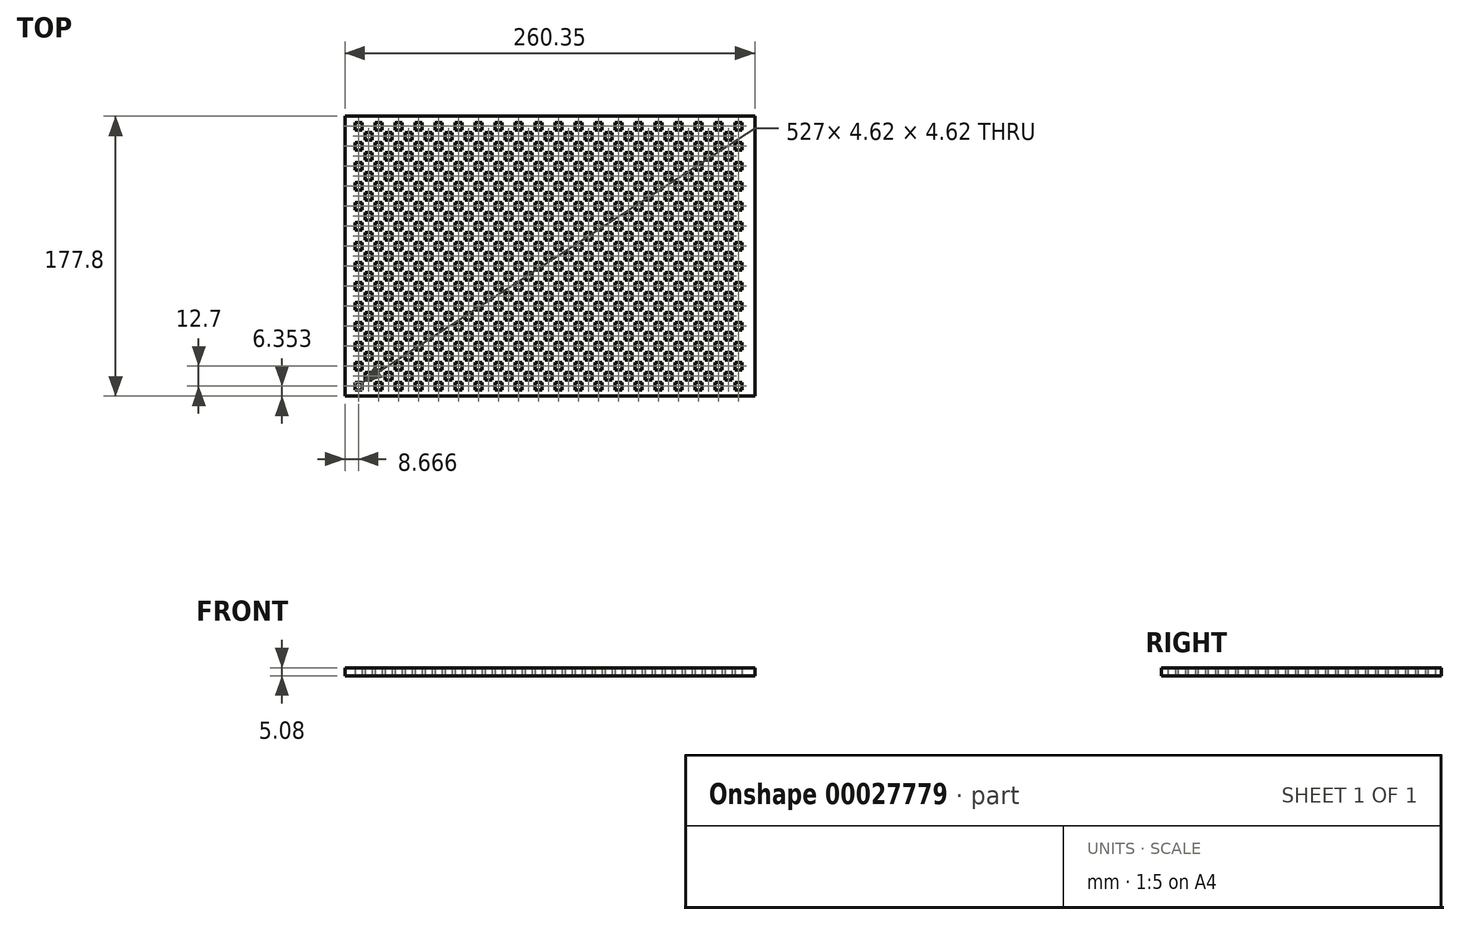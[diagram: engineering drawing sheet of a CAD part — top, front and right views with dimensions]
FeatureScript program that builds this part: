
annotation { "Feature Type Name" : "Feature", "Feature Type Description" : "" }
export const myFeature = defineFeature(function(context is Context, id is Id, definition is map)
    precondition{}
    {
        {
            var Q0;
            Q0=qCreatedBy(makeId("Top.planeOp"),FACE);
            var sketch = newSketch(context, id + "F0", { "sketchPlane" : qUnion([Q0])});
            skLineSegment(sketch, "E0.bottom", {"start": v(-130.56, -73.68) * mm, "end": v(129.8, -73.68) * mm});
            skLineSegment(sketch, "E0.top", {"start": v(-130.56, 104.12) * mm, "end": v(129.8, 104.12) * mm});
            skLineSegment(sketch, "E0.left", {"start": v(-130.56, -73.68) * mm, "end": v(-130.56, 104.12) * mm});
            skLineSegment(sketch, "E0.right", {"start": v(129.8, -73.68) * mm, "end": v(129.8, 104.12) * mm});
            skLineSegment(sketch, "E1.bottom", {"start": v(-124.2, 100.08) * mm, "end": v(-119.58, 100.08) * mm});
            skLineSegment(sketch, "E1.top", {"start": v(-124.2, 95.46) * mm, "end": v(-119.58, 95.46) * mm});
            skLineSegment(sketch, "E1.left", {"start": v(-124.2, 100.08) * mm, "end": v(-124.2, 95.46) * mm});
            skLineSegment(sketch, "E1.right", {"start": v(-119.58, 100.08) * mm, "end": v(-119.58, 95.46) * mm});
            skLineSegment(sketch, "E2.0.1.0", {"start": v(-124.2, 87.38) * mm, "end": v(-119.58, 87.38) * mm});
            skLineSegment(sketch, "E2.0.1.1", {"start": v(-119.58, 87.38) * mm, "end": v(-119.58, 82.76) * mm});
            skLineSegment(sketch, "E2.0.1.2", {"start": v(-124.2, 82.76) * mm, "end": v(-119.58, 82.76) * mm});
            skLineSegment(sketch, "E2.0.1.3", {"start": v(-124.2, 87.38) * mm, "end": v(-124.2, 82.76) * mm});
            skLineSegment(sketch, "E2.0.2.0", {"start": v(-124.2, 74.68) * mm, "end": v(-119.58, 74.68) * mm});
            skLineSegment(sketch, "E2.0.2.1", {"start": v(-119.58, 74.68) * mm, "end": v(-119.58, 70.06) * mm});
            skLineSegment(sketch, "E2.0.2.2", {"start": v(-124.2, 70.06) * mm, "end": v(-119.58, 70.06) * mm});
            skLineSegment(sketch, "E2.0.2.3", {"start": v(-124.2, 74.68) * mm, "end": v(-124.2, 70.06) * mm});
            skLineSegment(sketch, "E2.0.3.0", {"start": v(-124.2, 61.98) * mm, "end": v(-119.58, 61.98) * mm});
            skLineSegment(sketch, "E2.0.3.1", {"start": v(-119.58, 61.98) * mm, "end": v(-119.58, 57.36) * mm});
            skLineSegment(sketch, "E2.0.3.2", {"start": v(-124.2, 57.36) * mm, "end": v(-119.58, 57.36) * mm});
            skLineSegment(sketch, "E2.0.3.3", {"start": v(-124.2, 61.98) * mm, "end": v(-124.2, 57.36) * mm});
            skLineSegment(sketch, "E2.0.4.0", {"start": v(-124.2, 49.28) * mm, "end": v(-119.58, 49.28) * mm});
            skLineSegment(sketch, "E2.0.4.1", {"start": v(-119.58, 49.28) * mm, "end": v(-119.58, 44.66) * mm});
            skLineSegment(sketch, "E2.0.4.2", {"start": v(-124.2, 44.66) * mm, "end": v(-119.58, 44.66) * mm});
            skLineSegment(sketch, "E2.0.4.3", {"start": v(-124.2, 49.28) * mm, "end": v(-124.2, 44.66) * mm});
            skLineSegment(sketch, "E2.0.5.0", {"start": v(-124.2, 36.58) * mm, "end": v(-119.58, 36.58) * mm});
            skLineSegment(sketch, "E2.0.5.1", {"start": v(-119.58, 36.58) * mm, "end": v(-119.58, 31.96) * mm});
            skLineSegment(sketch, "E2.0.5.2", {"start": v(-124.2, 31.96) * mm, "end": v(-119.58, 31.96) * mm});
            skLineSegment(sketch, "E2.0.5.3", {"start": v(-124.2, 36.58) * mm, "end": v(-124.2, 31.96) * mm});
            skLineSegment(sketch, "E2.0.6.0", {"start": v(-124.2, 23.88) * mm, "end": v(-119.58, 23.88) * mm});
            skLineSegment(sketch, "E2.0.6.1", {"start": v(-119.58, 23.88) * mm, "end": v(-119.58, 19.26) * mm});
            skLineSegment(sketch, "E2.0.6.2", {"start": v(-124.2, 19.26) * mm, "end": v(-119.58, 19.26) * mm});
            skLineSegment(sketch, "E2.0.6.3", {"start": v(-124.2, 23.88) * mm, "end": v(-124.2, 19.26) * mm});
            skLineSegment(sketch, "E2.0.7.0", {"start": v(-124.2, 11.18) * mm, "end": v(-119.58, 11.18) * mm});
            skLineSegment(sketch, "E2.0.7.1", {"start": v(-119.58, 11.18) * mm, "end": v(-119.58, 6.56) * mm});
            skLineSegment(sketch, "E2.0.7.2", {"start": v(-124.2, 6.56) * mm, "end": v(-119.58, 6.56) * mm});
            skLineSegment(sketch, "E2.0.7.3", {"start": v(-124.2, 11.18) * mm, "end": v(-124.2, 6.56) * mm});
            skLineSegment(sketch, "E2.0.8.0", {"start": v(-124.2, -1.52) * mm, "end": v(-119.58, -1.52) * mm});
            skLineSegment(sketch, "E2.0.8.1", {"start": v(-119.58, -1.52) * mm, "end": v(-119.58, -6.14) * mm});
            skLineSegment(sketch, "E2.0.8.2", {"start": v(-124.2, -6.14) * mm, "end": v(-119.58, -6.14) * mm});
            skLineSegment(sketch, "E2.0.8.3", {"start": v(-124.2, -1.52) * mm, "end": v(-124.2, -6.14) * mm});
            skLineSegment(sketch, "E2.0.9.0", {"start": v(-124.2, -14.22) * mm, "end": v(-119.58, -14.22) * mm});
            skLineSegment(sketch, "E2.0.9.1", {"start": v(-119.58, -14.22) * mm, "end": v(-119.58, -18.84) * mm});
            skLineSegment(sketch, "E2.0.9.2", {"start": v(-124.2, -18.84) * mm, "end": v(-119.58, -18.84) * mm});
            skLineSegment(sketch, "E2.0.9.3", {"start": v(-124.2, -14.22) * mm, "end": v(-124.2, -18.84) * mm});
            skLineSegment(sketch, "E2.0.10.0", {"start": v(-124.2, -26.92) * mm, "end": v(-119.58, -26.92) * mm});
            skLineSegment(sketch, "E2.0.10.1", {"start": v(-119.58, -26.92) * mm, "end": v(-119.58, -31.54) * mm});
            skLineSegment(sketch, "E2.0.10.2", {"start": v(-124.2, -31.54) * mm, "end": v(-119.58, -31.54) * mm});
            skLineSegment(sketch, "E2.0.10.3", {"start": v(-124.2, -26.92) * mm, "end": v(-124.2, -31.54) * mm});
            skLineSegment(sketch, "E2.0.11.0", {"start": v(-124.2, -39.62) * mm, "end": v(-119.58, -39.62) * mm});
            skLineSegment(sketch, "E2.0.11.1", {"start": v(-119.58, -39.62) * mm, "end": v(-119.58, -44.24) * mm});
            skLineSegment(sketch, "E2.0.11.2", {"start": v(-124.2, -44.24) * mm, "end": v(-119.58, -44.24) * mm});
            skLineSegment(sketch, "E2.0.11.3", {"start": v(-124.2, -39.62) * mm, "end": v(-124.2, -44.24) * mm});
            skLineSegment(sketch, "E2.0.12.0", {"start": v(-124.2, -52.32) * mm, "end": v(-119.58, -52.32) * mm});
            skLineSegment(sketch, "E2.0.12.1", {"start": v(-119.58, -52.32) * mm, "end": v(-119.58, -56.94) * mm});
            skLineSegment(sketch, "E2.0.12.2", {"start": v(-124.2, -56.94) * mm, "end": v(-119.58, -56.94) * mm});
            skLineSegment(sketch, "E2.0.12.3", {"start": v(-124.2, -52.32) * mm, "end": v(-124.2, -56.94) * mm});
            skLineSegment(sketch, "E2.0.13.0", {"start": v(-124.2, -65.02) * mm, "end": v(-119.58, -65.02) * mm});
            skLineSegment(sketch, "E2.0.13.1", {"start": v(-119.58, -65.02) * mm, "end": v(-119.58, -69.64) * mm});
            skLineSegment(sketch, "E2.0.13.2", {"start": v(-124.2, -69.64) * mm, "end": v(-119.58, -69.64) * mm});
            skLineSegment(sketch, "E2.0.13.3", {"start": v(-124.2, -65.02) * mm, "end": v(-124.2, -69.64) * mm});
            skLineSegment(sketch, "E2.1.0.0", {"start": v(-111.5, 100.08) * mm, "end": v(-106.88, 100.08) * mm});
            skLineSegment(sketch, "E2.1.0.1", {"start": v(-106.88, 100.08) * mm, "end": v(-106.88, 95.46) * mm});
            skLineSegment(sketch, "E2.1.0.2", {"start": v(-111.5, 95.46) * mm, "end": v(-106.88, 95.46) * mm});
            skLineSegment(sketch, "E2.1.0.3", {"start": v(-111.5, 100.08) * mm, "end": v(-111.5, 95.46) * mm});
            skLineSegment(sketch, "E2.1.1.0", {"start": v(-111.5, 87.38) * mm, "end": v(-106.88, 87.38) * mm});
            skLineSegment(sketch, "E2.1.1.1", {"start": v(-106.88, 87.38) * mm, "end": v(-106.88, 82.76) * mm});
            skLineSegment(sketch, "E2.1.1.2", {"start": v(-111.5, 82.76) * mm, "end": v(-106.88, 82.76) * mm});
            skLineSegment(sketch, "E2.1.1.3", {"start": v(-111.5, 87.38) * mm, "end": v(-111.5, 82.76) * mm});
            skLineSegment(sketch, "E2.1.2.0", {"start": v(-111.5, 74.68) * mm, "end": v(-106.88, 74.68) * mm});
            skLineSegment(sketch, "E2.1.2.1", {"start": v(-106.88, 74.68) * mm, "end": v(-106.88, 70.06) * mm});
            skLineSegment(sketch, "E2.1.2.2", {"start": v(-111.5, 70.06) * mm, "end": v(-106.88, 70.06) * mm});
            skLineSegment(sketch, "E2.1.2.3", {"start": v(-111.5, 74.68) * mm, "end": v(-111.5, 70.06) * mm});
            skLineSegment(sketch, "E2.1.3.0", {"start": v(-111.5, 61.98) * mm, "end": v(-106.88, 61.98) * mm});
            skLineSegment(sketch, "E2.1.3.1", {"start": v(-106.88, 61.98) * mm, "end": v(-106.88, 57.36) * mm});
            skLineSegment(sketch, "E2.1.3.2", {"start": v(-111.5, 57.36) * mm, "end": v(-106.88, 57.36) * mm});
            skLineSegment(sketch, "E2.1.3.3", {"start": v(-111.5, 61.98) * mm, "end": v(-111.5, 57.36) * mm});
            skLineSegment(sketch, "E2.1.4.0", {"start": v(-111.5, 49.28) * mm, "end": v(-106.88, 49.28) * mm});
            skLineSegment(sketch, "E2.1.4.1", {"start": v(-106.88, 49.28) * mm, "end": v(-106.88, 44.66) * mm});
            skLineSegment(sketch, "E2.1.4.2", {"start": v(-111.5, 44.66) * mm, "end": v(-106.88, 44.66) * mm});
            skLineSegment(sketch, "E2.1.4.3", {"start": v(-111.5, 49.28) * mm, "end": v(-111.5, 44.66) * mm});
            skLineSegment(sketch, "E2.1.5.0", {"start": v(-111.5, 36.58) * mm, "end": v(-106.88, 36.58) * mm});
            skLineSegment(sketch, "E2.1.5.1", {"start": v(-106.88, 36.58) * mm, "end": v(-106.88, 31.96) * mm});
            skLineSegment(sketch, "E2.1.5.2", {"start": v(-111.5, 31.96) * mm, "end": v(-106.88, 31.96) * mm});
            skLineSegment(sketch, "E2.1.5.3", {"start": v(-111.5, 36.58) * mm, "end": v(-111.5, 31.96) * mm});
            skLineSegment(sketch, "E2.1.6.0", {"start": v(-111.5, 23.88) * mm, "end": v(-106.88, 23.88) * mm});
            skLineSegment(sketch, "E2.1.6.1", {"start": v(-106.88, 23.88) * mm, "end": v(-106.88, 19.26) * mm});
            skLineSegment(sketch, "E2.1.6.2", {"start": v(-111.5, 19.26) * mm, "end": v(-106.88, 19.26) * mm});
            skLineSegment(sketch, "E2.1.6.3", {"start": v(-111.5, 23.88) * mm, "end": v(-111.5, 19.26) * mm});
            skLineSegment(sketch, "E2.1.7.0", {"start": v(-111.5, 11.18) * mm, "end": v(-106.88, 11.18) * mm});
            skLineSegment(sketch, "E2.1.7.1", {"start": v(-106.88, 11.18) * mm, "end": v(-106.88, 6.56) * mm});
            skLineSegment(sketch, "E2.1.7.2", {"start": v(-111.5, 6.56) * mm, "end": v(-106.88, 6.56) * mm});
            skLineSegment(sketch, "E2.1.7.3", {"start": v(-111.5, 11.18) * mm, "end": v(-111.5, 6.56) * mm});
            skLineSegment(sketch, "E2.1.8.0", {"start": v(-111.5, -1.52) * mm, "end": v(-106.88, -1.52) * mm});
            skLineSegment(sketch, "E2.1.8.1", {"start": v(-106.88, -1.52) * mm, "end": v(-106.88, -6.14) * mm});
            skLineSegment(sketch, "E2.1.8.2", {"start": v(-111.5, -6.14) * mm, "end": v(-106.88, -6.14) * mm});
            skLineSegment(sketch, "E2.1.8.3", {"start": v(-111.5, -1.52) * mm, "end": v(-111.5, -6.14) * mm});
            skLineSegment(sketch, "E2.1.9.0", {"start": v(-111.5, -14.22) * mm, "end": v(-106.88, -14.22) * mm});
            skLineSegment(sketch, "E2.1.9.1", {"start": v(-106.88, -14.22) * mm, "end": v(-106.88, -18.84) * mm});
            skLineSegment(sketch, "E2.1.9.2", {"start": v(-111.5, -18.84) * mm, "end": v(-106.88, -18.84) * mm});
            skLineSegment(sketch, "E2.1.9.3", {"start": v(-111.5, -14.22) * mm, "end": v(-111.5, -18.84) * mm});
            skLineSegment(sketch, "E2.1.10.0", {"start": v(-111.5, -26.92) * mm, "end": v(-106.88, -26.92) * mm});
            skLineSegment(sketch, "E2.1.10.1", {"start": v(-106.88, -26.92) * mm, "end": v(-106.88, -31.54) * mm});
            skLineSegment(sketch, "E2.1.10.2", {"start": v(-111.5, -31.54) * mm, "end": v(-106.88, -31.54) * mm});
            skLineSegment(sketch, "E2.1.10.3", {"start": v(-111.5, -26.92) * mm, "end": v(-111.5, -31.54) * mm});
            skLineSegment(sketch, "E2.1.11.0", {"start": v(-111.5, -39.62) * mm, "end": v(-106.88, -39.62) * mm});
            skLineSegment(sketch, "E2.1.11.1", {"start": v(-106.88, -39.62) * mm, "end": v(-106.88, -44.24) * mm});
            skLineSegment(sketch, "E2.1.11.2", {"start": v(-111.5, -44.24) * mm, "end": v(-106.88, -44.24) * mm});
            skLineSegment(sketch, "E2.1.11.3", {"start": v(-111.5, -39.62) * mm, "end": v(-111.5, -44.24) * mm});
            skLineSegment(sketch, "E2.1.12.0", {"start": v(-111.5, -52.32) * mm, "end": v(-106.88, -52.32) * mm});
            skLineSegment(sketch, "E2.1.12.1", {"start": v(-106.88, -52.32) * mm, "end": v(-106.88, -56.94) * mm});
            skLineSegment(sketch, "E2.1.12.2", {"start": v(-111.5, -56.94) * mm, "end": v(-106.88, -56.94) * mm});
            skLineSegment(sketch, "E2.1.12.3", {"start": v(-111.5, -52.32) * mm, "end": v(-111.5, -56.94) * mm});
            skLineSegment(sketch, "E2.1.13.0", {"start": v(-111.5, -65.02) * mm, "end": v(-106.88, -65.02) * mm});
            skLineSegment(sketch, "E2.1.13.1", {"start": v(-106.88, -65.02) * mm, "end": v(-106.88, -69.64) * mm});
            skLineSegment(sketch, "E2.1.13.2", {"start": v(-111.5, -69.64) * mm, "end": v(-106.88, -69.64) * mm});
            skLineSegment(sketch, "E2.1.13.3", {"start": v(-111.5, -65.02) * mm, "end": v(-111.5, -69.64) * mm});
            skLineSegment(sketch, "E2.2.0.0", {"start": v(-98.8, 100.08) * mm, "end": v(-94.18, 100.08) * mm});
            skLineSegment(sketch, "E2.2.0.1", {"start": v(-94.18, 100.08) * mm, "end": v(-94.18, 95.46) * mm});
            skLineSegment(sketch, "E2.2.0.2", {"start": v(-98.8, 95.46) * mm, "end": v(-94.18, 95.46) * mm});
            skLineSegment(sketch, "E2.2.0.3", {"start": v(-98.8, 100.08) * mm, "end": v(-98.8, 95.46) * mm});
            skLineSegment(sketch, "E2.2.1.0", {"start": v(-98.8, 87.38) * mm, "end": v(-94.18, 87.38) * mm});
            skLineSegment(sketch, "E2.2.1.1", {"start": v(-94.18, 87.38) * mm, "end": v(-94.18, 82.76) * mm});
            skLineSegment(sketch, "E2.2.1.2", {"start": v(-98.8, 82.76) * mm, "end": v(-94.18, 82.76) * mm});
            skLineSegment(sketch, "E2.2.1.3", {"start": v(-98.8, 87.38) * mm, "end": v(-98.8, 82.76) * mm});
            skLineSegment(sketch, "E2.2.2.0", {"start": v(-98.8, 74.68) * mm, "end": v(-94.18, 74.68) * mm});
            skLineSegment(sketch, "E2.2.2.1", {"start": v(-94.18, 74.68) * mm, "end": v(-94.18, 70.06) * mm});
            skLineSegment(sketch, "E2.2.2.2", {"start": v(-98.8, 70.06) * mm, "end": v(-94.18, 70.06) * mm});
            skLineSegment(sketch, "E2.2.2.3", {"start": v(-98.8, 74.68) * mm, "end": v(-98.8, 70.06) * mm});
            skLineSegment(sketch, "E2.2.3.0", {"start": v(-98.8, 61.98) * mm, "end": v(-94.18, 61.98) * mm});
            skLineSegment(sketch, "E2.2.3.1", {"start": v(-94.18, 61.98) * mm, "end": v(-94.18, 57.36) * mm});
            skLineSegment(sketch, "E2.2.3.2", {"start": v(-98.8, 57.36) * mm, "end": v(-94.18, 57.36) * mm});
            skLineSegment(sketch, "E2.2.3.3", {"start": v(-98.8, 61.98) * mm, "end": v(-98.8, 57.36) * mm});
            skLineSegment(sketch, "E2.2.4.0", {"start": v(-98.8, 49.28) * mm, "end": v(-94.18, 49.28) * mm});
            skLineSegment(sketch, "E2.2.4.1", {"start": v(-94.18, 49.28) * mm, "end": v(-94.18, 44.66) * mm});
            skLineSegment(sketch, "E2.2.4.2", {"start": v(-98.8, 44.66) * mm, "end": v(-94.18, 44.66) * mm});
            skLineSegment(sketch, "E2.2.4.3", {"start": v(-98.8, 49.28) * mm, "end": v(-98.8, 44.66) * mm});
            skLineSegment(sketch, "E2.2.5.0", {"start": v(-98.8, 36.58) * mm, "end": v(-94.18, 36.58) * mm});
            skLineSegment(sketch, "E2.2.5.1", {"start": v(-94.18, 36.58) * mm, "end": v(-94.18, 31.96) * mm});
            skLineSegment(sketch, "E2.2.5.2", {"start": v(-98.8, 31.96) * mm, "end": v(-94.18, 31.96) * mm});
            skLineSegment(sketch, "E2.2.5.3", {"start": v(-98.8, 36.58) * mm, "end": v(-98.8, 31.96) * mm});
            skLineSegment(sketch, "E2.2.6.0", {"start": v(-98.8, 23.88) * mm, "end": v(-94.18, 23.88) * mm});
            skLineSegment(sketch, "E2.2.6.1", {"start": v(-94.18, 23.88) * mm, "end": v(-94.18, 19.26) * mm});
            skLineSegment(sketch, "E2.2.6.2", {"start": v(-98.8, 19.26) * mm, "end": v(-94.18, 19.26) * mm});
            skLineSegment(sketch, "E2.2.6.3", {"start": v(-98.8, 23.88) * mm, "end": v(-98.8, 19.26) * mm});
            skLineSegment(sketch, "E2.2.7.0", {"start": v(-98.8, 11.18) * mm, "end": v(-94.18, 11.18) * mm});
            skLineSegment(sketch, "E2.2.7.1", {"start": v(-94.18, 11.18) * mm, "end": v(-94.18, 6.56) * mm});
            skLineSegment(sketch, "E2.2.7.2", {"start": v(-98.8, 6.56) * mm, "end": v(-94.18, 6.56) * mm});
            skLineSegment(sketch, "E2.2.7.3", {"start": v(-98.8, 11.18) * mm, "end": v(-98.8, 6.56) * mm});
            skLineSegment(sketch, "E2.2.8.0", {"start": v(-98.8, -1.52) * mm, "end": v(-94.18, -1.52) * mm});
            skLineSegment(sketch, "E2.2.8.1", {"start": v(-94.18, -1.52) * mm, "end": v(-94.18, -6.14) * mm});
            skLineSegment(sketch, "E2.2.8.2", {"start": v(-98.8, -6.14) * mm, "end": v(-94.18, -6.14) * mm});
            skLineSegment(sketch, "E2.2.8.3", {"start": v(-98.8, -1.52) * mm, "end": v(-98.8, -6.14) * mm});
            skLineSegment(sketch, "E2.2.9.0", {"start": v(-98.8, -14.22) * mm, "end": v(-94.18, -14.22) * mm});
            skLineSegment(sketch, "E2.2.9.1", {"start": v(-94.18, -14.22) * mm, "end": v(-94.18, -18.84) * mm});
            skLineSegment(sketch, "E2.2.9.2", {"start": v(-98.8, -18.84) * mm, "end": v(-94.18, -18.84) * mm});
            skLineSegment(sketch, "E2.2.9.3", {"start": v(-98.8, -14.22) * mm, "end": v(-98.8, -18.84) * mm});
            skLineSegment(sketch, "E2.2.10.0", {"start": v(-98.8, -26.92) * mm, "end": v(-94.18, -26.92) * mm});
            skLineSegment(sketch, "E2.2.10.1", {"start": v(-94.18, -26.92) * mm, "end": v(-94.18, -31.54) * mm});
            skLineSegment(sketch, "E2.2.10.2", {"start": v(-98.8, -31.54) * mm, "end": v(-94.18, -31.54) * mm});
            skLineSegment(sketch, "E2.2.10.3", {"start": v(-98.8, -26.92) * mm, "end": v(-98.8, -31.54) * mm});
            skLineSegment(sketch, "E2.2.11.0", {"start": v(-98.8, -39.62) * mm, "end": v(-94.18, -39.62) * mm});
            skLineSegment(sketch, "E2.2.11.1", {"start": v(-94.18, -39.62) * mm, "end": v(-94.18, -44.24) * mm});
            skLineSegment(sketch, "E2.2.11.2", {"start": v(-98.8, -44.24) * mm, "end": v(-94.18, -44.24) * mm});
            skLineSegment(sketch, "E2.2.11.3", {"start": v(-98.8, -39.62) * mm, "end": v(-98.8, -44.24) * mm});
            skLineSegment(sketch, "E2.2.12.0", {"start": v(-98.8, -52.32) * mm, "end": v(-94.18, -52.32) * mm});
            skLineSegment(sketch, "E2.2.12.1", {"start": v(-94.18, -52.32) * mm, "end": v(-94.18, -56.94) * mm});
            skLineSegment(sketch, "E2.2.12.2", {"start": v(-98.8, -56.94) * mm, "end": v(-94.18, -56.94) * mm});
            skLineSegment(sketch, "E2.2.12.3", {"start": v(-98.8, -52.32) * mm, "end": v(-98.8, -56.94) * mm});
            skLineSegment(sketch, "E2.2.13.0", {"start": v(-98.8, -65.02) * mm, "end": v(-94.18, -65.02) * mm});
            skLineSegment(sketch, "E2.2.13.1", {"start": v(-94.18, -65.02) * mm, "end": v(-94.18, -69.64) * mm});
            skLineSegment(sketch, "E2.2.13.2", {"start": v(-98.8, -69.64) * mm, "end": v(-94.18, -69.64) * mm});
            skLineSegment(sketch, "E2.2.13.3", {"start": v(-98.8, -65.02) * mm, "end": v(-98.8, -69.64) * mm});
            skLineSegment(sketch, "E2.3.0.0", {"start": v(-86.1, 100.08) * mm, "end": v(-81.48, 100.08) * mm});
            skLineSegment(sketch, "E2.3.0.1", {"start": v(-81.48, 100.08) * mm, "end": v(-81.48, 95.46) * mm});
            skLineSegment(sketch, "E2.3.0.2", {"start": v(-86.1, 95.46) * mm, "end": v(-81.48, 95.46) * mm});
            skLineSegment(sketch, "E2.3.0.3", {"start": v(-86.1, 100.08) * mm, "end": v(-86.1, 95.46) * mm});
            skLineSegment(sketch, "E2.3.1.0", {"start": v(-86.1, 87.38) * mm, "end": v(-81.48, 87.38) * mm});
            skLineSegment(sketch, "E2.3.1.1", {"start": v(-81.48, 87.38) * mm, "end": v(-81.48, 82.76) * mm});
            skLineSegment(sketch, "E2.3.1.2", {"start": v(-86.1, 82.76) * mm, "end": v(-81.48, 82.76) * mm});
            skLineSegment(sketch, "E2.3.1.3", {"start": v(-86.1, 87.38) * mm, "end": v(-86.1, 82.76) * mm});
            skLineSegment(sketch, "E2.3.2.0", {"start": v(-86.1, 74.68) * mm, "end": v(-81.48, 74.68) * mm});
            skLineSegment(sketch, "E2.3.2.1", {"start": v(-81.48, 74.68) * mm, "end": v(-81.48, 70.06) * mm});
            skLineSegment(sketch, "E2.3.2.2", {"start": v(-86.1, 70.06) * mm, "end": v(-81.48, 70.06) * mm});
            skLineSegment(sketch, "E2.3.2.3", {"start": v(-86.1, 74.68) * mm, "end": v(-86.1, 70.06) * mm});
            skLineSegment(sketch, "E2.3.3.0", {"start": v(-86.1, 61.98) * mm, "end": v(-81.48, 61.98) * mm});
            skLineSegment(sketch, "E2.3.3.1", {"start": v(-81.48, 61.98) * mm, "end": v(-81.48, 57.36) * mm});
            skLineSegment(sketch, "E2.3.3.2", {"start": v(-86.1, 57.36) * mm, "end": v(-81.48, 57.36) * mm});
            skLineSegment(sketch, "E2.3.3.3", {"start": v(-86.1, 61.98) * mm, "end": v(-86.1, 57.36) * mm});
            skLineSegment(sketch, "E2.3.4.0", {"start": v(-86.1, 49.28) * mm, "end": v(-81.48, 49.28) * mm});
            skLineSegment(sketch, "E2.3.4.1", {"start": v(-81.48, 49.28) * mm, "end": v(-81.48, 44.66) * mm});
            skLineSegment(sketch, "E2.3.4.2", {"start": v(-86.1, 44.66) * mm, "end": v(-81.48, 44.66) * mm});
            skLineSegment(sketch, "E2.3.4.3", {"start": v(-86.1, 49.28) * mm, "end": v(-86.1, 44.66) * mm});
            skLineSegment(sketch, "E2.3.5.0", {"start": v(-86.1, 36.58) * mm, "end": v(-81.48, 36.58) * mm});
            skLineSegment(sketch, "E2.3.5.1", {"start": v(-81.48, 36.58) * mm, "end": v(-81.48, 31.96) * mm});
            skLineSegment(sketch, "E2.3.5.2", {"start": v(-86.1, 31.96) * mm, "end": v(-81.48, 31.96) * mm});
            skLineSegment(sketch, "E2.3.5.3", {"start": v(-86.1, 36.58) * mm, "end": v(-86.1, 31.96) * mm});
            skLineSegment(sketch, "E2.3.6.0", {"start": v(-86.1, 23.88) * mm, "end": v(-81.48, 23.88) * mm});
            skLineSegment(sketch, "E2.3.6.1", {"start": v(-81.48, 23.88) * mm, "end": v(-81.48, 19.26) * mm});
            skLineSegment(sketch, "E2.3.6.2", {"start": v(-86.1, 19.26) * mm, "end": v(-81.48, 19.26) * mm});
            skLineSegment(sketch, "E2.3.6.3", {"start": v(-86.1, 23.88) * mm, "end": v(-86.1, 19.26) * mm});
            skLineSegment(sketch, "E2.3.7.0", {"start": v(-86.1, 11.18) * mm, "end": v(-81.48, 11.18) * mm});
            skLineSegment(sketch, "E2.3.7.1", {"start": v(-81.48, 11.18) * mm, "end": v(-81.48, 6.56) * mm});
            skLineSegment(sketch, "E2.3.7.2", {"start": v(-86.1, 6.56) * mm, "end": v(-81.48, 6.56) * mm});
            skLineSegment(sketch, "E2.3.7.3", {"start": v(-86.1, 11.18) * mm, "end": v(-86.1, 6.56) * mm});
            skLineSegment(sketch, "E2.3.8.0", {"start": v(-86.1, -1.52) * mm, "end": v(-81.48, -1.52) * mm});
            skLineSegment(sketch, "E2.3.8.1", {"start": v(-81.48, -1.52) * mm, "end": v(-81.48, -6.14) * mm});
            skLineSegment(sketch, "E2.3.8.2", {"start": v(-86.1, -6.14) * mm, "end": v(-81.48, -6.14) * mm});
            skLineSegment(sketch, "E2.3.8.3", {"start": v(-86.1, -1.52) * mm, "end": v(-86.1, -6.14) * mm});
            skLineSegment(sketch, "E2.3.9.0", {"start": v(-86.1, -14.22) * mm, "end": v(-81.48, -14.22) * mm});
            skLineSegment(sketch, "E2.3.9.1", {"start": v(-81.48, -14.22) * mm, "end": v(-81.48, -18.84) * mm});
            skLineSegment(sketch, "E2.3.9.2", {"start": v(-86.1, -18.84) * mm, "end": v(-81.48, -18.84) * mm});
            skLineSegment(sketch, "E2.3.9.3", {"start": v(-86.1, -14.22) * mm, "end": v(-86.1, -18.84) * mm});
            skLineSegment(sketch, "E2.3.10.0", {"start": v(-86.1, -26.92) * mm, "end": v(-81.48, -26.92) * mm});
            skLineSegment(sketch, "E2.3.10.1", {"start": v(-81.48, -26.92) * mm, "end": v(-81.48, -31.54) * mm});
            skLineSegment(sketch, "E2.3.10.2", {"start": v(-86.1, -31.54) * mm, "end": v(-81.48, -31.54) * mm});
            skLineSegment(sketch, "E2.3.10.3", {"start": v(-86.1, -26.92) * mm, "end": v(-86.1, -31.54) * mm});
            skLineSegment(sketch, "E2.3.11.0", {"start": v(-86.1, -39.62) * mm, "end": v(-81.48, -39.62) * mm});
            skLineSegment(sketch, "E2.3.11.1", {"start": v(-81.48, -39.62) * mm, "end": v(-81.48, -44.24) * mm});
            skLineSegment(sketch, "E2.3.11.2", {"start": v(-86.1, -44.24) * mm, "end": v(-81.48, -44.24) * mm});
            skLineSegment(sketch, "E2.3.11.3", {"start": v(-86.1, -39.62) * mm, "end": v(-86.1, -44.24) * mm});
            skLineSegment(sketch, "E2.3.12.0", {"start": v(-86.1, -52.32) * mm, "end": v(-81.48, -52.32) * mm});
            skLineSegment(sketch, "E2.3.12.1", {"start": v(-81.48, -52.32) * mm, "end": v(-81.48, -56.94) * mm});
            skLineSegment(sketch, "E2.3.12.2", {"start": v(-86.1, -56.94) * mm, "end": v(-81.48, -56.94) * mm});
            skLineSegment(sketch, "E2.3.12.3", {"start": v(-86.1, -52.32) * mm, "end": v(-86.1, -56.94) * mm});
            skLineSegment(sketch, "E2.3.13.0", {"start": v(-86.1, -65.02) * mm, "end": v(-81.48, -65.02) * mm});
            skLineSegment(sketch, "E2.3.13.1", {"start": v(-81.48, -65.02) * mm, "end": v(-81.48, -69.64) * mm});
            skLineSegment(sketch, "E2.3.13.2", {"start": v(-86.1, -69.64) * mm, "end": v(-81.48, -69.64) * mm});
            skLineSegment(sketch, "E2.3.13.3", {"start": v(-86.1, -65.02) * mm, "end": v(-86.1, -69.64) * mm});
            skLineSegment(sketch, "E2.4.0.0", {"start": v(-73.4, 100.08) * mm, "end": v(-68.78, 100.08) * mm});
            skLineSegment(sketch, "E2.4.0.1", {"start": v(-68.78, 100.08) * mm, "end": v(-68.78, 95.46) * mm});
            skLineSegment(sketch, "E2.4.0.2", {"start": v(-73.4, 95.46) * mm, "end": v(-68.78, 95.46) * mm});
            skLineSegment(sketch, "E2.4.0.3", {"start": v(-73.4, 100.08) * mm, "end": v(-73.4, 95.46) * mm});
            skLineSegment(sketch, "E2.4.1.0", {"start": v(-73.4, 87.38) * mm, "end": v(-68.78, 87.38) * mm});
            skLineSegment(sketch, "E2.4.1.1", {"start": v(-68.78, 87.38) * mm, "end": v(-68.78, 82.76) * mm});
            skLineSegment(sketch, "E2.4.1.2", {"start": v(-73.4, 82.76) * mm, "end": v(-68.78, 82.76) * mm});
            skLineSegment(sketch, "E2.4.1.3", {"start": v(-73.4, 87.38) * mm, "end": v(-73.4, 82.76) * mm});
            skLineSegment(sketch, "E2.4.2.0", {"start": v(-73.4, 74.68) * mm, "end": v(-68.78, 74.68) * mm});
            skLineSegment(sketch, "E2.4.2.1", {"start": v(-68.78, 74.68) * mm, "end": v(-68.78, 70.06) * mm});
            skLineSegment(sketch, "E2.4.2.2", {"start": v(-73.4, 70.06) * mm, "end": v(-68.78, 70.06) * mm});
            skLineSegment(sketch, "E2.4.2.3", {"start": v(-73.4, 74.68) * mm, "end": v(-73.4, 70.06) * mm});
            skLineSegment(sketch, "E2.4.3.0", {"start": v(-73.4, 61.98) * mm, "end": v(-68.78, 61.98) * mm});
            skLineSegment(sketch, "E2.4.3.1", {"start": v(-68.78, 61.98) * mm, "end": v(-68.78, 57.36) * mm});
            skLineSegment(sketch, "E2.4.3.2", {"start": v(-73.4, 57.36) * mm, "end": v(-68.78, 57.36) * mm});
            skLineSegment(sketch, "E2.4.3.3", {"start": v(-73.4, 61.98) * mm, "end": v(-73.4, 57.36) * mm});
            skLineSegment(sketch, "E2.4.4.0", {"start": v(-73.4, 49.28) * mm, "end": v(-68.78, 49.28) * mm});
            skLineSegment(sketch, "E2.4.4.1", {"start": v(-68.78, 49.28) * mm, "end": v(-68.78, 44.66) * mm});
            skLineSegment(sketch, "E2.4.4.2", {"start": v(-73.4, 44.66) * mm, "end": v(-68.78, 44.66) * mm});
            skLineSegment(sketch, "E2.4.4.3", {"start": v(-73.4, 49.28) * mm, "end": v(-73.4, 44.66) * mm});
            skLineSegment(sketch, "E2.4.5.0", {"start": v(-73.4, 36.58) * mm, "end": v(-68.78, 36.58) * mm});
            skLineSegment(sketch, "E2.4.5.1", {"start": v(-68.78, 36.58) * mm, "end": v(-68.78, 31.96) * mm});
            skLineSegment(sketch, "E2.4.5.2", {"start": v(-73.4, 31.96) * mm, "end": v(-68.78, 31.96) * mm});
            skLineSegment(sketch, "E2.4.5.3", {"start": v(-73.4, 36.58) * mm, "end": v(-73.4, 31.96) * mm});
            skLineSegment(sketch, "E2.4.6.0", {"start": v(-73.4, 23.88) * mm, "end": v(-68.78, 23.88) * mm});
            skLineSegment(sketch, "E2.4.6.1", {"start": v(-68.78, 23.88) * mm, "end": v(-68.78, 19.26) * mm});
            skLineSegment(sketch, "E2.4.6.2", {"start": v(-73.4, 19.26) * mm, "end": v(-68.78, 19.26) * mm});
            skLineSegment(sketch, "E2.4.6.3", {"start": v(-73.4, 23.88) * mm, "end": v(-73.4, 19.26) * mm});
            skLineSegment(sketch, "E2.4.7.0", {"start": v(-73.4, 11.18) * mm, "end": v(-68.78, 11.18) * mm});
            skLineSegment(sketch, "E2.4.7.1", {"start": v(-68.78, 11.18) * mm, "end": v(-68.78, 6.56) * mm});
            skLineSegment(sketch, "E2.4.7.2", {"start": v(-73.4, 6.56) * mm, "end": v(-68.78, 6.56) * mm});
            skLineSegment(sketch, "E2.4.7.3", {"start": v(-73.4, 11.18) * mm, "end": v(-73.4, 6.56) * mm});
            skLineSegment(sketch, "E2.4.8.0", {"start": v(-73.4, -1.52) * mm, "end": v(-68.78, -1.52) * mm});
            skLineSegment(sketch, "E2.4.8.1", {"start": v(-68.78, -1.52) * mm, "end": v(-68.78, -6.14) * mm});
            skLineSegment(sketch, "E2.4.8.2", {"start": v(-73.4, -6.14) * mm, "end": v(-68.78, -6.14) * mm});
            skLineSegment(sketch, "E2.4.8.3", {"start": v(-73.4, -1.52) * mm, "end": v(-73.4, -6.14) * mm});
            skLineSegment(sketch, "E2.4.9.0", {"start": v(-73.4, -14.22) * mm, "end": v(-68.78, -14.22) * mm});
            skLineSegment(sketch, "E2.4.9.1", {"start": v(-68.78, -14.22) * mm, "end": v(-68.78, -18.84) * mm});
            skLineSegment(sketch, "E2.4.9.2", {"start": v(-73.4, -18.84) * mm, "end": v(-68.78, -18.84) * mm});
            skLineSegment(sketch, "E2.4.9.3", {"start": v(-73.4, -14.22) * mm, "end": v(-73.4, -18.84) * mm});
            skLineSegment(sketch, "E2.4.10.0", {"start": v(-73.4, -26.92) * mm, "end": v(-68.78, -26.92) * mm});
            skLineSegment(sketch, "E2.4.10.1", {"start": v(-68.78, -26.92) * mm, "end": v(-68.78, -31.54) * mm});
            skLineSegment(sketch, "E2.4.10.2", {"start": v(-73.4, -31.54) * mm, "end": v(-68.78, -31.54) * mm});
            skLineSegment(sketch, "E2.4.10.3", {"start": v(-73.4, -26.92) * mm, "end": v(-73.4, -31.54) * mm});
            skLineSegment(sketch, "E2.4.11.0", {"start": v(-73.4, -39.62) * mm, "end": v(-68.78, -39.62) * mm});
            skLineSegment(sketch, "E2.4.11.1", {"start": v(-68.78, -39.62) * mm, "end": v(-68.78, -44.24) * mm});
            skLineSegment(sketch, "E2.4.11.2", {"start": v(-73.4, -44.24) * mm, "end": v(-68.78, -44.24) * mm});
            skLineSegment(sketch, "E2.4.11.3", {"start": v(-73.4, -39.62) * mm, "end": v(-73.4, -44.24) * mm});
            skLineSegment(sketch, "E2.4.12.0", {"start": v(-73.4, -52.32) * mm, "end": v(-68.78, -52.32) * mm});
            skLineSegment(sketch, "E2.4.12.1", {"start": v(-68.78, -52.32) * mm, "end": v(-68.78, -56.94) * mm});
            skLineSegment(sketch, "E2.4.12.2", {"start": v(-73.4, -56.94) * mm, "end": v(-68.78, -56.94) * mm});
            skLineSegment(sketch, "E2.4.12.3", {"start": v(-73.4, -52.32) * mm, "end": v(-73.4, -56.94) * mm});
            skLineSegment(sketch, "E2.4.13.0", {"start": v(-73.4, -65.02) * mm, "end": v(-68.78, -65.02) * mm});
            skLineSegment(sketch, "E2.4.13.1", {"start": v(-68.78, -65.02) * mm, "end": v(-68.78, -69.64) * mm});
            skLineSegment(sketch, "E2.4.13.2", {"start": v(-73.4, -69.64) * mm, "end": v(-68.78, -69.64) * mm});
            skLineSegment(sketch, "E2.4.13.3", {"start": v(-73.4, -65.02) * mm, "end": v(-73.4, -69.64) * mm});
            skLineSegment(sketch, "E2.5.0.0", {"start": v(-60.7, 100.08) * mm, "end": v(-56.08, 100.08) * mm});
            skLineSegment(sketch, "E2.5.0.1", {"start": v(-56.08, 100.08) * mm, "end": v(-56.08, 95.46) * mm});
            skLineSegment(sketch, "E2.5.0.2", {"start": v(-60.7, 95.46) * mm, "end": v(-56.08, 95.46) * mm});
            skLineSegment(sketch, "E2.5.0.3", {"start": v(-60.7, 100.08) * mm, "end": v(-60.7, 95.46) * mm});
            skLineSegment(sketch, "E2.5.1.0", {"start": v(-60.7, 87.38) * mm, "end": v(-56.08, 87.38) * mm});
            skLineSegment(sketch, "E2.5.1.1", {"start": v(-56.08, 87.38) * mm, "end": v(-56.08, 82.76) * mm});
            skLineSegment(sketch, "E2.5.1.2", {"start": v(-60.7, 82.76) * mm, "end": v(-56.08, 82.76) * mm});
            skLineSegment(sketch, "E2.5.1.3", {"start": v(-60.7, 87.38) * mm, "end": v(-60.7, 82.76) * mm});
            skLineSegment(sketch, "E2.5.2.0", {"start": v(-60.7, 74.68) * mm, "end": v(-56.08, 74.68) * mm});
            skLineSegment(sketch, "E2.5.2.1", {"start": v(-56.08, 74.68) * mm, "end": v(-56.08, 70.06) * mm});
            skLineSegment(sketch, "E2.5.2.2", {"start": v(-60.7, 70.06) * mm, "end": v(-56.08, 70.06) * mm});
            skLineSegment(sketch, "E2.5.2.3", {"start": v(-60.7, 74.68) * mm, "end": v(-60.7, 70.06) * mm});
            skLineSegment(sketch, "E2.5.3.0", {"start": v(-60.7, 61.98) * mm, "end": v(-56.08, 61.98) * mm});
            skLineSegment(sketch, "E2.5.3.1", {"start": v(-56.08, 61.98) * mm, "end": v(-56.08, 57.36) * mm});
            skLineSegment(sketch, "E2.5.3.2", {"start": v(-60.7, 57.36) * mm, "end": v(-56.08, 57.36) * mm});
            skLineSegment(sketch, "E2.5.3.3", {"start": v(-60.7, 61.98) * mm, "end": v(-60.7, 57.36) * mm});
            skLineSegment(sketch, "E2.5.4.0", {"start": v(-60.7, 49.28) * mm, "end": v(-56.08, 49.28) * mm});
            skLineSegment(sketch, "E2.5.4.1", {"start": v(-56.08, 49.28) * mm, "end": v(-56.08, 44.66) * mm});
            skLineSegment(sketch, "E2.5.4.2", {"start": v(-60.7, 44.66) * mm, "end": v(-56.08, 44.66) * mm});
            skLineSegment(sketch, "E2.5.4.3", {"start": v(-60.7, 49.28) * mm, "end": v(-60.7, 44.66) * mm});
            skLineSegment(sketch, "E2.5.5.0", {"start": v(-60.7, 36.58) * mm, "end": v(-56.08, 36.58) * mm});
            skLineSegment(sketch, "E2.5.5.1", {"start": v(-56.08, 36.58) * mm, "end": v(-56.08, 31.96) * mm});
            skLineSegment(sketch, "E2.5.5.2", {"start": v(-60.7, 31.96) * mm, "end": v(-56.08, 31.96) * mm});
            skLineSegment(sketch, "E2.5.5.3", {"start": v(-60.7, 36.58) * mm, "end": v(-60.7, 31.96) * mm});
            skLineSegment(sketch, "E2.5.6.0", {"start": v(-60.7, 23.88) * mm, "end": v(-56.08, 23.88) * mm});
            skLineSegment(sketch, "E2.5.6.1", {"start": v(-56.08, 23.88) * mm, "end": v(-56.08, 19.26) * mm});
            skLineSegment(sketch, "E2.5.6.2", {"start": v(-60.7, 19.26) * mm, "end": v(-56.08, 19.26) * mm});
            skLineSegment(sketch, "E2.5.6.3", {"start": v(-60.7, 23.88) * mm, "end": v(-60.7, 19.26) * mm});
            skLineSegment(sketch, "E2.5.7.0", {"start": v(-60.7, 11.18) * mm, "end": v(-56.08, 11.18) * mm});
            skLineSegment(sketch, "E2.5.7.1", {"start": v(-56.08, 11.18) * mm, "end": v(-56.08, 6.56) * mm});
            skLineSegment(sketch, "E2.5.7.2", {"start": v(-60.7, 6.56) * mm, "end": v(-56.08, 6.56) * mm});
            skLineSegment(sketch, "E2.5.7.3", {"start": v(-60.7, 11.18) * mm, "end": v(-60.7, 6.56) * mm});
            skLineSegment(sketch, "E2.5.8.0", {"start": v(-60.7, -1.52) * mm, "end": v(-56.08, -1.52) * mm});
            skLineSegment(sketch, "E2.5.8.1", {"start": v(-56.08, -1.52) * mm, "end": v(-56.08, -6.14) * mm});
            skLineSegment(sketch, "E2.5.8.2", {"start": v(-60.7, -6.14) * mm, "end": v(-56.08, -6.14) * mm});
            skLineSegment(sketch, "E2.5.8.3", {"start": v(-60.7, -1.52) * mm, "end": v(-60.7, -6.14) * mm});
            skLineSegment(sketch, "E2.5.9.0", {"start": v(-60.7, -14.22) * mm, "end": v(-56.08, -14.22) * mm});
            skLineSegment(sketch, "E2.5.9.1", {"start": v(-56.08, -14.22) * mm, "end": v(-56.08, -18.84) * mm});
            skLineSegment(sketch, "E2.5.9.2", {"start": v(-60.7, -18.84) * mm, "end": v(-56.08, -18.84) * mm});
            skLineSegment(sketch, "E2.5.9.3", {"start": v(-60.7, -14.22) * mm, "end": v(-60.7, -18.84) * mm});
            skLineSegment(sketch, "E2.5.10.0", {"start": v(-60.7, -26.92) * mm, "end": v(-56.08, -26.92) * mm});
            skLineSegment(sketch, "E2.5.10.1", {"start": v(-56.08, -26.92) * mm, "end": v(-56.08, -31.54) * mm});
            skLineSegment(sketch, "E2.5.10.2", {"start": v(-60.7, -31.54) * mm, "end": v(-56.08, -31.54) * mm});
            skLineSegment(sketch, "E2.5.10.3", {"start": v(-60.7, -26.92) * mm, "end": v(-60.7, -31.54) * mm});
            skLineSegment(sketch, "E2.5.11.0", {"start": v(-60.7, -39.62) * mm, "end": v(-56.08, -39.62) * mm});
            skLineSegment(sketch, "E2.5.11.1", {"start": v(-56.08, -39.62) * mm, "end": v(-56.08, -44.24) * mm});
            skLineSegment(sketch, "E2.5.11.2", {"start": v(-60.7, -44.24) * mm, "end": v(-56.08, -44.24) * mm});
            skLineSegment(sketch, "E2.5.11.3", {"start": v(-60.7, -39.62) * mm, "end": v(-60.7, -44.24) * mm});
            skLineSegment(sketch, "E2.5.12.0", {"start": v(-60.7, -52.32) * mm, "end": v(-56.08, -52.32) * mm});
            skLineSegment(sketch, "E2.5.12.1", {"start": v(-56.08, -52.32) * mm, "end": v(-56.08, -56.94) * mm});
            skLineSegment(sketch, "E2.5.12.2", {"start": v(-60.7, -56.94) * mm, "end": v(-56.08, -56.94) * mm});
            skLineSegment(sketch, "E2.5.12.3", {"start": v(-60.7, -52.32) * mm, "end": v(-60.7, -56.94) * mm});
            skLineSegment(sketch, "E2.5.13.0", {"start": v(-60.7, -65.02) * mm, "end": v(-56.08, -65.02) * mm});
            skLineSegment(sketch, "E2.5.13.1", {"start": v(-56.08, -65.02) * mm, "end": v(-56.08, -69.64) * mm});
            skLineSegment(sketch, "E2.5.13.2", {"start": v(-60.7, -69.64) * mm, "end": v(-56.08, -69.64) * mm});
            skLineSegment(sketch, "E2.5.13.3", {"start": v(-60.7, -65.02) * mm, "end": v(-60.7, -69.64) * mm});
            skLineSegment(sketch, "E2.6.0.0", {"start": v(-48, 100.08) * mm, "end": v(-43.38, 100.08) * mm});
            skLineSegment(sketch, "E2.6.0.1", {"start": v(-43.38, 100.08) * mm, "end": v(-43.38, 95.46) * mm});
            skLineSegment(sketch, "E2.6.0.2", {"start": v(-48, 95.46) * mm, "end": v(-43.38, 95.46) * mm});
            skLineSegment(sketch, "E2.6.0.3", {"start": v(-48, 100.08) * mm, "end": v(-48, 95.46) * mm});
            skLineSegment(sketch, "E2.6.1.0", {"start": v(-48, 87.38) * mm, "end": v(-43.38, 87.38) * mm});
            skLineSegment(sketch, "E2.6.1.1", {"start": v(-43.38, 87.38) * mm, "end": v(-43.38, 82.76) * mm});
            skLineSegment(sketch, "E2.6.1.2", {"start": v(-48, 82.76) * mm, "end": v(-43.38, 82.76) * mm});
            skLineSegment(sketch, "E2.6.1.3", {"start": v(-48, 87.38) * mm, "end": v(-48, 82.76) * mm});
            skLineSegment(sketch, "E2.6.2.0", {"start": v(-48, 74.68) * mm, "end": v(-43.38, 74.68) * mm});
            skLineSegment(sketch, "E2.6.2.1", {"start": v(-43.38, 74.68) * mm, "end": v(-43.38, 70.06) * mm});
            skLineSegment(sketch, "E2.6.2.2", {"start": v(-48, 70.06) * mm, "end": v(-43.38, 70.06) * mm});
            skLineSegment(sketch, "E2.6.2.3", {"start": v(-48, 74.68) * mm, "end": v(-48, 70.06) * mm});
            skLineSegment(sketch, "E2.6.3.0", {"start": v(-48, 61.98) * mm, "end": v(-43.38, 61.98) * mm});
            skLineSegment(sketch, "E2.6.3.1", {"start": v(-43.38, 61.98) * mm, "end": v(-43.38, 57.36) * mm});
            skLineSegment(sketch, "E2.6.3.2", {"start": v(-48, 57.36) * mm, "end": v(-43.38, 57.36) * mm});
            skLineSegment(sketch, "E2.6.3.3", {"start": v(-48, 61.98) * mm, "end": v(-48, 57.36) * mm});
            skLineSegment(sketch, "E2.6.4.0", {"start": v(-48, 49.28) * mm, "end": v(-43.38, 49.28) * mm});
            skLineSegment(sketch, "E2.6.4.1", {"start": v(-43.38, 49.28) * mm, "end": v(-43.38, 44.66) * mm});
            skLineSegment(sketch, "E2.6.4.2", {"start": v(-48, 44.66) * mm, "end": v(-43.38, 44.66) * mm});
            skLineSegment(sketch, "E2.6.4.3", {"start": v(-48, 49.28) * mm, "end": v(-48, 44.66) * mm});
            skLineSegment(sketch, "E2.6.5.0", {"start": v(-48, 36.58) * mm, "end": v(-43.38, 36.58) * mm});
            skLineSegment(sketch, "E2.6.5.1", {"start": v(-43.38, 36.58) * mm, "end": v(-43.38, 31.96) * mm});
            skLineSegment(sketch, "E2.6.5.2", {"start": v(-48, 31.96) * mm, "end": v(-43.38, 31.96) * mm});
            skLineSegment(sketch, "E2.6.5.3", {"start": v(-48, 36.58) * mm, "end": v(-48, 31.96) * mm});
            skLineSegment(sketch, "E2.6.6.0", {"start": v(-48, 23.88) * mm, "end": v(-43.38, 23.88) * mm});
            skLineSegment(sketch, "E2.6.6.1", {"start": v(-43.38, 23.88) * mm, "end": v(-43.38, 19.26) * mm});
            skLineSegment(sketch, "E2.6.6.2", {"start": v(-48, 19.26) * mm, "end": v(-43.38, 19.26) * mm});
            skLineSegment(sketch, "E2.6.6.3", {"start": v(-48, 23.88) * mm, "end": v(-48, 19.26) * mm});
            skLineSegment(sketch, "E2.6.7.0", {"start": v(-48, 11.18) * mm, "end": v(-43.38, 11.18) * mm});
            skLineSegment(sketch, "E2.6.7.1", {"start": v(-43.38, 11.18) * mm, "end": v(-43.38, 6.56) * mm});
            skLineSegment(sketch, "E2.6.7.2", {"start": v(-48, 6.56) * mm, "end": v(-43.38, 6.56) * mm});
            skLineSegment(sketch, "E2.6.7.3", {"start": v(-48, 11.18) * mm, "end": v(-48, 6.56) * mm});
            skLineSegment(sketch, "E2.6.8.0", {"start": v(-48, -1.52) * mm, "end": v(-43.38, -1.52) * mm});
            skLineSegment(sketch, "E2.6.8.1", {"start": v(-43.38, -1.52) * mm, "end": v(-43.38, -6.14) * mm});
            skLineSegment(sketch, "E2.6.8.2", {"start": v(-48, -6.14) * mm, "end": v(-43.38, -6.14) * mm});
            skLineSegment(sketch, "E2.6.8.3", {"start": v(-48, -1.52) * mm, "end": v(-48, -6.14) * mm});
            skLineSegment(sketch, "E2.6.9.0", {"start": v(-48, -14.22) * mm, "end": v(-43.38, -14.22) * mm});
            skLineSegment(sketch, "E2.6.9.1", {"start": v(-43.38, -14.22) * mm, "end": v(-43.38, -18.84) * mm});
            skLineSegment(sketch, "E2.6.9.2", {"start": v(-48, -18.84) * mm, "end": v(-43.38, -18.84) * mm});
            skLineSegment(sketch, "E2.6.9.3", {"start": v(-48, -14.22) * mm, "end": v(-48, -18.84) * mm});
            skLineSegment(sketch, "E2.6.10.0", {"start": v(-48, -26.92) * mm, "end": v(-43.38, -26.92) * mm});
            skLineSegment(sketch, "E2.6.10.1", {"start": v(-43.38, -26.92) * mm, "end": v(-43.38, -31.54) * mm});
            skLineSegment(sketch, "E2.6.10.2", {"start": v(-48, -31.54) * mm, "end": v(-43.38, -31.54) * mm});
            skLineSegment(sketch, "E2.6.10.3", {"start": v(-48, -26.92) * mm, "end": v(-48, -31.54) * mm});
            skLineSegment(sketch, "E2.6.11.0", {"start": v(-48, -39.62) * mm, "end": v(-43.38, -39.62) * mm});
            skLineSegment(sketch, "E2.6.11.1", {"start": v(-43.38, -39.62) * mm, "end": v(-43.38, -44.24) * mm});
            skLineSegment(sketch, "E2.6.11.2", {"start": v(-48, -44.24) * mm, "end": v(-43.38, -44.24) * mm});
            skLineSegment(sketch, "E2.6.11.3", {"start": v(-48, -39.62) * mm, "end": v(-48, -44.24) * mm});
            skLineSegment(sketch, "E2.6.12.0", {"start": v(-48, -52.32) * mm, "end": v(-43.38, -52.32) * mm});
            skLineSegment(sketch, "E2.6.12.1", {"start": v(-43.38, -52.32) * mm, "end": v(-43.38, -56.94) * mm});
            skLineSegment(sketch, "E2.6.12.2", {"start": v(-48, -56.94) * mm, "end": v(-43.38, -56.94) * mm});
            skLineSegment(sketch, "E2.6.12.3", {"start": v(-48, -52.32) * mm, "end": v(-48, -56.94) * mm});
            skLineSegment(sketch, "E2.6.13.0", {"start": v(-48, -65.02) * mm, "end": v(-43.38, -65.02) * mm});
            skLineSegment(sketch, "E2.6.13.1", {"start": v(-43.38, -65.02) * mm, "end": v(-43.38, -69.64) * mm});
            skLineSegment(sketch, "E2.6.13.2", {"start": v(-48, -69.64) * mm, "end": v(-43.38, -69.64) * mm});
            skLineSegment(sketch, "E2.6.13.3", {"start": v(-48, -65.02) * mm, "end": v(-48, -69.64) * mm});
            skLineSegment(sketch, "E2.7.0.0", {"start": v(-35.3, 100.08) * mm, "end": v(-30.68, 100.08) * mm});
            skLineSegment(sketch, "E2.7.0.1", {"start": v(-30.68, 100.08) * mm, "end": v(-30.68, 95.46) * mm});
            skLineSegment(sketch, "E2.7.0.2", {"start": v(-35.3, 95.46) * mm, "end": v(-30.68, 95.46) * mm});
            skLineSegment(sketch, "E2.7.0.3", {"start": v(-35.3, 100.08) * mm, "end": v(-35.3, 95.46) * mm});
            skLineSegment(sketch, "E2.7.1.0", {"start": v(-35.3, 87.38) * mm, "end": v(-30.68, 87.38) * mm});
            skLineSegment(sketch, "E2.7.1.1", {"start": v(-30.68, 87.38) * mm, "end": v(-30.68, 82.76) * mm});
            skLineSegment(sketch, "E2.7.1.2", {"start": v(-35.3, 82.76) * mm, "end": v(-30.68, 82.76) * mm});
            skLineSegment(sketch, "E2.7.1.3", {"start": v(-35.3, 87.38) * mm, "end": v(-35.3, 82.76) * mm});
            skLineSegment(sketch, "E2.7.2.0", {"start": v(-35.3, 74.68) * mm, "end": v(-30.68, 74.68) * mm});
            skLineSegment(sketch, "E2.7.2.1", {"start": v(-30.68, 74.68) * mm, "end": v(-30.68, 70.06) * mm});
            skLineSegment(sketch, "E2.7.2.2", {"start": v(-35.3, 70.06) * mm, "end": v(-30.68, 70.06) * mm});
            skLineSegment(sketch, "E2.7.2.3", {"start": v(-35.3, 74.68) * mm, "end": v(-35.3, 70.06) * mm});
            skLineSegment(sketch, "E2.7.3.0", {"start": v(-35.3, 61.98) * mm, "end": v(-30.68, 61.98) * mm});
            skLineSegment(sketch, "E2.7.3.1", {"start": v(-30.68, 61.98) * mm, "end": v(-30.68, 57.36) * mm});
            skLineSegment(sketch, "E2.7.3.2", {"start": v(-35.3, 57.36) * mm, "end": v(-30.68, 57.36) * mm});
            skLineSegment(sketch, "E2.7.3.3", {"start": v(-35.3, 61.98) * mm, "end": v(-35.3, 57.36) * mm});
            skLineSegment(sketch, "E2.7.4.0", {"start": v(-35.3, 49.28) * mm, "end": v(-30.68, 49.28) * mm});
            skLineSegment(sketch, "E2.7.4.1", {"start": v(-30.68, 49.28) * mm, "end": v(-30.68, 44.66) * mm});
            skLineSegment(sketch, "E2.7.4.2", {"start": v(-35.3, 44.66) * mm, "end": v(-30.68, 44.66) * mm});
            skLineSegment(sketch, "E2.7.4.3", {"start": v(-35.3, 49.28) * mm, "end": v(-35.3, 44.66) * mm});
            skLineSegment(sketch, "E2.7.5.0", {"start": v(-35.3, 36.58) * mm, "end": v(-30.68, 36.58) * mm});
            skLineSegment(sketch, "E2.7.5.1", {"start": v(-30.68, 36.58) * mm, "end": v(-30.68, 31.96) * mm});
            skLineSegment(sketch, "E2.7.5.2", {"start": v(-35.3, 31.96) * mm, "end": v(-30.68, 31.96) * mm});
            skLineSegment(sketch, "E2.7.5.3", {"start": v(-35.3, 36.58) * mm, "end": v(-35.3, 31.96) * mm});
            skLineSegment(sketch, "E2.7.6.0", {"start": v(-35.3, 23.88) * mm, "end": v(-30.68, 23.88) * mm});
            skLineSegment(sketch, "E2.7.6.1", {"start": v(-30.68, 23.88) * mm, "end": v(-30.68, 19.26) * mm});
            skLineSegment(sketch, "E2.7.6.2", {"start": v(-35.3, 19.26) * mm, "end": v(-30.68, 19.26) * mm});
            skLineSegment(sketch, "E2.7.6.3", {"start": v(-35.3, 23.88) * mm, "end": v(-35.3, 19.26) * mm});
            skLineSegment(sketch, "E2.7.7.0", {"start": v(-35.3, 11.18) * mm, "end": v(-30.68, 11.18) * mm});
            skLineSegment(sketch, "E2.7.7.1", {"start": v(-30.68, 11.18) * mm, "end": v(-30.68, 6.56) * mm});
            skLineSegment(sketch, "E2.7.7.2", {"start": v(-35.3, 6.56) * mm, "end": v(-30.68, 6.56) * mm});
            skLineSegment(sketch, "E2.7.7.3", {"start": v(-35.3, 11.18) * mm, "end": v(-35.3, 6.56) * mm});
            skLineSegment(sketch, "E2.7.8.0", {"start": v(-35.3, -1.52) * mm, "end": v(-30.68, -1.52) * mm});
            skLineSegment(sketch, "E2.7.8.1", {"start": v(-30.68, -1.52) * mm, "end": v(-30.68, -6.14) * mm});
            skLineSegment(sketch, "E2.7.8.2", {"start": v(-35.3, -6.14) * mm, "end": v(-30.68, -6.14) * mm});
            skLineSegment(sketch, "E2.7.8.3", {"start": v(-35.3, -1.52) * mm, "end": v(-35.3, -6.14) * mm});
            skLineSegment(sketch, "E2.7.9.0", {"start": v(-35.3, -14.22) * mm, "end": v(-30.68, -14.22) * mm});
            skLineSegment(sketch, "E2.7.9.1", {"start": v(-30.68, -14.22) * mm, "end": v(-30.68, -18.84) * mm});
            skLineSegment(sketch, "E2.7.9.2", {"start": v(-35.3, -18.84) * mm, "end": v(-30.68, -18.84) * mm});
            skLineSegment(sketch, "E2.7.9.3", {"start": v(-35.3, -14.22) * mm, "end": v(-35.3, -18.84) * mm});
            skLineSegment(sketch, "E2.7.10.0", {"start": v(-35.3, -26.92) * mm, "end": v(-30.68, -26.92) * mm});
            skLineSegment(sketch, "E2.7.10.1", {"start": v(-30.68, -26.92) * mm, "end": v(-30.68, -31.54) * mm});
            skLineSegment(sketch, "E2.7.10.2", {"start": v(-35.3, -31.54) * mm, "end": v(-30.68, -31.54) * mm});
            skLineSegment(sketch, "E2.7.10.3", {"start": v(-35.3, -26.92) * mm, "end": v(-35.3, -31.54) * mm});
            skLineSegment(sketch, "E2.7.11.0", {"start": v(-35.3, -39.62) * mm, "end": v(-30.68, -39.62) * mm});
            skLineSegment(sketch, "E2.7.11.1", {"start": v(-30.68, -39.62) * mm, "end": v(-30.68, -44.24) * mm});
            skLineSegment(sketch, "E2.7.11.2", {"start": v(-35.3, -44.24) * mm, "end": v(-30.68, -44.24) * mm});
            skLineSegment(sketch, "E2.7.11.3", {"start": v(-35.3, -39.62) * mm, "end": v(-35.3, -44.24) * mm});
            skLineSegment(sketch, "E2.7.12.0", {"start": v(-35.3, -52.32) * mm, "end": v(-30.68, -52.32) * mm});
            skLineSegment(sketch, "E2.7.12.1", {"start": v(-30.68, -52.32) * mm, "end": v(-30.68, -56.94) * mm});
            skLineSegment(sketch, "E2.7.12.2", {"start": v(-35.3, -56.94) * mm, "end": v(-30.68, -56.94) * mm});
            skLineSegment(sketch, "E2.7.12.3", {"start": v(-35.3, -52.32) * mm, "end": v(-35.3, -56.94) * mm});
            skLineSegment(sketch, "E2.7.13.0", {"start": v(-35.3, -65.02) * mm, "end": v(-30.68, -65.02) * mm});
            skLineSegment(sketch, "E2.7.13.1", {"start": v(-30.68, -65.02) * mm, "end": v(-30.68, -69.64) * mm});
            skLineSegment(sketch, "E2.7.13.2", {"start": v(-35.3, -69.64) * mm, "end": v(-30.68, -69.64) * mm});
            skLineSegment(sketch, "E2.7.13.3", {"start": v(-35.3, -65.02) * mm, "end": v(-35.3, -69.64) * mm});
            skLineSegment(sketch, "E2.8.0.0", {"start": v(-22.6, 100.08) * mm, "end": v(-17.98, 100.08) * mm});
            skLineSegment(sketch, "E2.8.0.1", {"start": v(-17.98, 100.08) * mm, "end": v(-17.98, 95.46) * mm});
            skLineSegment(sketch, "E2.8.0.2", {"start": v(-22.6, 95.46) * mm, "end": v(-17.98, 95.46) * mm});
            skLineSegment(sketch, "E2.8.0.3", {"start": v(-22.6, 100.08) * mm, "end": v(-22.6, 95.46) * mm});
            skLineSegment(sketch, "E2.8.1.0", {"start": v(-22.6, 87.38) * mm, "end": v(-17.98, 87.38) * mm});
            skLineSegment(sketch, "E2.8.1.1", {"start": v(-17.98, 87.38) * mm, "end": v(-17.98, 82.76) * mm});
            skLineSegment(sketch, "E2.8.1.2", {"start": v(-22.6, 82.76) * mm, "end": v(-17.98, 82.76) * mm});
            skLineSegment(sketch, "E2.8.1.3", {"start": v(-22.6, 87.38) * mm, "end": v(-22.6, 82.76) * mm});
            skLineSegment(sketch, "E2.8.2.0", {"start": v(-22.6, 74.68) * mm, "end": v(-17.98, 74.68) * mm});
            skLineSegment(sketch, "E2.8.2.1", {"start": v(-17.98, 74.68) * mm, "end": v(-17.98, 70.06) * mm});
            skLineSegment(sketch, "E2.8.2.2", {"start": v(-22.6, 70.06) * mm, "end": v(-17.98, 70.06) * mm});
            skLineSegment(sketch, "E2.8.2.3", {"start": v(-22.6, 74.68) * mm, "end": v(-22.6, 70.06) * mm});
            skLineSegment(sketch, "E2.8.3.0", {"start": v(-22.6, 61.98) * mm, "end": v(-17.98, 61.98) * mm});
            skLineSegment(sketch, "E2.8.3.1", {"start": v(-17.98, 61.98) * mm, "end": v(-17.98, 57.36) * mm});
            skLineSegment(sketch, "E2.8.3.2", {"start": v(-22.6, 57.36) * mm, "end": v(-17.98, 57.36) * mm});
            skLineSegment(sketch, "E2.8.3.3", {"start": v(-22.6, 61.98) * mm, "end": v(-22.6, 57.36) * mm});
            skLineSegment(sketch, "E2.8.4.0", {"start": v(-22.6, 49.28) * mm, "end": v(-17.98, 49.28) * mm});
            skLineSegment(sketch, "E2.8.4.1", {"start": v(-17.98, 49.28) * mm, "end": v(-17.98, 44.66) * mm});
            skLineSegment(sketch, "E2.8.4.2", {"start": v(-22.6, 44.66) * mm, "end": v(-17.98, 44.66) * mm});
            skLineSegment(sketch, "E2.8.4.3", {"start": v(-22.6, 49.28) * mm, "end": v(-22.6, 44.66) * mm});
            skLineSegment(sketch, "E2.8.5.0", {"start": v(-22.6, 36.58) * mm, "end": v(-17.98, 36.58) * mm});
            skLineSegment(sketch, "E2.8.5.1", {"start": v(-17.98, 36.58) * mm, "end": v(-17.98, 31.96) * mm});
            skLineSegment(sketch, "E2.8.5.2", {"start": v(-22.6, 31.96) * mm, "end": v(-17.98, 31.96) * mm});
            skLineSegment(sketch, "E2.8.5.3", {"start": v(-22.6, 36.58) * mm, "end": v(-22.6, 31.96) * mm});
            skLineSegment(sketch, "E2.8.6.0", {"start": v(-22.6, 23.88) * mm, "end": v(-17.98, 23.88) * mm});
            skLineSegment(sketch, "E2.8.6.1", {"start": v(-17.98, 23.88) * mm, "end": v(-17.98, 19.26) * mm});
            skLineSegment(sketch, "E2.8.6.2", {"start": v(-22.6, 19.26) * mm, "end": v(-17.98, 19.26) * mm});
            skLineSegment(sketch, "E2.8.6.3", {"start": v(-22.6, 23.88) * mm, "end": v(-22.6, 19.26) * mm});
            skLineSegment(sketch, "E2.8.7.0", {"start": v(-22.6, 11.18) * mm, "end": v(-17.98, 11.18) * mm});
            skLineSegment(sketch, "E2.8.7.1", {"start": v(-17.98, 11.18) * mm, "end": v(-17.98, 6.56) * mm});
            skLineSegment(sketch, "E2.8.7.2", {"start": v(-22.6, 6.56) * mm, "end": v(-17.98, 6.56) * mm});
            skLineSegment(sketch, "E2.8.7.3", {"start": v(-22.6, 11.18) * mm, "end": v(-22.6, 6.56) * mm});
            skLineSegment(sketch, "E2.8.8.0", {"start": v(-22.6, -1.52) * mm, "end": v(-17.98, -1.52) * mm});
            skLineSegment(sketch, "E2.8.8.1", {"start": v(-17.98, -1.52) * mm, "end": v(-17.98, -6.14) * mm});
            skLineSegment(sketch, "E2.8.8.2", {"start": v(-22.6, -6.14) * mm, "end": v(-17.98, -6.14) * mm});
            skLineSegment(sketch, "E2.8.8.3", {"start": v(-22.6, -1.52) * mm, "end": v(-22.6, -6.14) * mm});
            skLineSegment(sketch, "E2.8.9.0", {"start": v(-22.6, -14.22) * mm, "end": v(-17.98, -14.22) * mm});
            skLineSegment(sketch, "E2.8.9.1", {"start": v(-17.98, -14.22) * mm, "end": v(-17.98, -18.84) * mm});
            skLineSegment(sketch, "E2.8.9.2", {"start": v(-22.6, -18.84) * mm, "end": v(-17.98, -18.84) * mm});
            skLineSegment(sketch, "E2.8.9.3", {"start": v(-22.6, -14.22) * mm, "end": v(-22.6, -18.84) * mm});
            skLineSegment(sketch, "E2.8.10.0", {"start": v(-22.6, -26.92) * mm, "end": v(-17.98, -26.92) * mm});
            skLineSegment(sketch, "E2.8.10.1", {"start": v(-17.98, -26.92) * mm, "end": v(-17.98, -31.54) * mm});
            skLineSegment(sketch, "E2.8.10.2", {"start": v(-22.6, -31.54) * mm, "end": v(-17.98, -31.54) * mm});
            skLineSegment(sketch, "E2.8.10.3", {"start": v(-22.6, -26.92) * mm, "end": v(-22.6, -31.54) * mm});
            skLineSegment(sketch, "E2.8.11.0", {"start": v(-22.6, -39.62) * mm, "end": v(-17.98, -39.62) * mm});
            skLineSegment(sketch, "E2.8.11.1", {"start": v(-17.98, -39.62) * mm, "end": v(-17.98, -44.24) * mm});
            skLineSegment(sketch, "E2.8.11.2", {"start": v(-22.6, -44.24) * mm, "end": v(-17.98, -44.24) * mm});
            skLineSegment(sketch, "E2.8.11.3", {"start": v(-22.6, -39.62) * mm, "end": v(-22.6, -44.24) * mm});
            skLineSegment(sketch, "E2.8.12.0", {"start": v(-22.6, -52.32) * mm, "end": v(-17.98, -52.32) * mm});
            skLineSegment(sketch, "E2.8.12.1", {"start": v(-17.98, -52.32) * mm, "end": v(-17.98, -56.94) * mm});
            skLineSegment(sketch, "E2.8.12.2", {"start": v(-22.6, -56.94) * mm, "end": v(-17.98, -56.94) * mm});
            skLineSegment(sketch, "E2.8.12.3", {"start": v(-22.6, -52.32) * mm, "end": v(-22.6, -56.94) * mm});
            skLineSegment(sketch, "E2.8.13.0", {"start": v(-22.6, -65.02) * mm, "end": v(-17.98, -65.02) * mm});
            skLineSegment(sketch, "E2.8.13.1", {"start": v(-17.98, -65.02) * mm, "end": v(-17.98, -69.64) * mm});
            skLineSegment(sketch, "E2.8.13.2", {"start": v(-22.6, -69.64) * mm, "end": v(-17.98, -69.64) * mm});
            skLineSegment(sketch, "E2.8.13.3", {"start": v(-22.6, -65.02) * mm, "end": v(-22.6, -69.64) * mm});
            skLineSegment(sketch, "E2.9.0.0", {"start": v(-9.9, 100.08) * mm, "end": v(-5.28, 100.08) * mm});
            skLineSegment(sketch, "E2.9.0.1", {"start": v(-5.28, 100.08) * mm, "end": v(-5.28, 95.46) * mm});
            skLineSegment(sketch, "E2.9.0.2", {"start": v(-9.9, 95.46) * mm, "end": v(-5.28, 95.46) * mm});
            skLineSegment(sketch, "E2.9.0.3", {"start": v(-9.9, 100.08) * mm, "end": v(-9.9, 95.46) * mm});
            skLineSegment(sketch, "E2.9.1.0", {"start": v(-9.9, 87.38) * mm, "end": v(-5.28, 87.38) * mm});
            skLineSegment(sketch, "E2.9.1.1", {"start": v(-5.28, 87.38) * mm, "end": v(-5.28, 82.76) * mm});
            skLineSegment(sketch, "E2.9.1.2", {"start": v(-9.9, 82.76) * mm, "end": v(-5.28, 82.76) * mm});
            skLineSegment(sketch, "E2.9.1.3", {"start": v(-9.9, 87.38) * mm, "end": v(-9.9, 82.76) * mm});
            skLineSegment(sketch, "E2.9.2.0", {"start": v(-9.9, 74.68) * mm, "end": v(-5.28, 74.68) * mm});
            skLineSegment(sketch, "E2.9.2.1", {"start": v(-5.28, 74.68) * mm, "end": v(-5.28, 70.06) * mm});
            skLineSegment(sketch, "E2.9.2.2", {"start": v(-9.9, 70.06) * mm, "end": v(-5.28, 70.06) * mm});
            skLineSegment(sketch, "E2.9.2.3", {"start": v(-9.9, 74.68) * mm, "end": v(-9.9, 70.06) * mm});
            skLineSegment(sketch, "E2.9.3.0", {"start": v(-9.9, 61.98) * mm, "end": v(-5.28, 61.98) * mm});
            skLineSegment(sketch, "E2.9.3.1", {"start": v(-5.28, 61.98) * mm, "end": v(-5.28, 57.36) * mm});
            skLineSegment(sketch, "E2.9.3.2", {"start": v(-9.9, 57.36) * mm, "end": v(-5.28, 57.36) * mm});
            skLineSegment(sketch, "E2.9.3.3", {"start": v(-9.9, 61.98) * mm, "end": v(-9.9, 57.36) * mm});
            skLineSegment(sketch, "E2.9.4.0", {"start": v(-9.9, 49.28) * mm, "end": v(-5.28, 49.28) * mm});
            skLineSegment(sketch, "E2.9.4.1", {"start": v(-5.28, 49.28) * mm, "end": v(-5.28, 44.66) * mm});
            skLineSegment(sketch, "E2.9.4.2", {"start": v(-9.9, 44.66) * mm, "end": v(-5.28, 44.66) * mm});
            skLineSegment(sketch, "E2.9.4.3", {"start": v(-9.9, 49.28) * mm, "end": v(-9.9, 44.66) * mm});
            skLineSegment(sketch, "E2.9.5.0", {"start": v(-9.9, 36.58) * mm, "end": v(-5.28, 36.58) * mm});
            skLineSegment(sketch, "E2.9.5.1", {"start": v(-5.28, 36.58) * mm, "end": v(-5.28, 31.96) * mm});
            skLineSegment(sketch, "E2.9.5.2", {"start": v(-9.9, 31.96) * mm, "end": v(-5.28, 31.96) * mm});
            skLineSegment(sketch, "E2.9.5.3", {"start": v(-9.9, 36.58) * mm, "end": v(-9.9, 31.96) * mm});
            skLineSegment(sketch, "E2.9.6.0", {"start": v(-9.9, 23.88) * mm, "end": v(-5.28, 23.88) * mm});
            skLineSegment(sketch, "E2.9.6.1", {"start": v(-5.28, 23.88) * mm, "end": v(-5.28, 19.26) * mm});
            skLineSegment(sketch, "E2.9.6.2", {"start": v(-9.9, 19.26) * mm, "end": v(-5.28, 19.26) * mm});
            skLineSegment(sketch, "E2.9.6.3", {"start": v(-9.9, 23.88) * mm, "end": v(-9.9, 19.26) * mm});
            skLineSegment(sketch, "E2.9.7.0", {"start": v(-9.9, 11.18) * mm, "end": v(-5.28, 11.18) * mm});
            skLineSegment(sketch, "E2.9.7.1", {"start": v(-5.28, 11.18) * mm, "end": v(-5.28, 6.56) * mm});
            skLineSegment(sketch, "E2.9.7.2", {"start": v(-9.9, 6.56) * mm, "end": v(-5.28, 6.56) * mm});
            skLineSegment(sketch, "E2.9.7.3", {"start": v(-9.9, 11.18) * mm, "end": v(-9.9, 6.56) * mm});
            skLineSegment(sketch, "E2.9.8.0", {"start": v(-9.9, -1.52) * mm, "end": v(-5.28, -1.52) * mm});
            skLineSegment(sketch, "E2.9.8.1", {"start": v(-5.28, -1.52) * mm, "end": v(-5.28, -6.14) * mm});
            skLineSegment(sketch, "E2.9.8.2", {"start": v(-9.9, -6.14) * mm, "end": v(-5.28, -6.14) * mm});
            skLineSegment(sketch, "E2.9.8.3", {"start": v(-9.9, -1.52) * mm, "end": v(-9.9, -6.14) * mm});
            skLineSegment(sketch, "E2.9.9.0", {"start": v(-9.9, -14.22) * mm, "end": v(-5.28, -14.22) * mm});
            skLineSegment(sketch, "E2.9.9.1", {"start": v(-5.28, -14.22) * mm, "end": v(-5.28, -18.84) * mm});
            skLineSegment(sketch, "E2.9.9.2", {"start": v(-9.9, -18.84) * mm, "end": v(-5.28, -18.84) * mm});
            skLineSegment(sketch, "E2.9.9.3", {"start": v(-9.9, -14.22) * mm, "end": v(-9.9, -18.84) * mm});
            skLineSegment(sketch, "E2.9.10.0", {"start": v(-9.9, -26.92) * mm, "end": v(-5.28, -26.92) * mm});
            skLineSegment(sketch, "E2.9.10.1", {"start": v(-5.28, -26.92) * mm, "end": v(-5.28, -31.54) * mm});
            skLineSegment(sketch, "E2.9.10.2", {"start": v(-9.9, -31.54) * mm, "end": v(-5.28, -31.54) * mm});
            skLineSegment(sketch, "E2.9.10.3", {"start": v(-9.9, -26.92) * mm, "end": v(-9.9, -31.54) * mm});
            skLineSegment(sketch, "E2.9.11.0", {"start": v(-9.9, -39.62) * mm, "end": v(-5.28, -39.62) * mm});
            skLineSegment(sketch, "E2.9.11.1", {"start": v(-5.28, -39.62) * mm, "end": v(-5.28, -44.24) * mm});
            skLineSegment(sketch, "E2.9.11.2", {"start": v(-9.9, -44.24) * mm, "end": v(-5.28, -44.24) * mm});
            skLineSegment(sketch, "E2.9.11.3", {"start": v(-9.9, -39.62) * mm, "end": v(-9.9, -44.24) * mm});
            skLineSegment(sketch, "E2.9.12.0", {"start": v(-9.9, -52.32) * mm, "end": v(-5.28, -52.32) * mm});
            skLineSegment(sketch, "E2.9.12.1", {"start": v(-5.28, -52.32) * mm, "end": v(-5.28, -56.94) * mm});
            skLineSegment(sketch, "E2.9.12.2", {"start": v(-9.9, -56.94) * mm, "end": v(-5.28, -56.94) * mm});
            skLineSegment(sketch, "E2.9.12.3", {"start": v(-9.9, -52.32) * mm, "end": v(-9.9, -56.94) * mm});
            skLineSegment(sketch, "E2.9.13.0", {"start": v(-9.9, -65.02) * mm, "end": v(-5.28, -65.02) * mm});
            skLineSegment(sketch, "E2.9.13.1", {"start": v(-5.28, -65.02) * mm, "end": v(-5.28, -69.64) * mm});
            skLineSegment(sketch, "E2.9.13.2", {"start": v(-9.9, -69.64) * mm, "end": v(-5.28, -69.64) * mm});
            skLineSegment(sketch, "E2.9.13.3", {"start": v(-9.9, -65.02) * mm, "end": v(-9.9, -69.64) * mm});
            skLineSegment(sketch, "E2.10.0.0", {"start": v(2.8, 100.08) * mm, "end": v(7.42, 100.08) * mm});
            skLineSegment(sketch, "E2.10.0.1", {"start": v(7.42, 100.08) * mm, "end": v(7.42, 95.46) * mm});
            skLineSegment(sketch, "E2.10.0.2", {"start": v(2.8, 95.46) * mm, "end": v(7.42, 95.46) * mm});
            skLineSegment(sketch, "E2.10.0.3", {"start": v(2.8, 100.08) * mm, "end": v(2.8, 95.46) * mm});
            skLineSegment(sketch, "E2.10.1.0", {"start": v(2.8, 87.38) * mm, "end": v(7.42, 87.38) * mm});
            skLineSegment(sketch, "E2.10.1.1", {"start": v(7.42, 87.38) * mm, "end": v(7.42, 82.76) * mm});
            skLineSegment(sketch, "E2.10.1.2", {"start": v(2.8, 82.76) * mm, "end": v(7.42, 82.76) * mm});
            skLineSegment(sketch, "E2.10.1.3", {"start": v(2.8, 87.38) * mm, "end": v(2.8, 82.76) * mm});
            skLineSegment(sketch, "E2.10.2.0", {"start": v(2.8, 74.68) * mm, "end": v(7.42, 74.68) * mm});
            skLineSegment(sketch, "E2.10.2.1", {"start": v(7.42, 74.68) * mm, "end": v(7.42, 70.06) * mm});
            skLineSegment(sketch, "E2.10.2.2", {"start": v(2.8, 70.06) * mm, "end": v(7.42, 70.06) * mm});
            skLineSegment(sketch, "E2.10.2.3", {"start": v(2.8, 74.68) * mm, "end": v(2.8, 70.06) * mm});
            skLineSegment(sketch, "E2.10.3.0", {"start": v(2.8, 61.98) * mm, "end": v(7.42, 61.98) * mm});
            skLineSegment(sketch, "E2.10.3.1", {"start": v(7.42, 61.98) * mm, "end": v(7.42, 57.36) * mm});
            skLineSegment(sketch, "E2.10.3.2", {"start": v(2.8, 57.36) * mm, "end": v(7.42, 57.36) * mm});
            skLineSegment(sketch, "E2.10.3.3", {"start": v(2.8, 61.98) * mm, "end": v(2.8, 57.36) * mm});
            skLineSegment(sketch, "E2.10.4.0", {"start": v(2.8, 49.28) * mm, "end": v(7.42, 49.28) * mm});
            skLineSegment(sketch, "E2.10.4.1", {"start": v(7.42, 49.28) * mm, "end": v(7.42, 44.66) * mm});
            skLineSegment(sketch, "E2.10.4.2", {"start": v(2.8, 44.66) * mm, "end": v(7.42, 44.66) * mm});
            skLineSegment(sketch, "E2.10.4.3", {"start": v(2.8, 49.28) * mm, "end": v(2.8, 44.66) * mm});
            skLineSegment(sketch, "E2.10.5.0", {"start": v(2.8, 36.58) * mm, "end": v(7.42, 36.58) * mm});
            skLineSegment(sketch, "E2.10.5.1", {"start": v(7.42, 36.58) * mm, "end": v(7.42, 31.96) * mm});
            skLineSegment(sketch, "E2.10.5.2", {"start": v(2.8, 31.96) * mm, "end": v(7.42, 31.96) * mm});
            skLineSegment(sketch, "E2.10.5.3", {"start": v(2.8, 36.58) * mm, "end": v(2.8, 31.96) * mm});
            skLineSegment(sketch, "E2.10.6.0", {"start": v(2.8, 23.88) * mm, "end": v(7.42, 23.88) * mm});
            skLineSegment(sketch, "E2.10.6.1", {"start": v(7.42, 23.88) * mm, "end": v(7.42, 19.26) * mm});
            skLineSegment(sketch, "E2.10.6.2", {"start": v(2.8, 19.26) * mm, "end": v(7.42, 19.26) * mm});
            skLineSegment(sketch, "E2.10.6.3", {"start": v(2.8, 23.88) * mm, "end": v(2.8, 19.26) * mm});
            skLineSegment(sketch, "E2.10.7.0", {"start": v(2.8, 11.18) * mm, "end": v(7.42, 11.18) * mm});
            skLineSegment(sketch, "E2.10.7.1", {"start": v(7.42, 11.18) * mm, "end": v(7.42, 6.56) * mm});
            skLineSegment(sketch, "E2.10.7.2", {"start": v(2.8, 6.56) * mm, "end": v(7.42, 6.56) * mm});
            skLineSegment(sketch, "E2.10.7.3", {"start": v(2.8, 11.18) * mm, "end": v(2.8, 6.56) * mm});
            skLineSegment(sketch, "E2.10.8.0", {"start": v(2.8, -1.52) * mm, "end": v(7.42, -1.52) * mm});
            skLineSegment(sketch, "E2.10.8.1", {"start": v(7.42, -1.52) * mm, "end": v(7.42, -6.14) * mm});
            skLineSegment(sketch, "E2.10.8.2", {"start": v(2.8, -6.14) * mm, "end": v(7.42, -6.14) * mm});
            skLineSegment(sketch, "E2.10.8.3", {"start": v(2.8, -1.52) * mm, "end": v(2.8, -6.14) * mm});
            skLineSegment(sketch, "E2.10.9.0", {"start": v(2.8, -14.22) * mm, "end": v(7.42, -14.22) * mm});
            skLineSegment(sketch, "E2.10.9.1", {"start": v(7.42, -14.22) * mm, "end": v(7.42, -18.84) * mm});
            skLineSegment(sketch, "E2.10.9.2", {"start": v(2.8, -18.84) * mm, "end": v(7.42, -18.84) * mm});
            skLineSegment(sketch, "E2.10.9.3", {"start": v(2.8, -14.22) * mm, "end": v(2.8, -18.84) * mm});
            skLineSegment(sketch, "E2.10.10.0", {"start": v(2.8, -26.92) * mm, "end": v(7.42, -26.92) * mm});
            skLineSegment(sketch, "E2.10.10.1", {"start": v(7.42, -26.92) * mm, "end": v(7.42, -31.54) * mm});
            skLineSegment(sketch, "E2.10.10.2", {"start": v(2.8, -31.54) * mm, "end": v(7.42, -31.54) * mm});
            skLineSegment(sketch, "E2.10.10.3", {"start": v(2.8, -26.92) * mm, "end": v(2.8, -31.54) * mm});
            skLineSegment(sketch, "E2.10.11.0", {"start": v(2.8, -39.62) * mm, "end": v(7.42, -39.62) * mm});
            skLineSegment(sketch, "E2.10.11.1", {"start": v(7.42, -39.62) * mm, "end": v(7.42, -44.24) * mm});
            skLineSegment(sketch, "E2.10.11.2", {"start": v(2.8, -44.24) * mm, "end": v(7.42, -44.24) * mm});
            skLineSegment(sketch, "E2.10.11.3", {"start": v(2.8, -39.62) * mm, "end": v(2.8, -44.24) * mm});
            skLineSegment(sketch, "E2.10.12.0", {"start": v(2.8, -52.32) * mm, "end": v(7.42, -52.32) * mm});
            skLineSegment(sketch, "E2.10.12.1", {"start": v(7.42, -52.32) * mm, "end": v(7.42, -56.94) * mm});
            skLineSegment(sketch, "E2.10.12.2", {"start": v(2.8, -56.94) * mm, "end": v(7.42, -56.94) * mm});
            skLineSegment(sketch, "E2.10.12.3", {"start": v(2.8, -52.32) * mm, "end": v(2.8, -56.94) * mm});
            skLineSegment(sketch, "E2.10.13.0", {"start": v(2.8, -65.02) * mm, "end": v(7.42, -65.02) * mm});
            skLineSegment(sketch, "E2.10.13.1", {"start": v(7.42, -65.02) * mm, "end": v(7.42, -69.64) * mm});
            skLineSegment(sketch, "E2.10.13.2", {"start": v(2.8, -69.64) * mm, "end": v(7.42, -69.64) * mm});
            skLineSegment(sketch, "E2.10.13.3", {"start": v(2.8, -65.02) * mm, "end": v(2.8, -69.64) * mm});
            skLineSegment(sketch, "E2.11.0.0", {"start": v(15.5, 100.08) * mm, "end": v(20.12, 100.08) * mm});
            skLineSegment(sketch, "E2.11.0.1", {"start": v(20.12, 100.08) * mm, "end": v(20.12, 95.46) * mm});
            skLineSegment(sketch, "E2.11.0.2", {"start": v(15.5, 95.46) * mm, "end": v(20.12, 95.46) * mm});
            skLineSegment(sketch, "E2.11.0.3", {"start": v(15.5, 100.08) * mm, "end": v(15.5, 95.46) * mm});
            skLineSegment(sketch, "E2.11.1.0", {"start": v(15.5, 87.38) * mm, "end": v(20.12, 87.38) * mm});
            skLineSegment(sketch, "E2.11.1.1", {"start": v(20.12, 87.38) * mm, "end": v(20.12, 82.76) * mm});
            skLineSegment(sketch, "E2.11.1.2", {"start": v(15.5, 82.76) * mm, "end": v(20.12, 82.76) * mm});
            skLineSegment(sketch, "E2.11.1.3", {"start": v(15.5, 87.38) * mm, "end": v(15.5, 82.76) * mm});
            skLineSegment(sketch, "E2.11.2.0", {"start": v(15.5, 74.68) * mm, "end": v(20.12, 74.68) * mm});
            skLineSegment(sketch, "E2.11.2.1", {"start": v(20.12, 74.68) * mm, "end": v(20.12, 70.06) * mm});
            skLineSegment(sketch, "E2.11.2.2", {"start": v(15.5, 70.06) * mm, "end": v(20.12, 70.06) * mm});
            skLineSegment(sketch, "E2.11.2.3", {"start": v(15.5, 74.68) * mm, "end": v(15.5, 70.06) * mm});
            skLineSegment(sketch, "E2.11.3.0", {"start": v(15.5, 61.98) * mm, "end": v(20.12, 61.98) * mm});
            skLineSegment(sketch, "E2.11.3.1", {"start": v(20.12, 61.98) * mm, "end": v(20.12, 57.36) * mm});
            skLineSegment(sketch, "E2.11.3.2", {"start": v(15.5, 57.36) * mm, "end": v(20.12, 57.36) * mm});
            skLineSegment(sketch, "E2.11.3.3", {"start": v(15.5, 61.98) * mm, "end": v(15.5, 57.36) * mm});
            skLineSegment(sketch, "E2.11.4.0", {"start": v(15.5, 49.28) * mm, "end": v(20.12, 49.28) * mm});
            skLineSegment(sketch, "E2.11.4.1", {"start": v(20.12, 49.28) * mm, "end": v(20.12, 44.66) * mm});
            skLineSegment(sketch, "E2.11.4.2", {"start": v(15.5, 44.66) * mm, "end": v(20.12, 44.66) * mm});
            skLineSegment(sketch, "E2.11.4.3", {"start": v(15.5, 49.28) * mm, "end": v(15.5, 44.66) * mm});
            skLineSegment(sketch, "E2.11.5.0", {"start": v(15.5, 36.58) * mm, "end": v(20.12, 36.58) * mm});
            skLineSegment(sketch, "E2.11.5.1", {"start": v(20.12, 36.58) * mm, "end": v(20.12, 31.96) * mm});
            skLineSegment(sketch, "E2.11.5.2", {"start": v(15.5, 31.96) * mm, "end": v(20.12, 31.96) * mm});
            skLineSegment(sketch, "E2.11.5.3", {"start": v(15.5, 36.58) * mm, "end": v(15.5, 31.96) * mm});
            skLineSegment(sketch, "E2.11.6.0", {"start": v(15.5, 23.88) * mm, "end": v(20.12, 23.88) * mm});
            skLineSegment(sketch, "E2.11.6.1", {"start": v(20.12, 23.88) * mm, "end": v(20.12, 19.26) * mm});
            skLineSegment(sketch, "E2.11.6.2", {"start": v(15.5, 19.26) * mm, "end": v(20.12, 19.26) * mm});
            skLineSegment(sketch, "E2.11.6.3", {"start": v(15.5, 23.88) * mm, "end": v(15.5, 19.26) * mm});
            skLineSegment(sketch, "E2.11.7.0", {"start": v(15.5, 11.18) * mm, "end": v(20.12, 11.18) * mm});
            skLineSegment(sketch, "E2.11.7.1", {"start": v(20.12, 11.18) * mm, "end": v(20.12, 6.56) * mm});
            skLineSegment(sketch, "E2.11.7.2", {"start": v(15.5, 6.56) * mm, "end": v(20.12, 6.56) * mm});
            skLineSegment(sketch, "E2.11.7.3", {"start": v(15.5, 11.18) * mm, "end": v(15.5, 6.56) * mm});
            skLineSegment(sketch, "E2.11.8.0", {"start": v(15.5, -1.52) * mm, "end": v(20.12, -1.52) * mm});
            skLineSegment(sketch, "E2.11.8.1", {"start": v(20.12, -1.52) * mm, "end": v(20.12, -6.14) * mm});
            skLineSegment(sketch, "E2.11.8.2", {"start": v(15.5, -6.14) * mm, "end": v(20.12, -6.14) * mm});
            skLineSegment(sketch, "E2.11.8.3", {"start": v(15.5, -1.52) * mm, "end": v(15.5, -6.14) * mm});
            skLineSegment(sketch, "E2.11.9.0", {"start": v(15.5, -14.22) * mm, "end": v(20.12, -14.22) * mm});
            skLineSegment(sketch, "E2.11.9.1", {"start": v(20.12, -14.22) * mm, "end": v(20.12, -18.84) * mm});
            skLineSegment(sketch, "E2.11.9.2", {"start": v(15.5, -18.84) * mm, "end": v(20.12, -18.84) * mm});
            skLineSegment(sketch, "E2.11.9.3", {"start": v(15.5, -14.22) * mm, "end": v(15.5, -18.84) * mm});
            skLineSegment(sketch, "E2.11.10.0", {"start": v(15.5, -26.92) * mm, "end": v(20.12, -26.92) * mm});
            skLineSegment(sketch, "E2.11.10.1", {"start": v(20.12, -26.92) * mm, "end": v(20.12, -31.54) * mm});
            skLineSegment(sketch, "E2.11.10.2", {"start": v(15.5, -31.54) * mm, "end": v(20.12, -31.54) * mm});
            skLineSegment(sketch, "E2.11.10.3", {"start": v(15.5, -26.92) * mm, "end": v(15.5, -31.54) * mm});
            skLineSegment(sketch, "E2.11.11.0", {"start": v(15.5, -39.62) * mm, "end": v(20.12, -39.62) * mm});
            skLineSegment(sketch, "E2.11.11.1", {"start": v(20.12, -39.62) * mm, "end": v(20.12, -44.24) * mm});
            skLineSegment(sketch, "E2.11.11.2", {"start": v(15.5, -44.24) * mm, "end": v(20.12, -44.24) * mm});
            skLineSegment(sketch, "E2.11.11.3", {"start": v(15.5, -39.62) * mm, "end": v(15.5, -44.24) * mm});
            skLineSegment(sketch, "E2.11.12.0", {"start": v(15.5, -52.32) * mm, "end": v(20.12, -52.32) * mm});
            skLineSegment(sketch, "E2.11.12.1", {"start": v(20.12, -52.32) * mm, "end": v(20.12, -56.94) * mm});
            skLineSegment(sketch, "E2.11.12.2", {"start": v(15.5, -56.94) * mm, "end": v(20.12, -56.94) * mm});
            skLineSegment(sketch, "E2.11.12.3", {"start": v(15.5, -52.32) * mm, "end": v(15.5, -56.94) * mm});
            skLineSegment(sketch, "E2.11.13.0", {"start": v(15.5, -65.02) * mm, "end": v(20.12, -65.02) * mm});
            skLineSegment(sketch, "E2.11.13.1", {"start": v(20.12, -65.02) * mm, "end": v(20.12, -69.64) * mm});
            skLineSegment(sketch, "E2.11.13.2", {"start": v(15.5, -69.64) * mm, "end": v(20.12, -69.64) * mm});
            skLineSegment(sketch, "E2.11.13.3", {"start": v(15.5, -65.02) * mm, "end": v(15.5, -69.64) * mm});
            skLineSegment(sketch, "E2.12.0.0", {"start": v(28.2, 100.08) * mm, "end": v(32.82, 100.08) * mm});
            skLineSegment(sketch, "E2.12.0.1", {"start": v(32.82, 100.08) * mm, "end": v(32.82, 95.46) * mm});
            skLineSegment(sketch, "E2.12.0.2", {"start": v(28.2, 95.46) * mm, "end": v(32.82, 95.46) * mm});
            skLineSegment(sketch, "E2.12.0.3", {"start": v(28.2, 100.08) * mm, "end": v(28.2, 95.46) * mm});
            skLineSegment(sketch, "E2.12.1.0", {"start": v(28.2, 87.38) * mm, "end": v(32.82, 87.38) * mm});
            skLineSegment(sketch, "E2.12.1.1", {"start": v(32.82, 87.38) * mm, "end": v(32.82, 82.76) * mm});
            skLineSegment(sketch, "E2.12.1.2", {"start": v(28.2, 82.76) * mm, "end": v(32.82, 82.76) * mm});
            skLineSegment(sketch, "E2.12.1.3", {"start": v(28.2, 87.38) * mm, "end": v(28.2, 82.76) * mm});
            skLineSegment(sketch, "E2.12.2.0", {"start": v(28.2, 74.68) * mm, "end": v(32.82, 74.68) * mm});
            skLineSegment(sketch, "E2.12.2.1", {"start": v(32.82, 74.68) * mm, "end": v(32.82, 70.06) * mm});
            skLineSegment(sketch, "E2.12.2.2", {"start": v(28.2, 70.06) * mm, "end": v(32.82, 70.06) * mm});
            skLineSegment(sketch, "E2.12.2.3", {"start": v(28.2, 74.68) * mm, "end": v(28.2, 70.06) * mm});
            skLineSegment(sketch, "E2.12.3.0", {"start": v(28.2, 61.98) * mm, "end": v(32.82, 61.98) * mm});
            skLineSegment(sketch, "E2.12.3.1", {"start": v(32.82, 61.98) * mm, "end": v(32.82, 57.36) * mm});
            skLineSegment(sketch, "E2.12.3.2", {"start": v(28.2, 57.36) * mm, "end": v(32.82, 57.36) * mm});
            skLineSegment(sketch, "E2.12.3.3", {"start": v(28.2, 61.98) * mm, "end": v(28.2, 57.36) * mm});
            skLineSegment(sketch, "E2.12.4.0", {"start": v(28.2, 49.28) * mm, "end": v(32.82, 49.28) * mm});
            skLineSegment(sketch, "E2.12.4.1", {"start": v(32.82, 49.28) * mm, "end": v(32.82, 44.66) * mm});
            skLineSegment(sketch, "E2.12.4.2", {"start": v(28.2, 44.66) * mm, "end": v(32.82, 44.66) * mm});
            skLineSegment(sketch, "E2.12.4.3", {"start": v(28.2, 49.28) * mm, "end": v(28.2, 44.66) * mm});
            skLineSegment(sketch, "E2.12.5.0", {"start": v(28.2, 36.58) * mm, "end": v(32.82, 36.58) * mm});
            skLineSegment(sketch, "E2.12.5.1", {"start": v(32.82, 36.58) * mm, "end": v(32.82, 31.96) * mm});
            skLineSegment(sketch, "E2.12.5.2", {"start": v(28.2, 31.96) * mm, "end": v(32.82, 31.96) * mm});
            skLineSegment(sketch, "E2.12.5.3", {"start": v(28.2, 36.58) * mm, "end": v(28.2, 31.96) * mm});
            skLineSegment(sketch, "E2.12.6.0", {"start": v(28.2, 23.88) * mm, "end": v(32.82, 23.88) * mm});
            skLineSegment(sketch, "E2.12.6.1", {"start": v(32.82, 23.88) * mm, "end": v(32.82, 19.26) * mm});
            skLineSegment(sketch, "E2.12.6.2", {"start": v(28.2, 19.26) * mm, "end": v(32.82, 19.26) * mm});
            skLineSegment(sketch, "E2.12.6.3", {"start": v(28.2, 23.88) * mm, "end": v(28.2, 19.26) * mm});
            skLineSegment(sketch, "E2.12.7.0", {"start": v(28.2, 11.18) * mm, "end": v(32.82, 11.18) * mm});
            skLineSegment(sketch, "E2.12.7.1", {"start": v(32.82, 11.18) * mm, "end": v(32.82, 6.56) * mm});
            skLineSegment(sketch, "E2.12.7.2", {"start": v(28.2, 6.56) * mm, "end": v(32.82, 6.56) * mm});
            skLineSegment(sketch, "E2.12.7.3", {"start": v(28.2, 11.18) * mm, "end": v(28.2, 6.56) * mm});
            skLineSegment(sketch, "E2.12.8.0", {"start": v(28.2, -1.52) * mm, "end": v(32.82, -1.52) * mm});
            skLineSegment(sketch, "E2.12.8.1", {"start": v(32.82, -1.52) * mm, "end": v(32.82, -6.14) * mm});
            skLineSegment(sketch, "E2.12.8.2", {"start": v(28.2, -6.14) * mm, "end": v(32.82, -6.14) * mm});
            skLineSegment(sketch, "E2.12.8.3", {"start": v(28.2, -1.52) * mm, "end": v(28.2, -6.14) * mm});
            skLineSegment(sketch, "E2.12.9.0", {"start": v(28.2, -14.22) * mm, "end": v(32.82, -14.22) * mm});
            skLineSegment(sketch, "E2.12.9.1", {"start": v(32.82, -14.22) * mm, "end": v(32.82, -18.84) * mm});
            skLineSegment(sketch, "E2.12.9.2", {"start": v(28.2, -18.84) * mm, "end": v(32.82, -18.84) * mm});
            skLineSegment(sketch, "E2.12.9.3", {"start": v(28.2, -14.22) * mm, "end": v(28.2, -18.84) * mm});
            skLineSegment(sketch, "E2.12.10.0", {"start": v(28.2, -26.92) * mm, "end": v(32.82, -26.92) * mm});
            skLineSegment(sketch, "E2.12.10.1", {"start": v(32.82, -26.92) * mm, "end": v(32.82, -31.54) * mm});
            skLineSegment(sketch, "E2.12.10.2", {"start": v(28.2, -31.54) * mm, "end": v(32.82, -31.54) * mm});
            skLineSegment(sketch, "E2.12.10.3", {"start": v(28.2, -26.92) * mm, "end": v(28.2, -31.54) * mm});
            skLineSegment(sketch, "E2.12.11.0", {"start": v(28.2, -39.62) * mm, "end": v(32.82, -39.62) * mm});
            skLineSegment(sketch, "E2.12.11.1", {"start": v(32.82, -39.62) * mm, "end": v(32.82, -44.24) * mm});
            skLineSegment(sketch, "E2.12.11.2", {"start": v(28.2, -44.24) * mm, "end": v(32.82, -44.24) * mm});
            skLineSegment(sketch, "E2.12.11.3", {"start": v(28.2, -39.62) * mm, "end": v(28.2, -44.24) * mm});
            skLineSegment(sketch, "E2.12.12.0", {"start": v(28.2, -52.32) * mm, "end": v(32.82, -52.32) * mm});
            skLineSegment(sketch, "E2.12.12.1", {"start": v(32.82, -52.32) * mm, "end": v(32.82, -56.94) * mm});
            skLineSegment(sketch, "E2.12.12.2", {"start": v(28.2, -56.94) * mm, "end": v(32.82, -56.94) * mm});
            skLineSegment(sketch, "E2.12.12.3", {"start": v(28.2, -52.32) * mm, "end": v(28.2, -56.94) * mm});
            skLineSegment(sketch, "E2.12.13.0", {"start": v(28.2, -65.02) * mm, "end": v(32.82, -65.02) * mm});
            skLineSegment(sketch, "E2.12.13.1", {"start": v(32.82, -65.02) * mm, "end": v(32.82, -69.64) * mm});
            skLineSegment(sketch, "E2.12.13.2", {"start": v(28.2, -69.64) * mm, "end": v(32.82, -69.64) * mm});
            skLineSegment(sketch, "E2.12.13.3", {"start": v(28.2, -65.02) * mm, "end": v(28.2, -69.64) * mm});
            skLineSegment(sketch, "E2.13.0.0", {"start": v(40.9, 100.08) * mm, "end": v(45.52, 100.08) * mm});
            skLineSegment(sketch, "E2.13.0.1", {"start": v(45.52, 100.08) * mm, "end": v(45.52, 95.46) * mm});
            skLineSegment(sketch, "E2.13.0.2", {"start": v(40.9, 95.46) * mm, "end": v(45.52, 95.46) * mm});
            skLineSegment(sketch, "E2.13.0.3", {"start": v(40.9, 100.08) * mm, "end": v(40.9, 95.46) * mm});
            skLineSegment(sketch, "E2.13.1.0", {"start": v(40.9, 87.38) * mm, "end": v(45.52, 87.38) * mm});
            skLineSegment(sketch, "E2.13.1.1", {"start": v(45.52, 87.38) * mm, "end": v(45.52, 82.76) * mm});
            skLineSegment(sketch, "E2.13.1.2", {"start": v(40.9, 82.76) * mm, "end": v(45.52, 82.76) * mm});
            skLineSegment(sketch, "E2.13.1.3", {"start": v(40.9, 87.38) * mm, "end": v(40.9, 82.76) * mm});
            skLineSegment(sketch, "E2.13.2.0", {"start": v(40.9, 74.68) * mm, "end": v(45.52, 74.68) * mm});
            skLineSegment(sketch, "E2.13.2.1", {"start": v(45.52, 74.68) * mm, "end": v(45.52, 70.06) * mm});
            skLineSegment(sketch, "E2.13.2.2", {"start": v(40.9, 70.06) * mm, "end": v(45.52, 70.06) * mm});
            skLineSegment(sketch, "E2.13.2.3", {"start": v(40.9, 74.68) * mm, "end": v(40.9, 70.06) * mm});
            skLineSegment(sketch, "E2.13.3.0", {"start": v(40.9, 61.98) * mm, "end": v(45.52, 61.98) * mm});
            skLineSegment(sketch, "E2.13.3.1", {"start": v(45.52, 61.98) * mm, "end": v(45.52, 57.36) * mm});
            skLineSegment(sketch, "E2.13.3.2", {"start": v(40.9, 57.36) * mm, "end": v(45.52, 57.36) * mm});
            skLineSegment(sketch, "E2.13.3.3", {"start": v(40.9, 61.98) * mm, "end": v(40.9, 57.36) * mm});
            skLineSegment(sketch, "E2.13.4.0", {"start": v(40.9, 49.28) * mm, "end": v(45.52, 49.28) * mm});
            skLineSegment(sketch, "E2.13.4.1", {"start": v(45.52, 49.28) * mm, "end": v(45.52, 44.66) * mm});
            skLineSegment(sketch, "E2.13.4.2", {"start": v(40.9, 44.66) * mm, "end": v(45.52, 44.66) * mm});
            skLineSegment(sketch, "E2.13.4.3", {"start": v(40.9, 49.28) * mm, "end": v(40.9, 44.66) * mm});
            skLineSegment(sketch, "E2.13.5.0", {"start": v(40.9, 36.58) * mm, "end": v(45.52, 36.58) * mm});
            skLineSegment(sketch, "E2.13.5.1", {"start": v(45.52, 36.58) * mm, "end": v(45.52, 31.96) * mm});
            skLineSegment(sketch, "E2.13.5.2", {"start": v(40.9, 31.96) * mm, "end": v(45.52, 31.96) * mm});
            skLineSegment(sketch, "E2.13.5.3", {"start": v(40.9, 36.58) * mm, "end": v(40.9, 31.96) * mm});
            skLineSegment(sketch, "E2.13.6.0", {"start": v(40.9, 23.88) * mm, "end": v(45.52, 23.88) * mm});
            skLineSegment(sketch, "E2.13.6.1", {"start": v(45.52, 23.88) * mm, "end": v(45.52, 19.26) * mm});
            skLineSegment(sketch, "E2.13.6.2", {"start": v(40.9, 19.26) * mm, "end": v(45.52, 19.26) * mm});
            skLineSegment(sketch, "E2.13.6.3", {"start": v(40.9, 23.88) * mm, "end": v(40.9, 19.26) * mm});
            skLineSegment(sketch, "E2.13.7.0", {"start": v(40.9, 11.18) * mm, "end": v(45.52, 11.18) * mm});
            skLineSegment(sketch, "E2.13.7.1", {"start": v(45.52, 11.18) * mm, "end": v(45.52, 6.56) * mm});
            skLineSegment(sketch, "E2.13.7.2", {"start": v(40.9, 6.56) * mm, "end": v(45.52, 6.56) * mm});
            skLineSegment(sketch, "E2.13.7.3", {"start": v(40.9, 11.18) * mm, "end": v(40.9, 6.56) * mm});
            skLineSegment(sketch, "E2.13.8.0", {"start": v(40.9, -1.52) * mm, "end": v(45.52, -1.52) * mm});
            skLineSegment(sketch, "E2.13.8.1", {"start": v(45.52, -1.52) * mm, "end": v(45.52, -6.14) * mm});
            skLineSegment(sketch, "E2.13.8.2", {"start": v(40.9, -6.14) * mm, "end": v(45.52, -6.14) * mm});
            skLineSegment(sketch, "E2.13.8.3", {"start": v(40.9, -1.52) * mm, "end": v(40.9, -6.14) * mm});
            skLineSegment(sketch, "E2.13.9.0", {"start": v(40.9, -14.22) * mm, "end": v(45.52, -14.22) * mm});
            skLineSegment(sketch, "E2.13.9.1", {"start": v(45.52, -14.22) * mm, "end": v(45.52, -18.84) * mm});
            skLineSegment(sketch, "E2.13.9.2", {"start": v(40.9, -18.84) * mm, "end": v(45.52, -18.84) * mm});
            skLineSegment(sketch, "E2.13.9.3", {"start": v(40.9, -14.22) * mm, "end": v(40.9, -18.84) * mm});
            skLineSegment(sketch, "E2.13.10.0", {"start": v(40.9, -26.92) * mm, "end": v(45.52, -26.92) * mm});
            skLineSegment(sketch, "E2.13.10.1", {"start": v(45.52, -26.92) * mm, "end": v(45.52, -31.54) * mm});
            skLineSegment(sketch, "E2.13.10.2", {"start": v(40.9, -31.54) * mm, "end": v(45.52, -31.54) * mm});
            skLineSegment(sketch, "E2.13.10.3", {"start": v(40.9, -26.92) * mm, "end": v(40.9, -31.54) * mm});
            skLineSegment(sketch, "E2.13.11.0", {"start": v(40.9, -39.62) * mm, "end": v(45.52, -39.62) * mm});
            skLineSegment(sketch, "E2.13.11.1", {"start": v(45.52, -39.62) * mm, "end": v(45.52, -44.24) * mm});
            skLineSegment(sketch, "E2.13.11.2", {"start": v(40.9, -44.24) * mm, "end": v(45.52, -44.24) * mm});
            skLineSegment(sketch, "E2.13.11.3", {"start": v(40.9, -39.62) * mm, "end": v(40.9, -44.24) * mm});
            skLineSegment(sketch, "E2.13.12.0", {"start": v(40.9, -52.32) * mm, "end": v(45.52, -52.32) * mm});
            skLineSegment(sketch, "E2.13.12.1", {"start": v(45.52, -52.32) * mm, "end": v(45.52, -56.94) * mm});
            skLineSegment(sketch, "E2.13.12.2", {"start": v(40.9, -56.94) * mm, "end": v(45.52, -56.94) * mm});
            skLineSegment(sketch, "E2.13.12.3", {"start": v(40.9, -52.32) * mm, "end": v(40.9, -56.94) * mm});
            skLineSegment(sketch, "E2.13.13.0", {"start": v(40.9, -65.02) * mm, "end": v(45.52, -65.02) * mm});
            skLineSegment(sketch, "E2.13.13.1", {"start": v(45.52, -65.02) * mm, "end": v(45.52, -69.64) * mm});
            skLineSegment(sketch, "E2.13.13.2", {"start": v(40.9, -69.64) * mm, "end": v(45.52, -69.64) * mm});
            skLineSegment(sketch, "E2.13.13.3", {"start": v(40.9, -65.02) * mm, "end": v(40.9, -69.64) * mm});
            skLineSegment(sketch, "E2.14.0.0", {"start": v(53.6, 100.08) * mm, "end": v(58.22, 100.08) * mm});
            skLineSegment(sketch, "E2.14.0.1", {"start": v(58.22, 100.08) * mm, "end": v(58.22, 95.46) * mm});
            skLineSegment(sketch, "E2.14.0.2", {"start": v(53.6, 95.46) * mm, "end": v(58.22, 95.46) * mm});
            skLineSegment(sketch, "E2.14.0.3", {"start": v(53.6, 100.08) * mm, "end": v(53.6, 95.46) * mm});
            skLineSegment(sketch, "E2.14.1.0", {"start": v(53.6, 87.38) * mm, "end": v(58.22, 87.38) * mm});
            skLineSegment(sketch, "E2.14.1.1", {"start": v(58.22, 87.38) * mm, "end": v(58.22, 82.76) * mm});
            skLineSegment(sketch, "E2.14.1.2", {"start": v(53.6, 82.76) * mm, "end": v(58.22, 82.76) * mm});
            skLineSegment(sketch, "E2.14.1.3", {"start": v(53.6, 87.38) * mm, "end": v(53.6, 82.76) * mm});
            skLineSegment(sketch, "E2.14.2.0", {"start": v(53.6, 74.68) * mm, "end": v(58.22, 74.68) * mm});
            skLineSegment(sketch, "E2.14.2.1", {"start": v(58.22, 74.68) * mm, "end": v(58.22, 70.06) * mm});
            skLineSegment(sketch, "E2.14.2.2", {"start": v(53.6, 70.06) * mm, "end": v(58.22, 70.06) * mm});
            skLineSegment(sketch, "E2.14.2.3", {"start": v(53.6, 74.68) * mm, "end": v(53.6, 70.06) * mm});
            skLineSegment(sketch, "E2.14.3.0", {"start": v(53.6, 61.98) * mm, "end": v(58.22, 61.98) * mm});
            skLineSegment(sketch, "E2.14.3.1", {"start": v(58.22, 61.98) * mm, "end": v(58.22, 57.36) * mm});
            skLineSegment(sketch, "E2.14.3.2", {"start": v(53.6, 57.36) * mm, "end": v(58.22, 57.36) * mm});
            skLineSegment(sketch, "E2.14.3.3", {"start": v(53.6, 61.98) * mm, "end": v(53.6, 57.36) * mm});
            skLineSegment(sketch, "E2.14.4.0", {"start": v(53.6, 49.28) * mm, "end": v(58.22, 49.28) * mm});
            skLineSegment(sketch, "E2.14.4.1", {"start": v(58.22, 49.28) * mm, "end": v(58.22, 44.66) * mm});
            skLineSegment(sketch, "E2.14.4.2", {"start": v(53.6, 44.66) * mm, "end": v(58.22, 44.66) * mm});
            skLineSegment(sketch, "E2.14.4.3", {"start": v(53.6, 49.28) * mm, "end": v(53.6, 44.66) * mm});
            skLineSegment(sketch, "E2.14.5.0", {"start": v(53.6, 36.58) * mm, "end": v(58.22, 36.58) * mm});
            skLineSegment(sketch, "E2.14.5.1", {"start": v(58.22, 36.58) * mm, "end": v(58.22, 31.96) * mm});
            skLineSegment(sketch, "E2.14.5.2", {"start": v(53.6, 31.96) * mm, "end": v(58.22, 31.96) * mm});
            skLineSegment(sketch, "E2.14.5.3", {"start": v(53.6, 36.58) * mm, "end": v(53.6, 31.96) * mm});
            skLineSegment(sketch, "E2.14.6.0", {"start": v(53.6, 23.88) * mm, "end": v(58.22, 23.88) * mm});
            skLineSegment(sketch, "E2.14.6.1", {"start": v(58.22, 23.88) * mm, "end": v(58.22, 19.26) * mm});
            skLineSegment(sketch, "E2.14.6.2", {"start": v(53.6, 19.26) * mm, "end": v(58.22, 19.26) * mm});
            skLineSegment(sketch, "E2.14.6.3", {"start": v(53.6, 23.88) * mm, "end": v(53.6, 19.26) * mm});
            skLineSegment(sketch, "E2.14.7.0", {"start": v(53.6, 11.18) * mm, "end": v(58.22, 11.18) * mm});
            skLineSegment(sketch, "E2.14.7.1", {"start": v(58.22, 11.18) * mm, "end": v(58.22, 6.56) * mm});
            skLineSegment(sketch, "E2.14.7.2", {"start": v(53.6, 6.56) * mm, "end": v(58.22, 6.56) * mm});
            skLineSegment(sketch, "E2.14.7.3", {"start": v(53.6, 11.18) * mm, "end": v(53.6, 6.56) * mm});
            skLineSegment(sketch, "E2.14.8.0", {"start": v(53.6, -1.52) * mm, "end": v(58.22, -1.52) * mm});
            skLineSegment(sketch, "E2.14.8.1", {"start": v(58.22, -1.52) * mm, "end": v(58.22, -6.14) * mm});
            skLineSegment(sketch, "E2.14.8.2", {"start": v(53.6, -6.14) * mm, "end": v(58.22, -6.14) * mm});
            skLineSegment(sketch, "E2.14.8.3", {"start": v(53.6, -1.52) * mm, "end": v(53.6, -6.14) * mm});
            skLineSegment(sketch, "E2.14.9.0", {"start": v(53.6, -14.22) * mm, "end": v(58.22, -14.22) * mm});
            skLineSegment(sketch, "E2.14.9.1", {"start": v(58.22, -14.22) * mm, "end": v(58.22, -18.84) * mm});
            skLineSegment(sketch, "E2.14.9.2", {"start": v(53.6, -18.84) * mm, "end": v(58.22, -18.84) * mm});
            skLineSegment(sketch, "E2.14.9.3", {"start": v(53.6, -14.22) * mm, "end": v(53.6, -18.84) * mm});
            skLineSegment(sketch, "E2.14.10.0", {"start": v(53.6, -26.92) * mm, "end": v(58.22, -26.92) * mm});
            skLineSegment(sketch, "E2.14.10.1", {"start": v(58.22, -26.92) * mm, "end": v(58.22, -31.54) * mm});
            skLineSegment(sketch, "E2.14.10.2", {"start": v(53.6, -31.54) * mm, "end": v(58.22, -31.54) * mm});
            skLineSegment(sketch, "E2.14.10.3", {"start": v(53.6, -26.92) * mm, "end": v(53.6, -31.54) * mm});
            skLineSegment(sketch, "E2.14.11.0", {"start": v(53.6, -39.62) * mm, "end": v(58.22, -39.62) * mm});
            skLineSegment(sketch, "E2.14.11.1", {"start": v(58.22, -39.62) * mm, "end": v(58.22, -44.24) * mm});
            skLineSegment(sketch, "E2.14.11.2", {"start": v(53.6, -44.24) * mm, "end": v(58.22, -44.24) * mm});
            skLineSegment(sketch, "E2.14.11.3", {"start": v(53.6, -39.62) * mm, "end": v(53.6, -44.24) * mm});
            skLineSegment(sketch, "E2.14.12.0", {"start": v(53.6, -52.32) * mm, "end": v(58.22, -52.32) * mm});
            skLineSegment(sketch, "E2.14.12.1", {"start": v(58.22, -52.32) * mm, "end": v(58.22, -56.94) * mm});
            skLineSegment(sketch, "E2.14.12.2", {"start": v(53.6, -56.94) * mm, "end": v(58.22, -56.94) * mm});
            skLineSegment(sketch, "E2.14.12.3", {"start": v(53.6, -52.32) * mm, "end": v(53.6, -56.94) * mm});
            skLineSegment(sketch, "E2.14.13.0", {"start": v(53.6, -65.02) * mm, "end": v(58.22, -65.02) * mm});
            skLineSegment(sketch, "E2.14.13.1", {"start": v(58.22, -65.02) * mm, "end": v(58.22, -69.64) * mm});
            skLineSegment(sketch, "E2.14.13.2", {"start": v(53.6, -69.64) * mm, "end": v(58.22, -69.64) * mm});
            skLineSegment(sketch, "E2.14.13.3", {"start": v(53.6, -65.02) * mm, "end": v(53.6, -69.64) * mm});
            skLineSegment(sketch, "E2.15.0.0", {"start": v(66.3, 100.08) * mm, "end": v(70.92, 100.08) * mm});
            skLineSegment(sketch, "E2.15.0.1", {"start": v(70.92, 100.08) * mm, "end": v(70.92, 95.46) * mm});
            skLineSegment(sketch, "E2.15.0.2", {"start": v(66.3, 95.46) * mm, "end": v(70.92, 95.46) * mm});
            skLineSegment(sketch, "E2.15.0.3", {"start": v(66.3, 100.08) * mm, "end": v(66.3, 95.46) * mm});
            skLineSegment(sketch, "E2.15.1.0", {"start": v(66.3, 87.38) * mm, "end": v(70.92, 87.38) * mm});
            skLineSegment(sketch, "E2.15.1.1", {"start": v(70.92, 87.38) * mm, "end": v(70.92, 82.76) * mm});
            skLineSegment(sketch, "E2.15.1.2", {"start": v(66.3, 82.76) * mm, "end": v(70.92, 82.76) * mm});
            skLineSegment(sketch, "E2.15.1.3", {"start": v(66.3, 87.38) * mm, "end": v(66.3, 82.76) * mm});
            skLineSegment(sketch, "E2.15.2.0", {"start": v(66.3, 74.68) * mm, "end": v(70.92, 74.68) * mm});
            skLineSegment(sketch, "E2.15.2.1", {"start": v(70.92, 74.68) * mm, "end": v(70.92, 70.06) * mm});
            skLineSegment(sketch, "E2.15.2.2", {"start": v(66.3, 70.06) * mm, "end": v(70.92, 70.06) * mm});
            skLineSegment(sketch, "E2.15.2.3", {"start": v(66.3, 74.68) * mm, "end": v(66.3, 70.06) * mm});
            skLineSegment(sketch, "E2.15.3.0", {"start": v(66.3, 61.98) * mm, "end": v(70.92, 61.98) * mm});
            skLineSegment(sketch, "E2.15.3.1", {"start": v(70.92, 61.98) * mm, "end": v(70.92, 57.36) * mm});
            skLineSegment(sketch, "E2.15.3.2", {"start": v(66.3, 57.36) * mm, "end": v(70.92, 57.36) * mm});
            skLineSegment(sketch, "E2.15.3.3", {"start": v(66.3, 61.98) * mm, "end": v(66.3, 57.36) * mm});
            skLineSegment(sketch, "E2.15.4.0", {"start": v(66.3, 49.28) * mm, "end": v(70.92, 49.28) * mm});
            skLineSegment(sketch, "E2.15.4.1", {"start": v(70.92, 49.28) * mm, "end": v(70.92, 44.66) * mm});
            skLineSegment(sketch, "E2.15.4.2", {"start": v(66.3, 44.66) * mm, "end": v(70.92, 44.66) * mm});
            skLineSegment(sketch, "E2.15.4.3", {"start": v(66.3, 49.28) * mm, "end": v(66.3, 44.66) * mm});
            skLineSegment(sketch, "E2.15.5.0", {"start": v(66.3, 36.58) * mm, "end": v(70.92, 36.58) * mm});
            skLineSegment(sketch, "E2.15.5.1", {"start": v(70.92, 36.58) * mm, "end": v(70.92, 31.96) * mm});
            skLineSegment(sketch, "E2.15.5.2", {"start": v(66.3, 31.96) * mm, "end": v(70.92, 31.96) * mm});
            skLineSegment(sketch, "E2.15.5.3", {"start": v(66.3, 36.58) * mm, "end": v(66.3, 31.96) * mm});
            skLineSegment(sketch, "E2.15.6.0", {"start": v(66.3, 23.88) * mm, "end": v(70.92, 23.88) * mm});
            skLineSegment(sketch, "E2.15.6.1", {"start": v(70.92, 23.88) * mm, "end": v(70.92, 19.26) * mm});
            skLineSegment(sketch, "E2.15.6.2", {"start": v(66.3, 19.26) * mm, "end": v(70.92, 19.26) * mm});
            skLineSegment(sketch, "E2.15.6.3", {"start": v(66.3, 23.88) * mm, "end": v(66.3, 19.26) * mm});
            skLineSegment(sketch, "E2.15.7.0", {"start": v(66.3, 11.18) * mm, "end": v(70.92, 11.18) * mm});
            skLineSegment(sketch, "E2.15.7.1", {"start": v(70.92, 11.18) * mm, "end": v(70.92, 6.56) * mm});
            skLineSegment(sketch, "E2.15.7.2", {"start": v(66.3, 6.56) * mm, "end": v(70.92, 6.56) * mm});
            skLineSegment(sketch, "E2.15.7.3", {"start": v(66.3, 11.18) * mm, "end": v(66.3, 6.56) * mm});
            skLineSegment(sketch, "E2.15.8.0", {"start": v(66.3, -1.52) * mm, "end": v(70.92, -1.52) * mm});
            skLineSegment(sketch, "E2.15.8.1", {"start": v(70.92, -1.52) * mm, "end": v(70.92, -6.14) * mm});
            skLineSegment(sketch, "E2.15.8.2", {"start": v(66.3, -6.14) * mm, "end": v(70.92, -6.14) * mm});
            skLineSegment(sketch, "E2.15.8.3", {"start": v(66.3, -1.52) * mm, "end": v(66.3, -6.14) * mm});
            skLineSegment(sketch, "E2.15.9.0", {"start": v(66.3, -14.22) * mm, "end": v(70.92, -14.22) * mm});
            skLineSegment(sketch, "E2.15.9.1", {"start": v(70.92, -14.22) * mm, "end": v(70.92, -18.84) * mm});
            skLineSegment(sketch, "E2.15.9.2", {"start": v(66.3, -18.84) * mm, "end": v(70.92, -18.84) * mm});
            skLineSegment(sketch, "E2.15.9.3", {"start": v(66.3, -14.22) * mm, "end": v(66.3, -18.84) * mm});
            skLineSegment(sketch, "E2.15.10.0", {"start": v(66.3, -26.92) * mm, "end": v(70.92, -26.92) * mm});
            skLineSegment(sketch, "E2.15.10.1", {"start": v(70.92, -26.92) * mm, "end": v(70.92, -31.54) * mm});
            skLineSegment(sketch, "E2.15.10.2", {"start": v(66.3, -31.54) * mm, "end": v(70.92, -31.54) * mm});
            skLineSegment(sketch, "E2.15.10.3", {"start": v(66.3, -26.92) * mm, "end": v(66.3, -31.54) * mm});
            skLineSegment(sketch, "E2.15.11.0", {"start": v(66.3, -39.62) * mm, "end": v(70.92, -39.62) * mm});
            skLineSegment(sketch, "E2.15.11.1", {"start": v(70.92, -39.62) * mm, "end": v(70.92, -44.24) * mm});
            skLineSegment(sketch, "E2.15.11.2", {"start": v(66.3, -44.24) * mm, "end": v(70.92, -44.24) * mm});
            skLineSegment(sketch, "E2.15.11.3", {"start": v(66.3, -39.62) * mm, "end": v(66.3, -44.24) * mm});
            skLineSegment(sketch, "E2.15.12.0", {"start": v(66.3, -52.32) * mm, "end": v(70.92, -52.32) * mm});
            skLineSegment(sketch, "E2.15.12.1", {"start": v(70.92, -52.32) * mm, "end": v(70.92, -56.94) * mm});
            skLineSegment(sketch, "E2.15.12.2", {"start": v(66.3, -56.94) * mm, "end": v(70.92, -56.94) * mm});
            skLineSegment(sketch, "E2.15.12.3", {"start": v(66.3, -52.32) * mm, "end": v(66.3, -56.94) * mm});
            skLineSegment(sketch, "E2.15.13.0", {"start": v(66.3, -65.02) * mm, "end": v(70.92, -65.02) * mm});
            skLineSegment(sketch, "E2.15.13.1", {"start": v(70.92, -65.02) * mm, "end": v(70.92, -69.64) * mm});
            skLineSegment(sketch, "E2.15.13.2", {"start": v(66.3, -69.64) * mm, "end": v(70.92, -69.64) * mm});
            skLineSegment(sketch, "E2.15.13.3", {"start": v(66.3, -65.02) * mm, "end": v(66.3, -69.64) * mm});
            skLineSegment(sketch, "E2.16.0.0", {"start": v(79, 100.08) * mm, "end": v(83.62, 100.08) * mm});
            skLineSegment(sketch, "E2.16.0.1", {"start": v(83.62, 100.08) * mm, "end": v(83.62, 95.46) * mm});
            skLineSegment(sketch, "E2.16.0.2", {"start": v(79, 95.46) * mm, "end": v(83.62, 95.46) * mm});
            skLineSegment(sketch, "E2.16.0.3", {"start": v(79, 100.08) * mm, "end": v(79, 95.46) * mm});
            skLineSegment(sketch, "E2.16.1.0", {"start": v(79, 87.38) * mm, "end": v(83.62, 87.38) * mm});
            skLineSegment(sketch, "E2.16.1.1", {"start": v(83.62, 87.38) * mm, "end": v(83.62, 82.76) * mm});
            skLineSegment(sketch, "E2.16.1.2", {"start": v(79, 82.76) * mm, "end": v(83.62, 82.76) * mm});
            skLineSegment(sketch, "E2.16.1.3", {"start": v(79, 87.38) * mm, "end": v(79, 82.76) * mm});
            skLineSegment(sketch, "E2.16.2.0", {"start": v(79, 74.68) * mm, "end": v(83.62, 74.68) * mm});
            skLineSegment(sketch, "E2.16.2.1", {"start": v(83.62, 74.68) * mm, "end": v(83.62, 70.06) * mm});
            skLineSegment(sketch, "E2.16.2.2", {"start": v(79, 70.06) * mm, "end": v(83.62, 70.06) * mm});
            skLineSegment(sketch, "E2.16.2.3", {"start": v(79, 74.68) * mm, "end": v(79, 70.06) * mm});
            skLineSegment(sketch, "E2.16.3.0", {"start": v(79, 61.98) * mm, "end": v(83.62, 61.98) * mm});
            skLineSegment(sketch, "E2.16.3.1", {"start": v(83.62, 61.98) * mm, "end": v(83.62, 57.36) * mm});
            skLineSegment(sketch, "E2.16.3.2", {"start": v(79, 57.36) * mm, "end": v(83.62, 57.36) * mm});
            skLineSegment(sketch, "E2.16.3.3", {"start": v(79, 61.98) * mm, "end": v(79, 57.36) * mm});
            skLineSegment(sketch, "E2.16.4.0", {"start": v(79, 49.28) * mm, "end": v(83.62, 49.28) * mm});
            skLineSegment(sketch, "E2.16.4.1", {"start": v(83.62, 49.28) * mm, "end": v(83.62, 44.66) * mm});
            skLineSegment(sketch, "E2.16.4.2", {"start": v(79, 44.66) * mm, "end": v(83.62, 44.66) * mm});
            skLineSegment(sketch, "E2.16.4.3", {"start": v(79, 49.28) * mm, "end": v(79, 44.66) * mm});
            skLineSegment(sketch, "E2.16.5.0", {"start": v(79, 36.58) * mm, "end": v(83.62, 36.58) * mm});
            skLineSegment(sketch, "E2.16.5.1", {"start": v(83.62, 36.58) * mm, "end": v(83.62, 31.96) * mm});
            skLineSegment(sketch, "E2.16.5.2", {"start": v(79, 31.96) * mm, "end": v(83.62, 31.96) * mm});
            skLineSegment(sketch, "E2.16.5.3", {"start": v(79, 36.58) * mm, "end": v(79, 31.96) * mm});
            skLineSegment(sketch, "E2.16.6.0", {"start": v(79, 23.88) * mm, "end": v(83.62, 23.88) * mm});
            skLineSegment(sketch, "E2.16.6.1", {"start": v(83.62, 23.88) * mm, "end": v(83.62, 19.26) * mm});
            skLineSegment(sketch, "E2.16.6.2", {"start": v(79, 19.26) * mm, "end": v(83.62, 19.26) * mm});
            skLineSegment(sketch, "E2.16.6.3", {"start": v(79, 23.88) * mm, "end": v(79, 19.26) * mm});
            skLineSegment(sketch, "E2.16.7.0", {"start": v(79, 11.18) * mm, "end": v(83.62, 11.18) * mm});
            skLineSegment(sketch, "E2.16.7.1", {"start": v(83.62, 11.18) * mm, "end": v(83.62, 6.56) * mm});
            skLineSegment(sketch, "E2.16.7.2", {"start": v(79, 6.56) * mm, "end": v(83.62, 6.56) * mm});
            skLineSegment(sketch, "E2.16.7.3", {"start": v(79, 11.18) * mm, "end": v(79, 6.56) * mm});
            skLineSegment(sketch, "E2.16.8.0", {"start": v(79, -1.52) * mm, "end": v(83.62, -1.52) * mm});
            skLineSegment(sketch, "E2.16.8.1", {"start": v(83.62, -1.52) * mm, "end": v(83.62, -6.14) * mm});
            skLineSegment(sketch, "E2.16.8.2", {"start": v(79, -6.14) * mm, "end": v(83.62, -6.14) * mm});
            skLineSegment(sketch, "E2.16.8.3", {"start": v(79, -1.52) * mm, "end": v(79, -6.14) * mm});
            skLineSegment(sketch, "E2.16.9.0", {"start": v(79, -14.22) * mm, "end": v(83.62, -14.22) * mm});
            skLineSegment(sketch, "E2.16.9.1", {"start": v(83.62, -14.22) * mm, "end": v(83.62, -18.84) * mm});
            skLineSegment(sketch, "E2.16.9.2", {"start": v(79, -18.84) * mm, "end": v(83.62, -18.84) * mm});
            skLineSegment(sketch, "E2.16.9.3", {"start": v(79, -14.22) * mm, "end": v(79, -18.84) * mm});
            skLineSegment(sketch, "E2.16.10.0", {"start": v(79, -26.92) * mm, "end": v(83.62, -26.92) * mm});
            skLineSegment(sketch, "E2.16.10.1", {"start": v(83.62, -26.92) * mm, "end": v(83.62, -31.54) * mm});
            skLineSegment(sketch, "E2.16.10.2", {"start": v(79, -31.54) * mm, "end": v(83.62, -31.54) * mm});
            skLineSegment(sketch, "E2.16.10.3", {"start": v(79, -26.92) * mm, "end": v(79, -31.54) * mm});
            skLineSegment(sketch, "E2.16.11.0", {"start": v(79, -39.62) * mm, "end": v(83.62, -39.62) * mm});
            skLineSegment(sketch, "E2.16.11.1", {"start": v(83.62, -39.62) * mm, "end": v(83.62, -44.24) * mm});
            skLineSegment(sketch, "E2.16.11.2", {"start": v(79, -44.24) * mm, "end": v(83.62, -44.24) * mm});
            skLineSegment(sketch, "E2.16.11.3", {"start": v(79, -39.62) * mm, "end": v(79, -44.24) * mm});
            skLineSegment(sketch, "E2.16.12.0", {"start": v(79, -52.32) * mm, "end": v(83.62, -52.32) * mm});
            skLineSegment(sketch, "E2.16.12.1", {"start": v(83.62, -52.32) * mm, "end": v(83.62, -56.94) * mm});
            skLineSegment(sketch, "E2.16.12.2", {"start": v(79, -56.94) * mm, "end": v(83.62, -56.94) * mm});
            skLineSegment(sketch, "E2.16.12.3", {"start": v(79, -52.32) * mm, "end": v(79, -56.94) * mm});
            skLineSegment(sketch, "E2.16.13.0", {"start": v(79, -65.02) * mm, "end": v(83.62, -65.02) * mm});
            skLineSegment(sketch, "E2.16.13.1", {"start": v(83.62, -65.02) * mm, "end": v(83.62, -69.64) * mm});
            skLineSegment(sketch, "E2.16.13.2", {"start": v(79, -69.64) * mm, "end": v(83.62, -69.64) * mm});
            skLineSegment(sketch, "E2.16.13.3", {"start": v(79, -65.02) * mm, "end": v(79, -69.64) * mm});
            skLineSegment(sketch, "E2.17.0.0", {"start": v(91.7, 100.08) * mm, "end": v(96.32, 100.08) * mm});
            skLineSegment(sketch, "E2.17.0.1", {"start": v(96.32, 100.08) * mm, "end": v(96.32, 95.46) * mm});
            skLineSegment(sketch, "E2.17.0.2", {"start": v(91.7, 95.46) * mm, "end": v(96.32, 95.46) * mm});
            skLineSegment(sketch, "E2.17.0.3", {"start": v(91.7, 100.08) * mm, "end": v(91.7, 95.46) * mm});
            skLineSegment(sketch, "E2.17.1.0", {"start": v(91.7, 87.38) * mm, "end": v(96.32, 87.38) * mm});
            skLineSegment(sketch, "E2.17.1.1", {"start": v(96.32, 87.38) * mm, "end": v(96.32, 82.76) * mm});
            skLineSegment(sketch, "E2.17.1.2", {"start": v(91.7, 82.76) * mm, "end": v(96.32, 82.76) * mm});
            skLineSegment(sketch, "E2.17.1.3", {"start": v(91.7, 87.38) * mm, "end": v(91.7, 82.76) * mm});
            skLineSegment(sketch, "E2.17.2.0", {"start": v(91.7, 74.68) * mm, "end": v(96.32, 74.68) * mm});
            skLineSegment(sketch, "E2.17.2.1", {"start": v(96.32, 74.68) * mm, "end": v(96.32, 70.06) * mm});
            skLineSegment(sketch, "E2.17.2.2", {"start": v(91.7, 70.06) * mm, "end": v(96.32, 70.06) * mm});
            skLineSegment(sketch, "E2.17.2.3", {"start": v(91.7, 74.68) * mm, "end": v(91.7, 70.06) * mm});
            skLineSegment(sketch, "E2.17.3.0", {"start": v(91.7, 61.98) * mm, "end": v(96.32, 61.98) * mm});
            skLineSegment(sketch, "E2.17.3.1", {"start": v(96.32, 61.98) * mm, "end": v(96.32, 57.36) * mm});
            skLineSegment(sketch, "E2.17.3.2", {"start": v(91.7, 57.36) * mm, "end": v(96.32, 57.36) * mm});
            skLineSegment(sketch, "E2.17.3.3", {"start": v(91.7, 61.98) * mm, "end": v(91.7, 57.36) * mm});
            skLineSegment(sketch, "E2.17.4.0", {"start": v(91.7, 49.28) * mm, "end": v(96.32, 49.28) * mm});
            skLineSegment(sketch, "E2.17.4.1", {"start": v(96.32, 49.28) * mm, "end": v(96.32, 44.66) * mm});
            skLineSegment(sketch, "E2.17.4.2", {"start": v(91.7, 44.66) * mm, "end": v(96.32, 44.66) * mm});
            skLineSegment(sketch, "E2.17.4.3", {"start": v(91.7, 49.28) * mm, "end": v(91.7, 44.66) * mm});
            skLineSegment(sketch, "E2.17.5.0", {"start": v(91.7, 36.58) * mm, "end": v(96.32, 36.58) * mm});
            skLineSegment(sketch, "E2.17.5.1", {"start": v(96.32, 36.58) * mm, "end": v(96.32, 31.96) * mm});
            skLineSegment(sketch, "E2.17.5.2", {"start": v(91.7, 31.96) * mm, "end": v(96.32, 31.96) * mm});
            skLineSegment(sketch, "E2.17.5.3", {"start": v(91.7, 36.58) * mm, "end": v(91.7, 31.96) * mm});
            skLineSegment(sketch, "E2.17.6.0", {"start": v(91.7, 23.88) * mm, "end": v(96.32, 23.88) * mm});
            skLineSegment(sketch, "E2.17.6.1", {"start": v(96.32, 23.88) * mm, "end": v(96.32, 19.26) * mm});
            skLineSegment(sketch, "E2.17.6.2", {"start": v(91.7, 19.26) * mm, "end": v(96.32, 19.26) * mm});
            skLineSegment(sketch, "E2.17.6.3", {"start": v(91.7, 23.88) * mm, "end": v(91.7, 19.26) * mm});
            skLineSegment(sketch, "E2.17.7.0", {"start": v(91.7, 11.18) * mm, "end": v(96.32, 11.18) * mm});
            skLineSegment(sketch, "E2.17.7.1", {"start": v(96.32, 11.18) * mm, "end": v(96.32, 6.56) * mm});
            skLineSegment(sketch, "E2.17.7.2", {"start": v(91.7, 6.56) * mm, "end": v(96.32, 6.56) * mm});
            skLineSegment(sketch, "E2.17.7.3", {"start": v(91.7, 11.18) * mm, "end": v(91.7, 6.56) * mm});
            skLineSegment(sketch, "E2.17.8.0", {"start": v(91.7, -1.52) * mm, "end": v(96.32, -1.52) * mm});
            skLineSegment(sketch, "E2.17.8.1", {"start": v(96.32, -1.52) * mm, "end": v(96.32, -6.14) * mm});
            skLineSegment(sketch, "E2.17.8.2", {"start": v(91.7, -6.14) * mm, "end": v(96.32, -6.14) * mm});
            skLineSegment(sketch, "E2.17.8.3", {"start": v(91.7, -1.52) * mm, "end": v(91.7, -6.14) * mm});
            skLineSegment(sketch, "E2.17.9.0", {"start": v(91.7, -14.22) * mm, "end": v(96.32, -14.22) * mm});
            skLineSegment(sketch, "E2.17.9.1", {"start": v(96.32, -14.22) * mm, "end": v(96.32, -18.84) * mm});
            skLineSegment(sketch, "E2.17.9.2", {"start": v(91.7, -18.84) * mm, "end": v(96.32, -18.84) * mm});
            skLineSegment(sketch, "E2.17.9.3", {"start": v(91.7, -14.22) * mm, "end": v(91.7, -18.84) * mm});
            skLineSegment(sketch, "E2.17.10.0", {"start": v(91.7, -26.92) * mm, "end": v(96.32, -26.92) * mm});
            skLineSegment(sketch, "E2.17.10.1", {"start": v(96.32, -26.92) * mm, "end": v(96.32, -31.54) * mm});
            skLineSegment(sketch, "E2.17.10.2", {"start": v(91.7, -31.54) * mm, "end": v(96.32, -31.54) * mm});
            skLineSegment(sketch, "E2.17.10.3", {"start": v(91.7, -26.92) * mm, "end": v(91.7, -31.54) * mm});
            skLineSegment(sketch, "E2.17.11.0", {"start": v(91.7, -39.62) * mm, "end": v(96.32, -39.62) * mm});
            skLineSegment(sketch, "E2.17.11.1", {"start": v(96.32, -39.62) * mm, "end": v(96.32, -44.24) * mm});
            skLineSegment(sketch, "E2.17.11.2", {"start": v(91.7, -44.24) * mm, "end": v(96.32, -44.24) * mm});
            skLineSegment(sketch, "E2.17.11.3", {"start": v(91.7, -39.62) * mm, "end": v(91.7, -44.24) * mm});
            skLineSegment(sketch, "E2.17.12.0", {"start": v(91.7, -52.32) * mm, "end": v(96.32, -52.32) * mm});
            skLineSegment(sketch, "E2.17.12.1", {"start": v(96.32, -52.32) * mm, "end": v(96.32, -56.94) * mm});
            skLineSegment(sketch, "E2.17.12.2", {"start": v(91.7, -56.94) * mm, "end": v(96.32, -56.94) * mm});
            skLineSegment(sketch, "E2.17.12.3", {"start": v(91.7, -52.32) * mm, "end": v(91.7, -56.94) * mm});
            skLineSegment(sketch, "E2.17.13.0", {"start": v(91.7, -65.02) * mm, "end": v(96.32, -65.02) * mm});
            skLineSegment(sketch, "E2.17.13.1", {"start": v(96.32, -65.02) * mm, "end": v(96.32, -69.64) * mm});
            skLineSegment(sketch, "E2.17.13.2", {"start": v(91.7, -69.64) * mm, "end": v(96.32, -69.64) * mm});
            skLineSegment(sketch, "E2.17.13.3", {"start": v(91.7, -65.02) * mm, "end": v(91.7, -69.64) * mm});
            skLineSegment(sketch, "E2.18.0.0", {"start": v(104.4, 100.08) * mm, "end": v(109.02, 100.08) * mm});
            skLineSegment(sketch, "E2.18.0.1", {"start": v(109.02, 100.08) * mm, "end": v(109.02, 95.46) * mm});
            skLineSegment(sketch, "E2.18.0.2", {"start": v(104.4, 95.46) * mm, "end": v(109.02, 95.46) * mm});
            skLineSegment(sketch, "E2.18.0.3", {"start": v(104.4, 100.08) * mm, "end": v(104.4, 95.46) * mm});
            skLineSegment(sketch, "E2.18.1.0", {"start": v(104.4, 87.38) * mm, "end": v(109.02, 87.38) * mm});
            skLineSegment(sketch, "E2.18.1.1", {"start": v(109.02, 87.38) * mm, "end": v(109.02, 82.76) * mm});
            skLineSegment(sketch, "E2.18.1.2", {"start": v(104.4, 82.76) * mm, "end": v(109.02, 82.76) * mm});
            skLineSegment(sketch, "E2.18.1.3", {"start": v(104.4, 87.38) * mm, "end": v(104.4, 82.76) * mm});
            skLineSegment(sketch, "E2.18.2.0", {"start": v(104.4, 74.68) * mm, "end": v(109.02, 74.68) * mm});
            skLineSegment(sketch, "E2.18.2.1", {"start": v(109.02, 74.68) * mm, "end": v(109.02, 70.06) * mm});
            skLineSegment(sketch, "E2.18.2.2", {"start": v(104.4, 70.06) * mm, "end": v(109.02, 70.06) * mm});
            skLineSegment(sketch, "E2.18.2.3", {"start": v(104.4, 74.68) * mm, "end": v(104.4, 70.06) * mm});
            skLineSegment(sketch, "E2.18.3.0", {"start": v(104.4, 61.98) * mm, "end": v(109.02, 61.98) * mm});
            skLineSegment(sketch, "E2.18.3.1", {"start": v(109.02, 61.98) * mm, "end": v(109.02, 57.36) * mm});
            skLineSegment(sketch, "E2.18.3.2", {"start": v(104.4, 57.36) * mm, "end": v(109.02, 57.36) * mm});
            skLineSegment(sketch, "E2.18.3.3", {"start": v(104.4, 61.98) * mm, "end": v(104.4, 57.36) * mm});
            skLineSegment(sketch, "E2.18.4.0", {"start": v(104.4, 49.28) * mm, "end": v(109.02, 49.28) * mm});
            skLineSegment(sketch, "E2.18.4.1", {"start": v(109.02, 49.28) * mm, "end": v(109.02, 44.66) * mm});
            skLineSegment(sketch, "E2.18.4.2", {"start": v(104.4, 44.66) * mm, "end": v(109.02, 44.66) * mm});
            skLineSegment(sketch, "E2.18.4.3", {"start": v(104.4, 49.28) * mm, "end": v(104.4, 44.66) * mm});
            skLineSegment(sketch, "E2.18.5.0", {"start": v(104.4, 36.58) * mm, "end": v(109.02, 36.58) * mm});
            skLineSegment(sketch, "E2.18.5.1", {"start": v(109.02, 36.58) * mm, "end": v(109.02, 31.96) * mm});
            skLineSegment(sketch, "E2.18.5.2", {"start": v(104.4, 31.96) * mm, "end": v(109.02, 31.96) * mm});
            skLineSegment(sketch, "E2.18.5.3", {"start": v(104.4, 36.58) * mm, "end": v(104.4, 31.96) * mm});
            skLineSegment(sketch, "E2.18.6.0", {"start": v(104.4, 23.88) * mm, "end": v(109.02, 23.88) * mm});
            skLineSegment(sketch, "E2.18.6.1", {"start": v(109.02, 23.88) * mm, "end": v(109.02, 19.26) * mm});
            skLineSegment(sketch, "E2.18.6.2", {"start": v(104.4, 19.26) * mm, "end": v(109.02, 19.26) * mm});
            skLineSegment(sketch, "E2.18.6.3", {"start": v(104.4, 23.88) * mm, "end": v(104.4, 19.26) * mm});
            skLineSegment(sketch, "E2.18.7.0", {"start": v(104.4, 11.18) * mm, "end": v(109.02, 11.18) * mm});
            skLineSegment(sketch, "E2.18.7.1", {"start": v(109.02, 11.18) * mm, "end": v(109.02, 6.56) * mm});
            skLineSegment(sketch, "E2.18.7.2", {"start": v(104.4, 6.56) * mm, "end": v(109.02, 6.56) * mm});
            skLineSegment(sketch, "E2.18.7.3", {"start": v(104.4, 11.18) * mm, "end": v(104.4, 6.56) * mm});
            skLineSegment(sketch, "E2.18.8.0", {"start": v(104.4, -1.52) * mm, "end": v(109.02, -1.52) * mm});
            skLineSegment(sketch, "E2.18.8.1", {"start": v(109.02, -1.52) * mm, "end": v(109.02, -6.14) * mm});
            skLineSegment(sketch, "E2.18.8.2", {"start": v(104.4, -6.14) * mm, "end": v(109.02, -6.14) * mm});
            skLineSegment(sketch, "E2.18.8.3", {"start": v(104.4, -1.52) * mm, "end": v(104.4, -6.14) * mm});
            skLineSegment(sketch, "E2.18.9.0", {"start": v(104.4, -14.22) * mm, "end": v(109.02, -14.22) * mm});
            skLineSegment(sketch, "E2.18.9.1", {"start": v(109.02, -14.22) * mm, "end": v(109.02, -18.84) * mm});
            skLineSegment(sketch, "E2.18.9.2", {"start": v(104.4, -18.84) * mm, "end": v(109.02, -18.84) * mm});
            skLineSegment(sketch, "E2.18.9.3", {"start": v(104.4, -14.22) * mm, "end": v(104.4, -18.84) * mm});
            skLineSegment(sketch, "E2.18.10.0", {"start": v(104.4, -26.92) * mm, "end": v(109.02, -26.92) * mm});
            skLineSegment(sketch, "E2.18.10.1", {"start": v(109.02, -26.92) * mm, "end": v(109.02, -31.54) * mm});
            skLineSegment(sketch, "E2.18.10.2", {"start": v(104.4, -31.54) * mm, "end": v(109.02, -31.54) * mm});
            skLineSegment(sketch, "E2.18.10.3", {"start": v(104.4, -26.92) * mm, "end": v(104.4, -31.54) * mm});
            skLineSegment(sketch, "E2.18.11.0", {"start": v(104.4, -39.62) * mm, "end": v(109.02, -39.62) * mm});
            skLineSegment(sketch, "E2.18.11.1", {"start": v(109.02, -39.62) * mm, "end": v(109.02, -44.24) * mm});
            skLineSegment(sketch, "E2.18.11.2", {"start": v(104.4, -44.24) * mm, "end": v(109.02, -44.24) * mm});
            skLineSegment(sketch, "E2.18.11.3", {"start": v(104.4, -39.62) * mm, "end": v(104.4, -44.24) * mm});
            skLineSegment(sketch, "E2.18.12.0", {"start": v(104.4, -52.32) * mm, "end": v(109.02, -52.32) * mm});
            skLineSegment(sketch, "E2.18.12.1", {"start": v(109.02, -52.32) * mm, "end": v(109.02, -56.94) * mm});
            skLineSegment(sketch, "E2.18.12.2", {"start": v(104.4, -56.94) * mm, "end": v(109.02, -56.94) * mm});
            skLineSegment(sketch, "E2.18.12.3", {"start": v(104.4, -52.32) * mm, "end": v(104.4, -56.94) * mm});
            skLineSegment(sketch, "E2.18.13.0", {"start": v(104.4, -65.02) * mm, "end": v(109.02, -65.02) * mm});
            skLineSegment(sketch, "E2.18.13.1", {"start": v(109.02, -65.02) * mm, "end": v(109.02, -69.64) * mm});
            skLineSegment(sketch, "E2.18.13.2", {"start": v(104.4, -69.64) * mm, "end": v(109.02, -69.64) * mm});
            skLineSegment(sketch, "E2.18.13.3", {"start": v(104.4, -65.02) * mm, "end": v(104.4, -69.64) * mm});
            skLineSegment(sketch, "E2.19.0.0", {"start": v(117.1, 100.08) * mm, "end": v(121.72, 100.08) * mm});
            skLineSegment(sketch, "E2.19.0.1", {"start": v(121.72, 100.08) * mm, "end": v(121.72, 95.46) * mm});
            skLineSegment(sketch, "E2.19.0.2", {"start": v(117.1, 95.46) * mm, "end": v(121.72, 95.46) * mm});
            skLineSegment(sketch, "E2.19.0.3", {"start": v(117.1, 100.08) * mm, "end": v(117.1, 95.46) * mm});
            skLineSegment(sketch, "E2.19.1.0", {"start": v(117.1, 87.38) * mm, "end": v(121.72, 87.38) * mm});
            skLineSegment(sketch, "E2.19.1.1", {"start": v(121.72, 87.38) * mm, "end": v(121.72, 82.76) * mm});
            skLineSegment(sketch, "E2.19.1.2", {"start": v(117.1, 82.76) * mm, "end": v(121.72, 82.76) * mm});
            skLineSegment(sketch, "E2.19.1.3", {"start": v(117.1, 87.38) * mm, "end": v(117.1, 82.76) * mm});
            skLineSegment(sketch, "E2.19.2.0", {"start": v(117.1, 74.68) * mm, "end": v(121.72, 74.68) * mm});
            skLineSegment(sketch, "E2.19.2.1", {"start": v(121.72, 74.68) * mm, "end": v(121.72, 70.06) * mm});
            skLineSegment(sketch, "E2.19.2.2", {"start": v(117.1, 70.06) * mm, "end": v(121.72, 70.06) * mm});
            skLineSegment(sketch, "E2.19.2.3", {"start": v(117.1, 74.68) * mm, "end": v(117.1, 70.06) * mm});
            skLineSegment(sketch, "E2.19.3.0", {"start": v(117.1, 61.98) * mm, "end": v(121.72, 61.98) * mm});
            skLineSegment(sketch, "E2.19.3.1", {"start": v(121.72, 61.98) * mm, "end": v(121.72, 57.36) * mm});
            skLineSegment(sketch, "E2.19.3.2", {"start": v(117.1, 57.36) * mm, "end": v(121.72, 57.36) * mm});
            skLineSegment(sketch, "E2.19.3.3", {"start": v(117.1, 61.98) * mm, "end": v(117.1, 57.36) * mm});
            skLineSegment(sketch, "E2.19.4.0", {"start": v(117.1, 49.28) * mm, "end": v(121.72, 49.28) * mm});
            skLineSegment(sketch, "E2.19.4.1", {"start": v(121.72, 49.28) * mm, "end": v(121.72, 44.66) * mm});
            skLineSegment(sketch, "E2.19.4.2", {"start": v(117.1, 44.66) * mm, "end": v(121.72, 44.66) * mm});
            skLineSegment(sketch, "E2.19.4.3", {"start": v(117.1, 49.28) * mm, "end": v(117.1, 44.66) * mm});
            skLineSegment(sketch, "E2.19.5.0", {"start": v(117.1, 36.58) * mm, "end": v(121.72, 36.58) * mm});
            skLineSegment(sketch, "E2.19.5.1", {"start": v(121.72, 36.58) * mm, "end": v(121.72, 31.96) * mm});
            skLineSegment(sketch, "E2.19.5.2", {"start": v(117.1, 31.96) * mm, "end": v(121.72, 31.96) * mm});
            skLineSegment(sketch, "E2.19.5.3", {"start": v(117.1, 36.58) * mm, "end": v(117.1, 31.96) * mm});
            skLineSegment(sketch, "E2.19.6.0", {"start": v(117.1, 23.88) * mm, "end": v(121.72, 23.88) * mm});
            skLineSegment(sketch, "E2.19.6.1", {"start": v(121.72, 23.88) * mm, "end": v(121.72, 19.26) * mm});
            skLineSegment(sketch, "E2.19.6.2", {"start": v(117.1, 19.26) * mm, "end": v(121.72, 19.26) * mm});
            skLineSegment(sketch, "E2.19.6.3", {"start": v(117.1, 23.88) * mm, "end": v(117.1, 19.26) * mm});
            skLineSegment(sketch, "E2.19.7.0", {"start": v(117.1, 11.18) * mm, "end": v(121.72, 11.18) * mm});
            skLineSegment(sketch, "E2.19.7.1", {"start": v(121.72, 11.18) * mm, "end": v(121.72, 6.56) * mm});
            skLineSegment(sketch, "E2.19.7.2", {"start": v(117.1, 6.56) * mm, "end": v(121.72, 6.56) * mm});
            skLineSegment(sketch, "E2.19.7.3", {"start": v(117.1, 11.18) * mm, "end": v(117.1, 6.56) * mm});
            skLineSegment(sketch, "E2.19.8.0", {"start": v(117.1, -1.52) * mm, "end": v(121.72, -1.52) * mm});
            skLineSegment(sketch, "E2.19.8.1", {"start": v(121.72, -1.52) * mm, "end": v(121.72, -6.14) * mm});
            skLineSegment(sketch, "E2.19.8.2", {"start": v(117.1, -6.14) * mm, "end": v(121.72, -6.14) * mm});
            skLineSegment(sketch, "E2.19.8.3", {"start": v(117.1, -1.52) * mm, "end": v(117.1, -6.14) * mm});
            skLineSegment(sketch, "E2.19.9.0", {"start": v(117.1, -14.22) * mm, "end": v(121.72, -14.22) * mm});
            skLineSegment(sketch, "E2.19.9.1", {"start": v(121.72, -14.22) * mm, "end": v(121.72, -18.84) * mm});
            skLineSegment(sketch, "E2.19.9.2", {"start": v(117.1, -18.84) * mm, "end": v(121.72, -18.84) * mm});
            skLineSegment(sketch, "E2.19.9.3", {"start": v(117.1, -14.22) * mm, "end": v(117.1, -18.84) * mm});
            skLineSegment(sketch, "E2.19.10.0", {"start": v(117.1, -26.92) * mm, "end": v(121.72, -26.92) * mm});
            skLineSegment(sketch, "E2.19.10.1", {"start": v(121.72, -26.92) * mm, "end": v(121.72, -31.54) * mm});
            skLineSegment(sketch, "E2.19.10.2", {"start": v(117.1, -31.54) * mm, "end": v(121.72, -31.54) * mm});
            skLineSegment(sketch, "E2.19.10.3", {"start": v(117.1, -26.92) * mm, "end": v(117.1, -31.54) * mm});
            skLineSegment(sketch, "E2.19.11.0", {"start": v(117.1, -39.62) * mm, "end": v(121.72, -39.62) * mm});
            skLineSegment(sketch, "E2.19.11.1", {"start": v(121.72, -39.62) * mm, "end": v(121.72, -44.24) * mm});
            skLineSegment(sketch, "E2.19.11.2", {"start": v(117.1, -44.24) * mm, "end": v(121.72, -44.24) * mm});
            skLineSegment(sketch, "E2.19.11.3", {"start": v(117.1, -39.62) * mm, "end": v(117.1, -44.24) * mm});
            skLineSegment(sketch, "E2.19.12.0", {"start": v(117.1, -52.32) * mm, "end": v(121.72, -52.32) * mm});
            skLineSegment(sketch, "E2.19.12.1", {"start": v(121.72, -52.32) * mm, "end": v(121.72, -56.94) * mm});
            skLineSegment(sketch, "E2.19.12.2", {"start": v(117.1, -56.94) * mm, "end": v(121.72, -56.94) * mm});
            skLineSegment(sketch, "E2.19.12.3", {"start": v(117.1, -52.32) * mm, "end": v(117.1, -56.94) * mm});
            skLineSegment(sketch, "E2.19.13.0", {"start": v(117.1, -65.02) * mm, "end": v(121.72, -65.02) * mm});
            skLineSegment(sketch, "E2.19.13.1", {"start": v(121.72, -65.02) * mm, "end": v(121.72, -69.64) * mm});
            skLineSegment(sketch, "E2.19.13.2", {"start": v(117.1, -69.64) * mm, "end": v(121.72, -69.64) * mm});
            skLineSegment(sketch, "E2.19.13.3", {"start": v(117.1, -65.02) * mm, "end": v(117.1, -69.64) * mm});
            skLineSegment(sketch, "E2.direction1", {"start": v(-124.2, 100.08) * mm, "end": v(-111.5, 100.08) * mm, "construction": true});
            skLineSegment(sketch, "E2.direction2", {"start": v(-124.2, 100.08) * mm, "end": v(-124.2, 87.38) * mm, "construction": true});
            skLineSegment(sketch, "E3.bottom", {"start": v(-124.2, 100.08) * mm, "end": v(-106.88, 100.08) * mm, "construction": true});
            skLineSegment(sketch, "E3.top", {"start": v(-124.2, 82.76) * mm, "end": v(-106.88, 82.76) * mm});
            skLineSegment(sketch, "E3.left", {"start": v(-124.2, 100.08) * mm, "end": v(-124.2, 82.76) * mm, "construction": true});
            skLineSegment(sketch, "E3.right", {"start": v(-106.88, 100.08) * mm, "end": v(-106.88, 82.76) * mm, "construction": true});
            skLineSegment(sketch, "E4", {"start": v(-106.88, 91.42) * mm, "end": v(-124.2, 91.42) * mm, "construction": true});
            skLineSegment(sketch, "E5.rect.bottom", {"start": v(-113.23, 89.11) * mm, "end": v(-117.86, 89.11) * mm});
            skLineSegment(sketch, "E5.rect.top", {"start": v(-113.23, 93.73) * mm, "end": v(-117.86, 93.73) * mm});
            skLineSegment(sketch, "E5.rect.left", {"start": v(-113.23, 89.11) * mm, "end": v(-113.23, 93.73) * mm});
            skLineSegment(sketch, "E5.rect.right", {"start": v(-117.86, 89.11) * mm, "end": v(-117.86, 93.73) * mm});
            skPoint(sketch, "E5.rect.middle", {"position": v(-115.54, 91.42) * mm});
            skLineSegment(sketch, "E6.0.1.0", {"start": v(-113.23, 81.03) * mm, "end": v(-117.86, 81.03) * mm});
            skLineSegment(sketch, "E6.0.1.1", {"start": v(-113.23, 76.41) * mm, "end": v(-113.23, 81.03) * mm});
            skLineSegment(sketch, "E6.0.1.2", {"start": v(-113.23, 76.41) * mm, "end": v(-117.86, 76.41) * mm});
            skLineSegment(sketch, "E6.0.1.3", {"start": v(-117.86, 76.41) * mm, "end": v(-117.86, 81.03) * mm});
            skLineSegment(sketch, "E6.0.2.0", {"start": v(-113.23, 68.33) * mm, "end": v(-117.86, 68.33) * mm});
            skLineSegment(sketch, "E6.0.2.1", {"start": v(-113.23, 63.71) * mm, "end": v(-113.23, 68.33) * mm});
            skLineSegment(sketch, "E6.0.2.2", {"start": v(-113.23, 63.71) * mm, "end": v(-117.86, 63.71) * mm});
            skLineSegment(sketch, "E6.0.2.3", {"start": v(-117.86, 63.71) * mm, "end": v(-117.86, 68.33) * mm});
            skLineSegment(sketch, "E6.0.3.0", {"start": v(-113.23, 55.63) * mm, "end": v(-117.86, 55.63) * mm});
            skLineSegment(sketch, "E6.0.3.1", {"start": v(-113.23, 51.01) * mm, "end": v(-113.23, 55.63) * mm});
            skLineSegment(sketch, "E6.0.3.2", {"start": v(-113.23, 51.01) * mm, "end": v(-117.86, 51.01) * mm});
            skLineSegment(sketch, "E6.0.3.3", {"start": v(-117.86, 51.01) * mm, "end": v(-117.86, 55.63) * mm});
            skLineSegment(sketch, "E6.0.4.0", {"start": v(-113.23, 42.93) * mm, "end": v(-117.86, 42.93) * mm});
            skLineSegment(sketch, "E6.0.4.1", {"start": v(-113.23, 38.31) * mm, "end": v(-113.23, 42.93) * mm});
            skLineSegment(sketch, "E6.0.4.2", {"start": v(-113.23, 38.31) * mm, "end": v(-117.86, 38.31) * mm});
            skLineSegment(sketch, "E6.0.4.3", {"start": v(-117.86, 38.31) * mm, "end": v(-117.86, 42.93) * mm});
            skLineSegment(sketch, "E6.0.5.0", {"start": v(-113.23, 30.23) * mm, "end": v(-117.86, 30.23) * mm});
            skLineSegment(sketch, "E6.0.5.1", {"start": v(-113.23, 25.61) * mm, "end": v(-113.23, 30.23) * mm});
            skLineSegment(sketch, "E6.0.5.2", {"start": v(-113.23, 25.61) * mm, "end": v(-117.86, 25.61) * mm});
            skLineSegment(sketch, "E6.0.5.3", {"start": v(-117.86, 25.61) * mm, "end": v(-117.86, 30.23) * mm});
            skLineSegment(sketch, "E6.0.6.0", {"start": v(-113.23, 17.53) * mm, "end": v(-117.86, 17.53) * mm});
            skLineSegment(sketch, "E6.0.6.1", {"start": v(-113.23, 12.91) * mm, "end": v(-113.23, 17.53) * mm});
            skLineSegment(sketch, "E6.0.6.2", {"start": v(-113.23, 12.91) * mm, "end": v(-117.86, 12.91) * mm});
            skLineSegment(sketch, "E6.0.6.3", {"start": v(-117.86, 12.91) * mm, "end": v(-117.86, 17.53) * mm});
            skLineSegment(sketch, "E6.0.7.0", {"start": v(-113.23, 4.83) * mm, "end": v(-117.86, 4.83) * mm});
            skLineSegment(sketch, "E6.0.7.1", {"start": v(-113.23, 0.21) * mm, "end": v(-113.23, 4.83) * mm});
            skLineSegment(sketch, "E6.0.7.2", {"start": v(-113.23, 0.21) * mm, "end": v(-117.86, 0.21) * mm});
            skLineSegment(sketch, "E6.0.7.3", {"start": v(-117.86, 0.21) * mm, "end": v(-117.86, 4.83) * mm});
            skLineSegment(sketch, "E6.0.8.0", {"start": v(-113.23, -7.87) * mm, "end": v(-117.86, -7.87) * mm});
            skLineSegment(sketch, "E6.0.8.1", {"start": v(-113.23, -12.49) * mm, "end": v(-113.23, -7.87) * mm});
            skLineSegment(sketch, "E6.0.8.2", {"start": v(-113.23, -12.49) * mm, "end": v(-117.86, -12.49) * mm});
            skLineSegment(sketch, "E6.0.8.3", {"start": v(-117.86, -12.49) * mm, "end": v(-117.86, -7.87) * mm});
            skLineSegment(sketch, "E6.0.9.0", {"start": v(-113.23, -20.57) * mm, "end": v(-117.86, -20.57) * mm});
            skLineSegment(sketch, "E6.0.9.1", {"start": v(-113.23, -25.19) * mm, "end": v(-113.23, -20.57) * mm});
            skLineSegment(sketch, "E6.0.9.2", {"start": v(-113.23, -25.19) * mm, "end": v(-117.86, -25.19) * mm});
            skLineSegment(sketch, "E6.0.9.3", {"start": v(-117.86, -25.19) * mm, "end": v(-117.86, -20.57) * mm});
            skLineSegment(sketch, "E6.0.10.0", {"start": v(-113.23, -33.27) * mm, "end": v(-117.86, -33.27) * mm});
            skLineSegment(sketch, "E6.0.10.1", {"start": v(-113.23, -37.89) * mm, "end": v(-113.23, -33.27) * mm});
            skLineSegment(sketch, "E6.0.10.2", {"start": v(-113.23, -37.89) * mm, "end": v(-117.86, -37.89) * mm});
            skLineSegment(sketch, "E6.0.10.3", {"start": v(-117.86, -37.89) * mm, "end": v(-117.86, -33.27) * mm});
            skLineSegment(sketch, "E6.0.11.0", {"start": v(-113.23, -45.97) * mm, "end": v(-117.86, -45.97) * mm});
            skLineSegment(sketch, "E6.0.11.1", {"start": v(-113.23, -50.59) * mm, "end": v(-113.23, -45.97) * mm});
            skLineSegment(sketch, "E6.0.11.2", {"start": v(-113.23, -50.59) * mm, "end": v(-117.86, -50.59) * mm});
            skLineSegment(sketch, "E6.0.11.3", {"start": v(-117.86, -50.59) * mm, "end": v(-117.86, -45.97) * mm});
            skLineSegment(sketch, "E6.0.12.0", {"start": v(-113.23, -58.67) * mm, "end": v(-117.86, -58.67) * mm});
            skLineSegment(sketch, "E6.0.12.1", {"start": v(-113.23, -63.29) * mm, "end": v(-113.23, -58.67) * mm});
            skLineSegment(sketch, "E6.0.12.2", {"start": v(-113.23, -63.29) * mm, "end": v(-117.86, -63.29) * mm});
            skLineSegment(sketch, "E6.0.12.3", {"start": v(-117.86, -63.29) * mm, "end": v(-117.86, -58.67) * mm});
            skLineSegment(sketch, "E6.1.0.0", {"start": v(-100.53, 93.73) * mm, "end": v(-105.16, 93.73) * mm});
            skLineSegment(sketch, "E6.1.0.1", {"start": v(-100.53, 89.11) * mm, "end": v(-100.53, 93.73) * mm});
            skLineSegment(sketch, "E6.1.0.2", {"start": v(-100.53, 89.11) * mm, "end": v(-105.16, 89.11) * mm});
            skLineSegment(sketch, "E6.1.0.3", {"start": v(-105.16, 89.11) * mm, "end": v(-105.16, 93.73) * mm});
            skLineSegment(sketch, "E6.1.1.0", {"start": v(-100.53, 81.03) * mm, "end": v(-105.16, 81.03) * mm});
            skLineSegment(sketch, "E6.1.1.1", {"start": v(-100.53, 76.41) * mm, "end": v(-100.53, 81.03) * mm});
            skLineSegment(sketch, "E6.1.1.2", {"start": v(-100.53, 76.41) * mm, "end": v(-105.16, 76.41) * mm});
            skLineSegment(sketch, "E6.1.1.3", {"start": v(-105.16, 76.41) * mm, "end": v(-105.16, 81.03) * mm});
            skLineSegment(sketch, "E6.1.2.0", {"start": v(-100.53, 68.33) * mm, "end": v(-105.16, 68.33) * mm});
            skLineSegment(sketch, "E6.1.2.1", {"start": v(-100.53, 63.71) * mm, "end": v(-100.53, 68.33) * mm});
            skLineSegment(sketch, "E6.1.2.2", {"start": v(-100.53, 63.71) * mm, "end": v(-105.16, 63.71) * mm});
            skLineSegment(sketch, "E6.1.2.3", {"start": v(-105.16, 63.71) * mm, "end": v(-105.16, 68.33) * mm});
            skLineSegment(sketch, "E6.1.3.0", {"start": v(-100.53, 55.63) * mm, "end": v(-105.16, 55.63) * mm});
            skLineSegment(sketch, "E6.1.3.1", {"start": v(-100.53, 51.01) * mm, "end": v(-100.53, 55.63) * mm});
            skLineSegment(sketch, "E6.1.3.2", {"start": v(-100.53, 51.01) * mm, "end": v(-105.16, 51.01) * mm});
            skLineSegment(sketch, "E6.1.3.3", {"start": v(-105.16, 51.01) * mm, "end": v(-105.16, 55.63) * mm});
            skLineSegment(sketch, "E6.1.4.0", {"start": v(-100.53, 42.93) * mm, "end": v(-105.16, 42.93) * mm});
            skLineSegment(sketch, "E6.1.4.1", {"start": v(-100.53, 38.31) * mm, "end": v(-100.53, 42.93) * mm});
            skLineSegment(sketch, "E6.1.4.2", {"start": v(-100.53, 38.31) * mm, "end": v(-105.16, 38.31) * mm});
            skLineSegment(sketch, "E6.1.4.3", {"start": v(-105.16, 38.31) * mm, "end": v(-105.16, 42.93) * mm});
            skLineSegment(sketch, "E6.1.5.0", {"start": v(-100.53, 30.23) * mm, "end": v(-105.16, 30.23) * mm});
            skLineSegment(sketch, "E6.1.5.1", {"start": v(-100.53, 25.61) * mm, "end": v(-100.53, 30.23) * mm});
            skLineSegment(sketch, "E6.1.5.2", {"start": v(-100.53, 25.61) * mm, "end": v(-105.16, 25.61) * mm});
            skLineSegment(sketch, "E6.1.5.3", {"start": v(-105.16, 25.61) * mm, "end": v(-105.16, 30.23) * mm});
            skLineSegment(sketch, "E6.1.6.0", {"start": v(-100.53, 17.53) * mm, "end": v(-105.16, 17.53) * mm});
            skLineSegment(sketch, "E6.1.6.1", {"start": v(-100.53, 12.91) * mm, "end": v(-100.53, 17.53) * mm});
            skLineSegment(sketch, "E6.1.6.2", {"start": v(-100.53, 12.91) * mm, "end": v(-105.16, 12.91) * mm});
            skLineSegment(sketch, "E6.1.6.3", {"start": v(-105.16, 12.91) * mm, "end": v(-105.16, 17.53) * mm});
            skLineSegment(sketch, "E6.1.7.0", {"start": v(-100.53, 4.83) * mm, "end": v(-105.16, 4.83) * mm});
            skLineSegment(sketch, "E6.1.7.1", {"start": v(-100.53, 0.21) * mm, "end": v(-100.53, 4.83) * mm});
            skLineSegment(sketch, "E6.1.7.2", {"start": v(-100.53, 0.21) * mm, "end": v(-105.16, 0.21) * mm});
            skLineSegment(sketch, "E6.1.7.3", {"start": v(-105.16, 0.21) * mm, "end": v(-105.16, 4.83) * mm});
            skLineSegment(sketch, "E6.1.8.0", {"start": v(-100.53, -7.87) * mm, "end": v(-105.16, -7.87) * mm});
            skLineSegment(sketch, "E6.1.8.1", {"start": v(-100.53, -12.49) * mm, "end": v(-100.53, -7.87) * mm});
            skLineSegment(sketch, "E6.1.8.2", {"start": v(-100.53, -12.49) * mm, "end": v(-105.16, -12.49) * mm});
            skLineSegment(sketch, "E6.1.8.3", {"start": v(-105.16, -12.49) * mm, "end": v(-105.16, -7.87) * mm});
            skLineSegment(sketch, "E6.1.9.0", {"start": v(-100.53, -20.57) * mm, "end": v(-105.16, -20.57) * mm});
            skLineSegment(sketch, "E6.1.9.1", {"start": v(-100.53, -25.19) * mm, "end": v(-100.53, -20.57) * mm});
            skLineSegment(sketch, "E6.1.9.2", {"start": v(-100.53, -25.19) * mm, "end": v(-105.16, -25.19) * mm});
            skLineSegment(sketch, "E6.1.9.3", {"start": v(-105.16, -25.19) * mm, "end": v(-105.16, -20.57) * mm});
            skLineSegment(sketch, "E6.1.10.0", {"start": v(-100.53, -33.27) * mm, "end": v(-105.16, -33.27) * mm});
            skLineSegment(sketch, "E6.1.10.1", {"start": v(-100.53, -37.89) * mm, "end": v(-100.53, -33.27) * mm});
            skLineSegment(sketch, "E6.1.10.2", {"start": v(-100.53, -37.89) * mm, "end": v(-105.16, -37.89) * mm});
            skLineSegment(sketch, "E6.1.10.3", {"start": v(-105.16, -37.89) * mm, "end": v(-105.16, -33.27) * mm});
            skLineSegment(sketch, "E6.1.11.0", {"start": v(-100.53, -45.97) * mm, "end": v(-105.16, -45.97) * mm});
            skLineSegment(sketch, "E6.1.11.1", {"start": v(-100.53, -50.59) * mm, "end": v(-100.53, -45.97) * mm});
            skLineSegment(sketch, "E6.1.11.2", {"start": v(-100.53, -50.59) * mm, "end": v(-105.16, -50.59) * mm});
            skLineSegment(sketch, "E6.1.11.3", {"start": v(-105.16, -50.59) * mm, "end": v(-105.16, -45.97) * mm});
            skLineSegment(sketch, "E6.1.12.0", {"start": v(-100.53, -58.67) * mm, "end": v(-105.16, -58.67) * mm});
            skLineSegment(sketch, "E6.1.12.1", {"start": v(-100.53, -63.29) * mm, "end": v(-100.53, -58.67) * mm});
            skLineSegment(sketch, "E6.1.12.2", {"start": v(-100.53, -63.29) * mm, "end": v(-105.16, -63.29) * mm});
            skLineSegment(sketch, "E6.1.12.3", {"start": v(-105.16, -63.29) * mm, "end": v(-105.16, -58.67) * mm});
            skLineSegment(sketch, "E6.2.0.0", {"start": v(-87.83, 93.73) * mm, "end": v(-92.46, 93.73) * mm});
            skLineSegment(sketch, "E6.2.0.1", {"start": v(-87.83, 89.11) * mm, "end": v(-87.83, 93.73) * mm});
            skLineSegment(sketch, "E6.2.0.2", {"start": v(-87.83, 89.11) * mm, "end": v(-92.46, 89.11) * mm});
            skLineSegment(sketch, "E6.2.0.3", {"start": v(-92.46, 89.11) * mm, "end": v(-92.46, 93.73) * mm});
            skLineSegment(sketch, "E6.2.1.0", {"start": v(-87.83, 81.03) * mm, "end": v(-92.46, 81.03) * mm});
            skLineSegment(sketch, "E6.2.1.1", {"start": v(-87.83, 76.41) * mm, "end": v(-87.83, 81.03) * mm});
            skLineSegment(sketch, "E6.2.1.2", {"start": v(-87.83, 76.41) * mm, "end": v(-92.46, 76.41) * mm});
            skLineSegment(sketch, "E6.2.1.3", {"start": v(-92.46, 76.41) * mm, "end": v(-92.46, 81.03) * mm});
            skLineSegment(sketch, "E6.2.2.0", {"start": v(-87.83, 68.33) * mm, "end": v(-92.46, 68.33) * mm});
            skLineSegment(sketch, "E6.2.2.1", {"start": v(-87.83, 63.71) * mm, "end": v(-87.83, 68.33) * mm});
            skLineSegment(sketch, "E6.2.2.2", {"start": v(-87.83, 63.71) * mm, "end": v(-92.46, 63.71) * mm});
            skLineSegment(sketch, "E6.2.2.3", {"start": v(-92.46, 63.71) * mm, "end": v(-92.46, 68.33) * mm});
            skLineSegment(sketch, "E6.2.3.0", {"start": v(-87.83, 55.63) * mm, "end": v(-92.46, 55.63) * mm});
            skLineSegment(sketch, "E6.2.3.1", {"start": v(-87.83, 51.01) * mm, "end": v(-87.83, 55.63) * mm});
            skLineSegment(sketch, "E6.2.3.2", {"start": v(-87.83, 51.01) * mm, "end": v(-92.46, 51.01) * mm});
            skLineSegment(sketch, "E6.2.3.3", {"start": v(-92.46, 51.01) * mm, "end": v(-92.46, 55.63) * mm});
            skLineSegment(sketch, "E6.2.4.0", {"start": v(-87.83, 42.93) * mm, "end": v(-92.46, 42.93) * mm});
            skLineSegment(sketch, "E6.2.4.1", {"start": v(-87.83, 38.31) * mm, "end": v(-87.83, 42.93) * mm});
            skLineSegment(sketch, "E6.2.4.2", {"start": v(-87.83, 38.31) * mm, "end": v(-92.46, 38.31) * mm});
            skLineSegment(sketch, "E6.2.4.3", {"start": v(-92.46, 38.31) * mm, "end": v(-92.46, 42.93) * mm});
            skLineSegment(sketch, "E6.2.5.0", {"start": v(-87.83, 30.23) * mm, "end": v(-92.46, 30.23) * mm});
            skLineSegment(sketch, "E6.2.5.1", {"start": v(-87.83, 25.61) * mm, "end": v(-87.83, 30.23) * mm});
            skLineSegment(sketch, "E6.2.5.2", {"start": v(-87.83, 25.61) * mm, "end": v(-92.46, 25.61) * mm});
            skLineSegment(sketch, "E6.2.5.3", {"start": v(-92.46, 25.61) * mm, "end": v(-92.46, 30.23) * mm});
            skLineSegment(sketch, "E6.2.6.0", {"start": v(-87.83, 17.53) * mm, "end": v(-92.46, 17.53) * mm});
            skLineSegment(sketch, "E6.2.6.1", {"start": v(-87.83, 12.91) * mm, "end": v(-87.83, 17.53) * mm});
            skLineSegment(sketch, "E6.2.6.2", {"start": v(-87.83, 12.91) * mm, "end": v(-92.46, 12.91) * mm});
            skLineSegment(sketch, "E6.2.6.3", {"start": v(-92.46, 12.91) * mm, "end": v(-92.46, 17.53) * mm});
            skLineSegment(sketch, "E6.2.7.0", {"start": v(-87.83, 4.83) * mm, "end": v(-92.46, 4.83) * mm});
            skLineSegment(sketch, "E6.2.7.1", {"start": v(-87.83, 0.21) * mm, "end": v(-87.83, 4.83) * mm});
            skLineSegment(sketch, "E6.2.7.2", {"start": v(-87.83, 0.21) * mm, "end": v(-92.46, 0.21) * mm});
            skLineSegment(sketch, "E6.2.7.3", {"start": v(-92.46, 0.21) * mm, "end": v(-92.46, 4.83) * mm});
            skLineSegment(sketch, "E6.2.8.0", {"start": v(-87.83, -7.87) * mm, "end": v(-92.46, -7.87) * mm});
            skLineSegment(sketch, "E6.2.8.1", {"start": v(-87.83, -12.49) * mm, "end": v(-87.83, -7.87) * mm});
            skLineSegment(sketch, "E6.2.8.2", {"start": v(-87.83, -12.49) * mm, "end": v(-92.46, -12.49) * mm});
            skLineSegment(sketch, "E6.2.8.3", {"start": v(-92.46, -12.49) * mm, "end": v(-92.46, -7.87) * mm});
            skLineSegment(sketch, "E6.2.9.0", {"start": v(-87.83, -20.57) * mm, "end": v(-92.46, -20.57) * mm});
            skLineSegment(sketch, "E6.2.9.1", {"start": v(-87.83, -25.19) * mm, "end": v(-87.83, -20.57) * mm});
            skLineSegment(sketch, "E6.2.9.2", {"start": v(-87.83, -25.19) * mm, "end": v(-92.46, -25.19) * mm});
            skLineSegment(sketch, "E6.2.9.3", {"start": v(-92.46, -25.19) * mm, "end": v(-92.46, -20.57) * mm});
            skLineSegment(sketch, "E6.2.10.0", {"start": v(-87.83, -33.27) * mm, "end": v(-92.46, -33.27) * mm});
            skLineSegment(sketch, "E6.2.10.1", {"start": v(-87.83, -37.89) * mm, "end": v(-87.83, -33.27) * mm});
            skLineSegment(sketch, "E6.2.10.2", {"start": v(-87.83, -37.89) * mm, "end": v(-92.46, -37.89) * mm});
            skLineSegment(sketch, "E6.2.10.3", {"start": v(-92.46, -37.89) * mm, "end": v(-92.46, -33.27) * mm});
            skLineSegment(sketch, "E6.2.11.0", {"start": v(-87.83, -45.97) * mm, "end": v(-92.46, -45.97) * mm});
            skLineSegment(sketch, "E6.2.11.1", {"start": v(-87.83, -50.59) * mm, "end": v(-87.83, -45.97) * mm});
            skLineSegment(sketch, "E6.2.11.2", {"start": v(-87.83, -50.59) * mm, "end": v(-92.46, -50.59) * mm});
            skLineSegment(sketch, "E6.2.11.3", {"start": v(-92.46, -50.59) * mm, "end": v(-92.46, -45.97) * mm});
            skLineSegment(sketch, "E6.2.12.0", {"start": v(-87.83, -58.67) * mm, "end": v(-92.46, -58.67) * mm});
            skLineSegment(sketch, "E6.2.12.1", {"start": v(-87.83, -63.29) * mm, "end": v(-87.83, -58.67) * mm});
            skLineSegment(sketch, "E6.2.12.2", {"start": v(-87.83, -63.29) * mm, "end": v(-92.46, -63.29) * mm});
            skLineSegment(sketch, "E6.2.12.3", {"start": v(-92.46, -63.29) * mm, "end": v(-92.46, -58.67) * mm});
            skLineSegment(sketch, "E6.3.0.0", {"start": v(-75.13, 93.73) * mm, "end": v(-79.76, 93.73) * mm});
            skLineSegment(sketch, "E6.3.0.1", {"start": v(-75.13, 89.11) * mm, "end": v(-75.13, 93.73) * mm});
            skLineSegment(sketch, "E6.3.0.2", {"start": v(-75.13, 89.11) * mm, "end": v(-79.76, 89.11) * mm});
            skLineSegment(sketch, "E6.3.0.3", {"start": v(-79.76, 89.11) * mm, "end": v(-79.76, 93.73) * mm});
            skLineSegment(sketch, "E6.3.1.0", {"start": v(-75.13, 81.03) * mm, "end": v(-79.76, 81.03) * mm});
            skLineSegment(sketch, "E6.3.1.1", {"start": v(-75.13, 76.41) * mm, "end": v(-75.13, 81.03) * mm});
            skLineSegment(sketch, "E6.3.1.2", {"start": v(-75.13, 76.41) * mm, "end": v(-79.76, 76.41) * mm});
            skLineSegment(sketch, "E6.3.1.3", {"start": v(-79.76, 76.41) * mm, "end": v(-79.76, 81.03) * mm});
            skLineSegment(sketch, "E6.3.2.0", {"start": v(-75.13, 68.33) * mm, "end": v(-79.76, 68.33) * mm});
            skLineSegment(sketch, "E6.3.2.1", {"start": v(-75.13, 63.71) * mm, "end": v(-75.13, 68.33) * mm});
            skLineSegment(sketch, "E6.3.2.2", {"start": v(-75.13, 63.71) * mm, "end": v(-79.76, 63.71) * mm});
            skLineSegment(sketch, "E6.3.2.3", {"start": v(-79.76, 63.71) * mm, "end": v(-79.76, 68.33) * mm});
            skLineSegment(sketch, "E6.3.3.0", {"start": v(-75.13, 55.63) * mm, "end": v(-79.76, 55.63) * mm});
            skLineSegment(sketch, "E6.3.3.1", {"start": v(-75.13, 51.01) * mm, "end": v(-75.13, 55.63) * mm});
            skLineSegment(sketch, "E6.3.3.2", {"start": v(-75.13, 51.01) * mm, "end": v(-79.76, 51.01) * mm});
            skLineSegment(sketch, "E6.3.3.3", {"start": v(-79.76, 51.01) * mm, "end": v(-79.76, 55.63) * mm});
            skLineSegment(sketch, "E6.3.4.0", {"start": v(-75.13, 42.93) * mm, "end": v(-79.76, 42.93) * mm});
            skLineSegment(sketch, "E6.3.4.1", {"start": v(-75.13, 38.31) * mm, "end": v(-75.13, 42.93) * mm});
            skLineSegment(sketch, "E6.3.4.2", {"start": v(-75.13, 38.31) * mm, "end": v(-79.76, 38.31) * mm});
            skLineSegment(sketch, "E6.3.4.3", {"start": v(-79.76, 38.31) * mm, "end": v(-79.76, 42.93) * mm});
            skLineSegment(sketch, "E6.3.5.0", {"start": v(-75.13, 30.23) * mm, "end": v(-79.76, 30.23) * mm});
            skLineSegment(sketch, "E6.3.5.1", {"start": v(-75.13, 25.61) * mm, "end": v(-75.13, 30.23) * mm});
            skLineSegment(sketch, "E6.3.5.2", {"start": v(-75.13, 25.61) * mm, "end": v(-79.76, 25.61) * mm});
            skLineSegment(sketch, "E6.3.5.3", {"start": v(-79.76, 25.61) * mm, "end": v(-79.76, 30.23) * mm});
            skLineSegment(sketch, "E6.3.6.0", {"start": v(-75.13, 17.53) * mm, "end": v(-79.76, 17.53) * mm});
            skLineSegment(sketch, "E6.3.6.1", {"start": v(-75.13, 12.91) * mm, "end": v(-75.13, 17.53) * mm});
            skLineSegment(sketch, "E6.3.6.2", {"start": v(-75.13, 12.91) * mm, "end": v(-79.76, 12.91) * mm});
            skLineSegment(sketch, "E6.3.6.3", {"start": v(-79.76, 12.91) * mm, "end": v(-79.76, 17.53) * mm});
            skLineSegment(sketch, "E6.3.7.0", {"start": v(-75.13, 4.83) * mm, "end": v(-79.76, 4.83) * mm});
            skLineSegment(sketch, "E6.3.7.1", {"start": v(-75.13, 0.21) * mm, "end": v(-75.13, 4.83) * mm});
            skLineSegment(sketch, "E6.3.7.2", {"start": v(-75.13, 0.21) * mm, "end": v(-79.76, 0.21) * mm});
            skLineSegment(sketch, "E6.3.7.3", {"start": v(-79.76, 0.21) * mm, "end": v(-79.76, 4.83) * mm});
            skLineSegment(sketch, "E6.3.8.0", {"start": v(-75.13, -7.87) * mm, "end": v(-79.76, -7.87) * mm});
            skLineSegment(sketch, "E6.3.8.1", {"start": v(-75.13, -12.49) * mm, "end": v(-75.13, -7.87) * mm});
            skLineSegment(sketch, "E6.3.8.2", {"start": v(-75.13, -12.49) * mm, "end": v(-79.76, -12.49) * mm});
            skLineSegment(sketch, "E6.3.8.3", {"start": v(-79.76, -12.49) * mm, "end": v(-79.76, -7.87) * mm});
            skLineSegment(sketch, "E6.3.9.0", {"start": v(-75.13, -20.57) * mm, "end": v(-79.76, -20.57) * mm});
            skLineSegment(sketch, "E6.3.9.1", {"start": v(-75.13, -25.19) * mm, "end": v(-75.13, -20.57) * mm});
            skLineSegment(sketch, "E6.3.9.2", {"start": v(-75.13, -25.19) * mm, "end": v(-79.76, -25.19) * mm});
            skLineSegment(sketch, "E6.3.9.3", {"start": v(-79.76, -25.19) * mm, "end": v(-79.76, -20.57) * mm});
            skLineSegment(sketch, "E6.3.10.0", {"start": v(-75.13, -33.27) * mm, "end": v(-79.76, -33.27) * mm});
            skLineSegment(sketch, "E6.3.10.1", {"start": v(-75.13, -37.89) * mm, "end": v(-75.13, -33.27) * mm});
            skLineSegment(sketch, "E6.3.10.2", {"start": v(-75.13, -37.89) * mm, "end": v(-79.76, -37.89) * mm});
            skLineSegment(sketch, "E6.3.10.3", {"start": v(-79.76, -37.89) * mm, "end": v(-79.76, -33.27) * mm});
            skLineSegment(sketch, "E6.3.11.0", {"start": v(-75.13, -45.97) * mm, "end": v(-79.76, -45.97) * mm});
            skLineSegment(sketch, "E6.3.11.1", {"start": v(-75.13, -50.59) * mm, "end": v(-75.13, -45.97) * mm});
            skLineSegment(sketch, "E6.3.11.2", {"start": v(-75.13, -50.59) * mm, "end": v(-79.76, -50.59) * mm});
            skLineSegment(sketch, "E6.3.11.3", {"start": v(-79.76, -50.59) * mm, "end": v(-79.76, -45.97) * mm});
            skLineSegment(sketch, "E6.3.12.0", {"start": v(-75.13, -58.67) * mm, "end": v(-79.76, -58.67) * mm});
            skLineSegment(sketch, "E6.3.12.1", {"start": v(-75.13, -63.29) * mm, "end": v(-75.13, -58.67) * mm});
            skLineSegment(sketch, "E6.3.12.2", {"start": v(-75.13, -63.29) * mm, "end": v(-79.76, -63.29) * mm});
            skLineSegment(sketch, "E6.3.12.3", {"start": v(-79.76, -63.29) * mm, "end": v(-79.76, -58.67) * mm});
            skLineSegment(sketch, "E6.4.0.0", {"start": v(-62.43, 93.73) * mm, "end": v(-67.06, 93.73) * mm});
            skLineSegment(sketch, "E6.4.0.1", {"start": v(-62.43, 89.11) * mm, "end": v(-62.43, 93.73) * mm});
            skLineSegment(sketch, "E6.4.0.2", {"start": v(-62.43, 89.11) * mm, "end": v(-67.06, 89.11) * mm});
            skLineSegment(sketch, "E6.4.0.3", {"start": v(-67.06, 89.11) * mm, "end": v(-67.06, 93.73) * mm});
            skLineSegment(sketch, "E6.4.1.0", {"start": v(-62.43, 81.03) * mm, "end": v(-67.06, 81.03) * mm});
            skLineSegment(sketch, "E6.4.1.1", {"start": v(-62.43, 76.41) * mm, "end": v(-62.43, 81.03) * mm});
            skLineSegment(sketch, "E6.4.1.2", {"start": v(-62.43, 76.41) * mm, "end": v(-67.06, 76.41) * mm});
            skLineSegment(sketch, "E6.4.1.3", {"start": v(-67.06, 76.41) * mm, "end": v(-67.06, 81.03) * mm});
            skLineSegment(sketch, "E6.4.2.0", {"start": v(-62.43, 68.33) * mm, "end": v(-67.06, 68.33) * mm});
            skLineSegment(sketch, "E6.4.2.1", {"start": v(-62.43, 63.71) * mm, "end": v(-62.43, 68.33) * mm});
            skLineSegment(sketch, "E6.4.2.2", {"start": v(-62.43, 63.71) * mm, "end": v(-67.06, 63.71) * mm});
            skLineSegment(sketch, "E6.4.2.3", {"start": v(-67.06, 63.71) * mm, "end": v(-67.06, 68.33) * mm});
            skLineSegment(sketch, "E6.4.3.0", {"start": v(-62.43, 55.63) * mm, "end": v(-67.06, 55.63) * mm});
            skLineSegment(sketch, "E6.4.3.1", {"start": v(-62.43, 51.01) * mm, "end": v(-62.43, 55.63) * mm});
            skLineSegment(sketch, "E6.4.3.2", {"start": v(-62.43, 51.01) * mm, "end": v(-67.06, 51.01) * mm});
            skLineSegment(sketch, "E6.4.3.3", {"start": v(-67.06, 51.01) * mm, "end": v(-67.06, 55.63) * mm});
            skLineSegment(sketch, "E6.4.4.0", {"start": v(-62.43, 42.93) * mm, "end": v(-67.06, 42.93) * mm});
            skLineSegment(sketch, "E6.4.4.1", {"start": v(-62.43, 38.31) * mm, "end": v(-62.43, 42.93) * mm});
            skLineSegment(sketch, "E6.4.4.2", {"start": v(-62.43, 38.31) * mm, "end": v(-67.06, 38.31) * mm});
            skLineSegment(sketch, "E6.4.4.3", {"start": v(-67.06, 38.31) * mm, "end": v(-67.06, 42.93) * mm});
            skLineSegment(sketch, "E6.4.5.0", {"start": v(-62.43, 30.23) * mm, "end": v(-67.06, 30.23) * mm});
            skLineSegment(sketch, "E6.4.5.1", {"start": v(-62.43, 25.61) * mm, "end": v(-62.43, 30.23) * mm});
            skLineSegment(sketch, "E6.4.5.2", {"start": v(-62.43, 25.61) * mm, "end": v(-67.06, 25.61) * mm});
            skLineSegment(sketch, "E6.4.5.3", {"start": v(-67.06, 25.61) * mm, "end": v(-67.06, 30.23) * mm});
            skLineSegment(sketch, "E6.4.6.0", {"start": v(-62.43, 17.53) * mm, "end": v(-67.06, 17.53) * mm});
            skLineSegment(sketch, "E6.4.6.1", {"start": v(-62.43, 12.91) * mm, "end": v(-62.43, 17.53) * mm});
            skLineSegment(sketch, "E6.4.6.2", {"start": v(-62.43, 12.91) * mm, "end": v(-67.06, 12.91) * mm});
            skLineSegment(sketch, "E6.4.6.3", {"start": v(-67.06, 12.91) * mm, "end": v(-67.06, 17.53) * mm});
            skLineSegment(sketch, "E6.4.7.0", {"start": v(-62.43, 4.83) * mm, "end": v(-67.06, 4.83) * mm});
            skLineSegment(sketch, "E6.4.7.1", {"start": v(-62.43, 0.21) * mm, "end": v(-62.43, 4.83) * mm});
            skLineSegment(sketch, "E6.4.7.2", {"start": v(-62.43, 0.21) * mm, "end": v(-67.06, 0.21) * mm});
            skLineSegment(sketch, "E6.4.7.3", {"start": v(-67.06, 0.21) * mm, "end": v(-67.06, 4.83) * mm});
            skLineSegment(sketch, "E6.4.8.0", {"start": v(-62.43, -7.87) * mm, "end": v(-67.06, -7.87) * mm});
            skLineSegment(sketch, "E6.4.8.1", {"start": v(-62.43, -12.49) * mm, "end": v(-62.43, -7.87) * mm});
            skLineSegment(sketch, "E6.4.8.2", {"start": v(-62.43, -12.49) * mm, "end": v(-67.06, -12.49) * mm});
            skLineSegment(sketch, "E6.4.8.3", {"start": v(-67.06, -12.49) * mm, "end": v(-67.06, -7.87) * mm});
            skLineSegment(sketch, "E6.4.9.0", {"start": v(-62.43, -20.57) * mm, "end": v(-67.06, -20.57) * mm});
            skLineSegment(sketch, "E6.4.9.1", {"start": v(-62.43, -25.19) * mm, "end": v(-62.43, -20.57) * mm});
            skLineSegment(sketch, "E6.4.9.2", {"start": v(-62.43, -25.19) * mm, "end": v(-67.06, -25.19) * mm});
            skLineSegment(sketch, "E6.4.9.3", {"start": v(-67.06, -25.19) * mm, "end": v(-67.06, -20.57) * mm});
            skLineSegment(sketch, "E6.4.10.0", {"start": v(-62.43, -33.27) * mm, "end": v(-67.06, -33.27) * mm});
            skLineSegment(sketch, "E6.4.10.1", {"start": v(-62.43, -37.89) * mm, "end": v(-62.43, -33.27) * mm});
            skLineSegment(sketch, "E6.4.10.2", {"start": v(-62.43, -37.89) * mm, "end": v(-67.06, -37.89) * mm});
            skLineSegment(sketch, "E6.4.10.3", {"start": v(-67.06, -37.89) * mm, "end": v(-67.06, -33.27) * mm});
            skLineSegment(sketch, "E6.4.11.0", {"start": v(-62.43, -45.97) * mm, "end": v(-67.06, -45.97) * mm});
            skLineSegment(sketch, "E6.4.11.1", {"start": v(-62.43, -50.59) * mm, "end": v(-62.43, -45.97) * mm});
            skLineSegment(sketch, "E6.4.11.2", {"start": v(-62.43, -50.59) * mm, "end": v(-67.06, -50.59) * mm});
            skLineSegment(sketch, "E6.4.11.3", {"start": v(-67.06, -50.59) * mm, "end": v(-67.06, -45.97) * mm});
            skLineSegment(sketch, "E6.4.12.0", {"start": v(-62.43, -58.67) * mm, "end": v(-67.06, -58.67) * mm});
            skLineSegment(sketch, "E6.4.12.1", {"start": v(-62.43, -63.29) * mm, "end": v(-62.43, -58.67) * mm});
            skLineSegment(sketch, "E6.4.12.2", {"start": v(-62.43, -63.29) * mm, "end": v(-67.06, -63.29) * mm});
            skLineSegment(sketch, "E6.4.12.3", {"start": v(-67.06, -63.29) * mm, "end": v(-67.06, -58.67) * mm});
            skLineSegment(sketch, "E6.5.0.0", {"start": v(-49.73, 93.73) * mm, "end": v(-54.36, 93.73) * mm});
            skLineSegment(sketch, "E6.5.0.1", {"start": v(-49.73, 89.11) * mm, "end": v(-49.73, 93.73) * mm});
            skLineSegment(sketch, "E6.5.0.2", {"start": v(-49.73, 89.11) * mm, "end": v(-54.36, 89.11) * mm});
            skLineSegment(sketch, "E6.5.0.3", {"start": v(-54.36, 89.11) * mm, "end": v(-54.36, 93.73) * mm});
            skLineSegment(sketch, "E6.5.1.0", {"start": v(-49.73, 81.03) * mm, "end": v(-54.36, 81.03) * mm});
            skLineSegment(sketch, "E6.5.1.1", {"start": v(-49.73, 76.41) * mm, "end": v(-49.73, 81.03) * mm});
            skLineSegment(sketch, "E6.5.1.2", {"start": v(-49.73, 76.41) * mm, "end": v(-54.36, 76.41) * mm});
            skLineSegment(sketch, "E6.5.1.3", {"start": v(-54.36, 76.41) * mm, "end": v(-54.36, 81.03) * mm});
            skLineSegment(sketch, "E6.5.2.0", {"start": v(-49.73, 68.33) * mm, "end": v(-54.36, 68.33) * mm});
            skLineSegment(sketch, "E6.5.2.1", {"start": v(-49.73, 63.71) * mm, "end": v(-49.73, 68.33) * mm});
            skLineSegment(sketch, "E6.5.2.2", {"start": v(-49.73, 63.71) * mm, "end": v(-54.36, 63.71) * mm});
            skLineSegment(sketch, "E6.5.2.3", {"start": v(-54.36, 63.71) * mm, "end": v(-54.36, 68.33) * mm});
            skLineSegment(sketch, "E6.5.3.0", {"start": v(-49.73, 55.63) * mm, "end": v(-54.36, 55.63) * mm});
            skLineSegment(sketch, "E6.5.3.1", {"start": v(-49.73, 51.01) * mm, "end": v(-49.73, 55.63) * mm});
            skLineSegment(sketch, "E6.5.3.2", {"start": v(-49.73, 51.01) * mm, "end": v(-54.36, 51.01) * mm});
            skLineSegment(sketch, "E6.5.3.3", {"start": v(-54.36, 51.01) * mm, "end": v(-54.36, 55.63) * mm});
            skLineSegment(sketch, "E6.5.4.0", {"start": v(-49.73, 42.93) * mm, "end": v(-54.36, 42.93) * mm});
            skLineSegment(sketch, "E6.5.4.1", {"start": v(-49.73, 38.31) * mm, "end": v(-49.73, 42.93) * mm});
            skLineSegment(sketch, "E6.5.4.2", {"start": v(-49.73, 38.31) * mm, "end": v(-54.36, 38.31) * mm});
            skLineSegment(sketch, "E6.5.4.3", {"start": v(-54.36, 38.31) * mm, "end": v(-54.36, 42.93) * mm});
            skLineSegment(sketch, "E6.5.5.0", {"start": v(-49.73, 30.23) * mm, "end": v(-54.36, 30.23) * mm});
            skLineSegment(sketch, "E6.5.5.1", {"start": v(-49.73, 25.61) * mm, "end": v(-49.73, 30.23) * mm});
            skLineSegment(sketch, "E6.5.5.2", {"start": v(-49.73, 25.61) * mm, "end": v(-54.36, 25.61) * mm});
            skLineSegment(sketch, "E6.5.5.3", {"start": v(-54.36, 25.61) * mm, "end": v(-54.36, 30.23) * mm});
            skLineSegment(sketch, "E6.5.6.0", {"start": v(-49.73, 17.53) * mm, "end": v(-54.36, 17.53) * mm});
            skLineSegment(sketch, "E6.5.6.1", {"start": v(-49.73, 12.91) * mm, "end": v(-49.73, 17.53) * mm});
            skLineSegment(sketch, "E6.5.6.2", {"start": v(-49.73, 12.91) * mm, "end": v(-54.36, 12.91) * mm});
            skLineSegment(sketch, "E6.5.6.3", {"start": v(-54.36, 12.91) * mm, "end": v(-54.36, 17.53) * mm});
            skLineSegment(sketch, "E6.5.7.0", {"start": v(-49.73, 4.83) * mm, "end": v(-54.36, 4.83) * mm});
            skLineSegment(sketch, "E6.5.7.1", {"start": v(-49.73, 0.21) * mm, "end": v(-49.73, 4.83) * mm});
            skLineSegment(sketch, "E6.5.7.2", {"start": v(-49.73, 0.21) * mm, "end": v(-54.36, 0.21) * mm});
            skLineSegment(sketch, "E6.5.7.3", {"start": v(-54.36, 0.21) * mm, "end": v(-54.36, 4.83) * mm});
            skLineSegment(sketch, "E6.5.8.0", {"start": v(-49.73, -7.87) * mm, "end": v(-54.36, -7.87) * mm});
            skLineSegment(sketch, "E6.5.8.1", {"start": v(-49.73, -12.49) * mm, "end": v(-49.73, -7.87) * mm});
            skLineSegment(sketch, "E6.5.8.2", {"start": v(-49.73, -12.49) * mm, "end": v(-54.36, -12.49) * mm});
            skLineSegment(sketch, "E6.5.8.3", {"start": v(-54.36, -12.49) * mm, "end": v(-54.36, -7.87) * mm});
            skLineSegment(sketch, "E6.5.9.0", {"start": v(-49.73, -20.57) * mm, "end": v(-54.36, -20.57) * mm});
            skLineSegment(sketch, "E6.5.9.1", {"start": v(-49.73, -25.19) * mm, "end": v(-49.73, -20.57) * mm});
            skLineSegment(sketch, "E6.5.9.2", {"start": v(-49.73, -25.19) * mm, "end": v(-54.36, -25.19) * mm});
            skLineSegment(sketch, "E6.5.9.3", {"start": v(-54.36, -25.19) * mm, "end": v(-54.36, -20.57) * mm});
            skLineSegment(sketch, "E6.5.10.0", {"start": v(-49.73, -33.27) * mm, "end": v(-54.36, -33.27) * mm});
            skLineSegment(sketch, "E6.5.10.1", {"start": v(-49.73, -37.89) * mm, "end": v(-49.73, -33.27) * mm});
            skLineSegment(sketch, "E6.5.10.2", {"start": v(-49.73, -37.89) * mm, "end": v(-54.36, -37.89) * mm});
            skLineSegment(sketch, "E6.5.10.3", {"start": v(-54.36, -37.89) * mm, "end": v(-54.36, -33.27) * mm});
            skLineSegment(sketch, "E6.5.11.0", {"start": v(-49.73, -45.97) * mm, "end": v(-54.36, -45.97) * mm});
            skLineSegment(sketch, "E6.5.11.1", {"start": v(-49.73, -50.59) * mm, "end": v(-49.73, -45.97) * mm});
            skLineSegment(sketch, "E6.5.11.2", {"start": v(-49.73, -50.59) * mm, "end": v(-54.36, -50.59) * mm});
            skLineSegment(sketch, "E6.5.11.3", {"start": v(-54.36, -50.59) * mm, "end": v(-54.36, -45.97) * mm});
            skLineSegment(sketch, "E6.5.12.0", {"start": v(-49.73, -58.67) * mm, "end": v(-54.36, -58.67) * mm});
            skLineSegment(sketch, "E6.5.12.1", {"start": v(-49.73, -63.29) * mm, "end": v(-49.73, -58.67) * mm});
            skLineSegment(sketch, "E6.5.12.2", {"start": v(-49.73, -63.29) * mm, "end": v(-54.36, -63.29) * mm});
            skLineSegment(sketch, "E6.5.12.3", {"start": v(-54.36, -63.29) * mm, "end": v(-54.36, -58.67) * mm});
            skLineSegment(sketch, "E6.6.0.0", {"start": v(-37.03, 93.73) * mm, "end": v(-41.66, 93.73) * mm});
            skLineSegment(sketch, "E6.6.0.1", {"start": v(-37.03, 89.11) * mm, "end": v(-37.03, 93.73) * mm});
            skLineSegment(sketch, "E6.6.0.2", {"start": v(-37.03, 89.11) * mm, "end": v(-41.66, 89.11) * mm});
            skLineSegment(sketch, "E6.6.0.3", {"start": v(-41.66, 89.11) * mm, "end": v(-41.66, 93.73) * mm});
            skLineSegment(sketch, "E6.6.1.0", {"start": v(-37.03, 81.03) * mm, "end": v(-41.66, 81.03) * mm});
            skLineSegment(sketch, "E6.6.1.1", {"start": v(-37.03, 76.41) * mm, "end": v(-37.03, 81.03) * mm});
            skLineSegment(sketch, "E6.6.1.2", {"start": v(-37.03, 76.41) * mm, "end": v(-41.66, 76.41) * mm});
            skLineSegment(sketch, "E6.6.1.3", {"start": v(-41.66, 76.41) * mm, "end": v(-41.66, 81.03) * mm});
            skLineSegment(sketch, "E6.6.2.0", {"start": v(-37.03, 68.33) * mm, "end": v(-41.66, 68.33) * mm});
            skLineSegment(sketch, "E6.6.2.1", {"start": v(-37.03, 63.71) * mm, "end": v(-37.03, 68.33) * mm});
            skLineSegment(sketch, "E6.6.2.2", {"start": v(-37.03, 63.71) * mm, "end": v(-41.66, 63.71) * mm});
            skLineSegment(sketch, "E6.6.2.3", {"start": v(-41.66, 63.71) * mm, "end": v(-41.66, 68.33) * mm});
            skLineSegment(sketch, "E6.6.3.0", {"start": v(-37.03, 55.63) * mm, "end": v(-41.66, 55.63) * mm});
            skLineSegment(sketch, "E6.6.3.1", {"start": v(-37.03, 51.01) * mm, "end": v(-37.03, 55.63) * mm});
            skLineSegment(sketch, "E6.6.3.2", {"start": v(-37.03, 51.01) * mm, "end": v(-41.66, 51.01) * mm});
            skLineSegment(sketch, "E6.6.3.3", {"start": v(-41.66, 51.01) * mm, "end": v(-41.66, 55.63) * mm});
            skLineSegment(sketch, "E6.6.4.0", {"start": v(-37.03, 42.93) * mm, "end": v(-41.66, 42.93) * mm});
            skLineSegment(sketch, "E6.6.4.1", {"start": v(-37.03, 38.31) * mm, "end": v(-37.03, 42.93) * mm});
            skLineSegment(sketch, "E6.6.4.2", {"start": v(-37.03, 38.31) * mm, "end": v(-41.66, 38.31) * mm});
            skLineSegment(sketch, "E6.6.4.3", {"start": v(-41.66, 38.31) * mm, "end": v(-41.66, 42.93) * mm});
            skLineSegment(sketch, "E6.6.5.0", {"start": v(-37.03, 30.23) * mm, "end": v(-41.66, 30.23) * mm});
            skLineSegment(sketch, "E6.6.5.1", {"start": v(-37.03, 25.61) * mm, "end": v(-37.03, 30.23) * mm});
            skLineSegment(sketch, "E6.6.5.2", {"start": v(-37.03, 25.61) * mm, "end": v(-41.66, 25.61) * mm});
            skLineSegment(sketch, "E6.6.5.3", {"start": v(-41.66, 25.61) * mm, "end": v(-41.66, 30.23) * mm});
            skLineSegment(sketch, "E6.6.6.0", {"start": v(-37.03, 17.53) * mm, "end": v(-41.66, 17.53) * mm});
            skLineSegment(sketch, "E6.6.6.1", {"start": v(-37.03, 12.91) * mm, "end": v(-37.03, 17.53) * mm});
            skLineSegment(sketch, "E6.6.6.2", {"start": v(-37.03, 12.91) * mm, "end": v(-41.66, 12.91) * mm});
            skLineSegment(sketch, "E6.6.6.3", {"start": v(-41.66, 12.91) * mm, "end": v(-41.66, 17.53) * mm});
            skLineSegment(sketch, "E6.6.7.0", {"start": v(-37.03, 4.83) * mm, "end": v(-41.66, 4.83) * mm});
            skLineSegment(sketch, "E6.6.7.1", {"start": v(-37.03, 0.21) * mm, "end": v(-37.03, 4.83) * mm});
            skLineSegment(sketch, "E6.6.7.2", {"start": v(-37.03, 0.21) * mm, "end": v(-41.66, 0.21) * mm});
            skLineSegment(sketch, "E6.6.7.3", {"start": v(-41.66, 0.21) * mm, "end": v(-41.66, 4.83) * mm});
            skLineSegment(sketch, "E6.6.8.0", {"start": v(-37.03, -7.87) * mm, "end": v(-41.66, -7.87) * mm});
            skLineSegment(sketch, "E6.6.8.1", {"start": v(-37.03, -12.49) * mm, "end": v(-37.03, -7.87) * mm});
            skLineSegment(sketch, "E6.6.8.2", {"start": v(-37.03, -12.49) * mm, "end": v(-41.66, -12.49) * mm});
            skLineSegment(sketch, "E6.6.8.3", {"start": v(-41.66, -12.49) * mm, "end": v(-41.66, -7.87) * mm});
            skLineSegment(sketch, "E6.6.9.0", {"start": v(-37.03, -20.57) * mm, "end": v(-41.66, -20.57) * mm});
            skLineSegment(sketch, "E6.6.9.1", {"start": v(-37.03, -25.19) * mm, "end": v(-37.03, -20.57) * mm});
            skLineSegment(sketch, "E6.6.9.2", {"start": v(-37.03, -25.19) * mm, "end": v(-41.66, -25.19) * mm});
            skLineSegment(sketch, "E6.6.9.3", {"start": v(-41.66, -25.19) * mm, "end": v(-41.66, -20.57) * mm});
            skLineSegment(sketch, "E6.6.10.0", {"start": v(-37.03, -33.27) * mm, "end": v(-41.66, -33.27) * mm});
            skLineSegment(sketch, "E6.6.10.1", {"start": v(-37.03, -37.89) * mm, "end": v(-37.03, -33.27) * mm});
            skLineSegment(sketch, "E6.6.10.2", {"start": v(-37.03, -37.89) * mm, "end": v(-41.66, -37.89) * mm});
            skLineSegment(sketch, "E6.6.10.3", {"start": v(-41.66, -37.89) * mm, "end": v(-41.66, -33.27) * mm});
            skLineSegment(sketch, "E6.6.11.0", {"start": v(-37.03, -45.97) * mm, "end": v(-41.66, -45.97) * mm});
            skLineSegment(sketch, "E6.6.11.1", {"start": v(-37.03, -50.59) * mm, "end": v(-37.03, -45.97) * mm});
            skLineSegment(sketch, "E6.6.11.2", {"start": v(-37.03, -50.59) * mm, "end": v(-41.66, -50.59) * mm});
            skLineSegment(sketch, "E6.6.11.3", {"start": v(-41.66, -50.59) * mm, "end": v(-41.66, -45.97) * mm});
            skLineSegment(sketch, "E6.6.12.0", {"start": v(-37.03, -58.67) * mm, "end": v(-41.66, -58.67) * mm});
            skLineSegment(sketch, "E6.6.12.1", {"start": v(-37.03, -63.29) * mm, "end": v(-37.03, -58.67) * mm});
            skLineSegment(sketch, "E6.6.12.2", {"start": v(-37.03, -63.29) * mm, "end": v(-41.66, -63.29) * mm});
            skLineSegment(sketch, "E6.6.12.3", {"start": v(-41.66, -63.29) * mm, "end": v(-41.66, -58.67) * mm});
            skLineSegment(sketch, "E6.7.0.0", {"start": v(-24.33, 93.73) * mm, "end": v(-28.96, 93.73) * mm});
            skLineSegment(sketch, "E6.7.0.1", {"start": v(-24.33, 89.11) * mm, "end": v(-24.33, 93.73) * mm});
            skLineSegment(sketch, "E6.7.0.2", {"start": v(-24.33, 89.11) * mm, "end": v(-28.96, 89.11) * mm});
            skLineSegment(sketch, "E6.7.0.3", {"start": v(-28.96, 89.11) * mm, "end": v(-28.96, 93.73) * mm});
            skLineSegment(sketch, "E6.7.1.0", {"start": v(-24.33, 81.03) * mm, "end": v(-28.96, 81.03) * mm});
            skLineSegment(sketch, "E6.7.1.1", {"start": v(-24.33, 76.41) * mm, "end": v(-24.33, 81.03) * mm});
            skLineSegment(sketch, "E6.7.1.2", {"start": v(-24.33, 76.41) * mm, "end": v(-28.96, 76.41) * mm});
            skLineSegment(sketch, "E6.7.1.3", {"start": v(-28.96, 76.41) * mm, "end": v(-28.96, 81.03) * mm});
            skLineSegment(sketch, "E6.7.2.0", {"start": v(-24.33, 68.33) * mm, "end": v(-28.96, 68.33) * mm});
            skLineSegment(sketch, "E6.7.2.1", {"start": v(-24.33, 63.71) * mm, "end": v(-24.33, 68.33) * mm});
            skLineSegment(sketch, "E6.7.2.2", {"start": v(-24.33, 63.71) * mm, "end": v(-28.96, 63.71) * mm});
            skLineSegment(sketch, "E6.7.2.3", {"start": v(-28.96, 63.71) * mm, "end": v(-28.96, 68.33) * mm});
            skLineSegment(sketch, "E6.7.3.0", {"start": v(-24.33, 55.63) * mm, "end": v(-28.96, 55.63) * mm});
            skLineSegment(sketch, "E6.7.3.1", {"start": v(-24.33, 51.01) * mm, "end": v(-24.33, 55.63) * mm});
            skLineSegment(sketch, "E6.7.3.2", {"start": v(-24.33, 51.01) * mm, "end": v(-28.96, 51.01) * mm});
            skLineSegment(sketch, "E6.7.3.3", {"start": v(-28.96, 51.01) * mm, "end": v(-28.96, 55.63) * mm});
            skLineSegment(sketch, "E6.7.4.0", {"start": v(-24.33, 42.93) * mm, "end": v(-28.96, 42.93) * mm});
            skLineSegment(sketch, "E6.7.4.1", {"start": v(-24.33, 38.31) * mm, "end": v(-24.33, 42.93) * mm});
            skLineSegment(sketch, "E6.7.4.2", {"start": v(-24.33, 38.31) * mm, "end": v(-28.96, 38.31) * mm});
            skLineSegment(sketch, "E6.7.4.3", {"start": v(-28.96, 38.31) * mm, "end": v(-28.96, 42.93) * mm});
            skLineSegment(sketch, "E6.7.5.0", {"start": v(-24.33, 30.23) * mm, "end": v(-28.96, 30.23) * mm});
            skLineSegment(sketch, "E6.7.5.1", {"start": v(-24.33, 25.61) * mm, "end": v(-24.33, 30.23) * mm});
            skLineSegment(sketch, "E6.7.5.2", {"start": v(-24.33, 25.61) * mm, "end": v(-28.96, 25.61) * mm});
            skLineSegment(sketch, "E6.7.5.3", {"start": v(-28.96, 25.61) * mm, "end": v(-28.96, 30.23) * mm});
            skLineSegment(sketch, "E6.7.6.0", {"start": v(-24.33, 17.53) * mm, "end": v(-28.96, 17.53) * mm});
            skLineSegment(sketch, "E6.7.6.1", {"start": v(-24.33, 12.91) * mm, "end": v(-24.33, 17.53) * mm});
            skLineSegment(sketch, "E6.7.6.2", {"start": v(-24.33, 12.91) * mm, "end": v(-28.96, 12.91) * mm});
            skLineSegment(sketch, "E6.7.6.3", {"start": v(-28.96, 12.91) * mm, "end": v(-28.96, 17.53) * mm});
            skLineSegment(sketch, "E6.7.7.0", {"start": v(-24.33, 4.83) * mm, "end": v(-28.96, 4.83) * mm});
            skLineSegment(sketch, "E6.7.7.1", {"start": v(-24.33, 0.21) * mm, "end": v(-24.33, 4.83) * mm});
            skLineSegment(sketch, "E6.7.7.2", {"start": v(-24.33, 0.21) * mm, "end": v(-28.96, 0.21) * mm});
            skLineSegment(sketch, "E6.7.7.3", {"start": v(-28.96, 0.21) * mm, "end": v(-28.96, 4.83) * mm});
            skLineSegment(sketch, "E6.7.8.0", {"start": v(-24.33, -7.87) * mm, "end": v(-28.96, -7.87) * mm});
            skLineSegment(sketch, "E6.7.8.1", {"start": v(-24.33, -12.49) * mm, "end": v(-24.33, -7.87) * mm});
            skLineSegment(sketch, "E6.7.8.2", {"start": v(-24.33, -12.49) * mm, "end": v(-28.96, -12.49) * mm});
            skLineSegment(sketch, "E6.7.8.3", {"start": v(-28.96, -12.49) * mm, "end": v(-28.96, -7.87) * mm});
            skLineSegment(sketch, "E6.7.9.0", {"start": v(-24.33, -20.57) * mm, "end": v(-28.96, -20.57) * mm});
            skLineSegment(sketch, "E6.7.9.1", {"start": v(-24.33, -25.19) * mm, "end": v(-24.33, -20.57) * mm});
            skLineSegment(sketch, "E6.7.9.2", {"start": v(-24.33, -25.19) * mm, "end": v(-28.96, -25.19) * mm});
            skLineSegment(sketch, "E6.7.9.3", {"start": v(-28.96, -25.19) * mm, "end": v(-28.96, -20.57) * mm});
            skLineSegment(sketch, "E6.7.10.0", {"start": v(-24.33, -33.27) * mm, "end": v(-28.96, -33.27) * mm});
            skLineSegment(sketch, "E6.7.10.1", {"start": v(-24.33, -37.89) * mm, "end": v(-24.33, -33.27) * mm});
            skLineSegment(sketch, "E6.7.10.2", {"start": v(-24.33, -37.89) * mm, "end": v(-28.96, -37.89) * mm});
            skLineSegment(sketch, "E6.7.10.3", {"start": v(-28.96, -37.89) * mm, "end": v(-28.96, -33.27) * mm});
            skLineSegment(sketch, "E6.7.11.0", {"start": v(-24.33, -45.97) * mm, "end": v(-28.96, -45.97) * mm});
            skLineSegment(sketch, "E6.7.11.1", {"start": v(-24.33, -50.59) * mm, "end": v(-24.33, -45.97) * mm});
            skLineSegment(sketch, "E6.7.11.2", {"start": v(-24.33, -50.59) * mm, "end": v(-28.96, -50.59) * mm});
            skLineSegment(sketch, "E6.7.11.3", {"start": v(-28.96, -50.59) * mm, "end": v(-28.96, -45.97) * mm});
            skLineSegment(sketch, "E6.7.12.0", {"start": v(-24.33, -58.67) * mm, "end": v(-28.96, -58.67) * mm});
            skLineSegment(sketch, "E6.7.12.1", {"start": v(-24.33, -63.29) * mm, "end": v(-24.33, -58.67) * mm});
            skLineSegment(sketch, "E6.7.12.2", {"start": v(-24.33, -63.29) * mm, "end": v(-28.96, -63.29) * mm});
            skLineSegment(sketch, "E6.7.12.3", {"start": v(-28.96, -63.29) * mm, "end": v(-28.96, -58.67) * mm});
            skLineSegment(sketch, "E6.8.0.0", {"start": v(-11.63, 93.73) * mm, "end": v(-16.26, 93.73) * mm});
            skLineSegment(sketch, "E6.8.0.1", {"start": v(-11.63, 89.11) * mm, "end": v(-11.63, 93.73) * mm});
            skLineSegment(sketch, "E6.8.0.2", {"start": v(-11.63, 89.11) * mm, "end": v(-16.26, 89.11) * mm});
            skLineSegment(sketch, "E6.8.0.3", {"start": v(-16.26, 89.11) * mm, "end": v(-16.26, 93.73) * mm});
            skLineSegment(sketch, "E6.8.1.0", {"start": v(-11.63, 81.03) * mm, "end": v(-16.26, 81.03) * mm});
            skLineSegment(sketch, "E6.8.1.1", {"start": v(-11.63, 76.41) * mm, "end": v(-11.63, 81.03) * mm});
            skLineSegment(sketch, "E6.8.1.2", {"start": v(-11.63, 76.41) * mm, "end": v(-16.26, 76.41) * mm});
            skLineSegment(sketch, "E6.8.1.3", {"start": v(-16.26, 76.41) * mm, "end": v(-16.26, 81.03) * mm});
            skLineSegment(sketch, "E6.8.2.0", {"start": v(-11.63, 68.33) * mm, "end": v(-16.26, 68.33) * mm});
            skLineSegment(sketch, "E6.8.2.1", {"start": v(-11.63, 63.71) * mm, "end": v(-11.63, 68.33) * mm});
            skLineSegment(sketch, "E6.8.2.2", {"start": v(-11.63, 63.71) * mm, "end": v(-16.26, 63.71) * mm});
            skLineSegment(sketch, "E6.8.2.3", {"start": v(-16.26, 63.71) * mm, "end": v(-16.26, 68.33) * mm});
            skLineSegment(sketch, "E6.8.3.0", {"start": v(-11.63, 55.63) * mm, "end": v(-16.26, 55.63) * mm});
            skLineSegment(sketch, "E6.8.3.1", {"start": v(-11.63, 51.01) * mm, "end": v(-11.63, 55.63) * mm});
            skLineSegment(sketch, "E6.8.3.2", {"start": v(-11.63, 51.01) * mm, "end": v(-16.26, 51.01) * mm});
            skLineSegment(sketch, "E6.8.3.3", {"start": v(-16.26, 51.01) * mm, "end": v(-16.26, 55.63) * mm});
            skLineSegment(sketch, "E6.8.4.0", {"start": v(-11.63, 42.93) * mm, "end": v(-16.26, 42.93) * mm});
            skLineSegment(sketch, "E6.8.4.1", {"start": v(-11.63, 38.31) * mm, "end": v(-11.63, 42.93) * mm});
            skLineSegment(sketch, "E6.8.4.2", {"start": v(-11.63, 38.31) * mm, "end": v(-16.26, 38.31) * mm});
            skLineSegment(sketch, "E6.8.4.3", {"start": v(-16.26, 38.31) * mm, "end": v(-16.26, 42.93) * mm});
            skLineSegment(sketch, "E6.8.5.0", {"start": v(-11.63, 30.23) * mm, "end": v(-16.26, 30.23) * mm});
            skLineSegment(sketch, "E6.8.5.1", {"start": v(-11.63, 25.61) * mm, "end": v(-11.63, 30.23) * mm});
            skLineSegment(sketch, "E6.8.5.2", {"start": v(-11.63, 25.61) * mm, "end": v(-16.26, 25.61) * mm});
            skLineSegment(sketch, "E6.8.5.3", {"start": v(-16.26, 25.61) * mm, "end": v(-16.26, 30.23) * mm});
            skLineSegment(sketch, "E6.8.6.0", {"start": v(-11.63, 17.53) * mm, "end": v(-16.26, 17.53) * mm});
            skLineSegment(sketch, "E6.8.6.1", {"start": v(-11.63, 12.91) * mm, "end": v(-11.63, 17.53) * mm});
            skLineSegment(sketch, "E6.8.6.2", {"start": v(-11.63, 12.91) * mm, "end": v(-16.26, 12.91) * mm});
            skLineSegment(sketch, "E6.8.6.3", {"start": v(-16.26, 12.91) * mm, "end": v(-16.26, 17.53) * mm});
            skLineSegment(sketch, "E6.8.7.0", {"start": v(-11.63, 4.83) * mm, "end": v(-16.26, 4.83) * mm});
            skLineSegment(sketch, "E6.8.7.1", {"start": v(-11.63, 0.21) * mm, "end": v(-11.63, 4.83) * mm});
            skLineSegment(sketch, "E6.8.7.2", {"start": v(-11.63, 0.21) * mm, "end": v(-16.26, 0.21) * mm});
            skLineSegment(sketch, "E6.8.7.3", {"start": v(-16.26, 0.21) * mm, "end": v(-16.26, 4.83) * mm});
            skLineSegment(sketch, "E6.8.8.0", {"start": v(-11.63, -7.87) * mm, "end": v(-16.26, -7.87) * mm});
            skLineSegment(sketch, "E6.8.8.1", {"start": v(-11.63, -12.49) * mm, "end": v(-11.63, -7.87) * mm});
            skLineSegment(sketch, "E6.8.8.2", {"start": v(-11.63, -12.49) * mm, "end": v(-16.26, -12.49) * mm});
            skLineSegment(sketch, "E6.8.8.3", {"start": v(-16.26, -12.49) * mm, "end": v(-16.26, -7.87) * mm});
            skLineSegment(sketch, "E6.8.9.0", {"start": v(-11.63, -20.57) * mm, "end": v(-16.26, -20.57) * mm});
            skLineSegment(sketch, "E6.8.9.1", {"start": v(-11.63, -25.19) * mm, "end": v(-11.63, -20.57) * mm});
            skLineSegment(sketch, "E6.8.9.2", {"start": v(-11.63, -25.19) * mm, "end": v(-16.26, -25.19) * mm});
            skLineSegment(sketch, "E6.8.9.3", {"start": v(-16.26, -25.19) * mm, "end": v(-16.26, -20.57) * mm});
            skLineSegment(sketch, "E6.8.10.0", {"start": v(-11.63, -33.27) * mm, "end": v(-16.26, -33.27) * mm});
            skLineSegment(sketch, "E6.8.10.1", {"start": v(-11.63, -37.89) * mm, "end": v(-11.63, -33.27) * mm});
            skLineSegment(sketch, "E6.8.10.2", {"start": v(-11.63, -37.89) * mm, "end": v(-16.26, -37.89) * mm});
            skLineSegment(sketch, "E6.8.10.3", {"start": v(-16.26, -37.89) * mm, "end": v(-16.26, -33.27) * mm});
            skLineSegment(sketch, "E6.8.11.0", {"start": v(-11.63, -45.97) * mm, "end": v(-16.26, -45.97) * mm});
            skLineSegment(sketch, "E6.8.11.1", {"start": v(-11.63, -50.59) * mm, "end": v(-11.63, -45.97) * mm});
            skLineSegment(sketch, "E6.8.11.2", {"start": v(-11.63, -50.59) * mm, "end": v(-16.26, -50.59) * mm});
            skLineSegment(sketch, "E6.8.11.3", {"start": v(-16.26, -50.59) * mm, "end": v(-16.26, -45.97) * mm});
            skLineSegment(sketch, "E6.8.12.0", {"start": v(-11.63, -58.67) * mm, "end": v(-16.26, -58.67) * mm});
            skLineSegment(sketch, "E6.8.12.1", {"start": v(-11.63, -63.29) * mm, "end": v(-11.63, -58.67) * mm});
            skLineSegment(sketch, "E6.8.12.2", {"start": v(-11.63, -63.29) * mm, "end": v(-16.26, -63.29) * mm});
            skLineSegment(sketch, "E6.8.12.3", {"start": v(-16.26, -63.29) * mm, "end": v(-16.26, -58.67) * mm});
            skLineSegment(sketch, "E6.9.0.0", {"start": v(1.07, 93.73) * mm, "end": v(-3.56, 93.73) * mm});
            skLineSegment(sketch, "E6.9.0.1", {"start": v(1.07, 89.11) * mm, "end": v(1.07, 93.73) * mm});
            skLineSegment(sketch, "E6.9.0.2", {"start": v(1.07, 89.11) * mm, "end": v(-3.56, 89.11) * mm});
            skLineSegment(sketch, "E6.9.0.3", {"start": v(-3.56, 89.11) * mm, "end": v(-3.56, 93.73) * mm});
            skLineSegment(sketch, "E6.9.1.0", {"start": v(1.07, 81.03) * mm, "end": v(-3.56, 81.03) * mm});
            skLineSegment(sketch, "E6.9.1.1", {"start": v(1.07, 76.41) * mm, "end": v(1.07, 81.03) * mm});
            skLineSegment(sketch, "E6.9.1.2", {"start": v(1.07, 76.41) * mm, "end": v(-3.56, 76.41) * mm});
            skLineSegment(sketch, "E6.9.1.3", {"start": v(-3.56, 76.41) * mm, "end": v(-3.56, 81.03) * mm});
            skLineSegment(sketch, "E6.9.2.0", {"start": v(1.07, 68.33) * mm, "end": v(-3.56, 68.33) * mm});
            skLineSegment(sketch, "E6.9.2.1", {"start": v(1.07, 63.71) * mm, "end": v(1.07, 68.33) * mm});
            skLineSegment(sketch, "E6.9.2.2", {"start": v(1.07, 63.71) * mm, "end": v(-3.56, 63.71) * mm});
            skLineSegment(sketch, "E6.9.2.3", {"start": v(-3.56, 63.71) * mm, "end": v(-3.56, 68.33) * mm});
            skLineSegment(sketch, "E6.9.3.0", {"start": v(1.07, 55.63) * mm, "end": v(-3.56, 55.63) * mm});
            skLineSegment(sketch, "E6.9.3.1", {"start": v(1.07, 51.01) * mm, "end": v(1.07, 55.63) * mm});
            skLineSegment(sketch, "E6.9.3.2", {"start": v(1.07, 51.01) * mm, "end": v(-3.56, 51.01) * mm});
            skLineSegment(sketch, "E6.9.3.3", {"start": v(-3.56, 51.01) * mm, "end": v(-3.56, 55.63) * mm});
            skLineSegment(sketch, "E6.9.4.0", {"start": v(1.07, 42.93) * mm, "end": v(-3.56, 42.93) * mm});
            skLineSegment(sketch, "E6.9.4.1", {"start": v(1.07, 38.31) * mm, "end": v(1.07, 42.93) * mm});
            skLineSegment(sketch, "E6.9.4.2", {"start": v(1.07, 38.31) * mm, "end": v(-3.56, 38.31) * mm});
            skLineSegment(sketch, "E6.9.4.3", {"start": v(-3.56, 38.31) * mm, "end": v(-3.56, 42.93) * mm});
            skLineSegment(sketch, "E6.9.5.0", {"start": v(1.07, 30.23) * mm, "end": v(-3.56, 30.23) * mm});
            skLineSegment(sketch, "E6.9.5.1", {"start": v(1.07, 25.61) * mm, "end": v(1.07, 30.23) * mm});
            skLineSegment(sketch, "E6.9.5.2", {"start": v(1.07, 25.61) * mm, "end": v(-3.56, 25.61) * mm});
            skLineSegment(sketch, "E6.9.5.3", {"start": v(-3.56, 25.61) * mm, "end": v(-3.56, 30.23) * mm});
            skLineSegment(sketch, "E6.9.6.0", {"start": v(1.07, 17.53) * mm, "end": v(-3.56, 17.53) * mm});
            skLineSegment(sketch, "E6.9.6.1", {"start": v(1.07, 12.91) * mm, "end": v(1.07, 17.53) * mm});
            skLineSegment(sketch, "E6.9.6.2", {"start": v(1.07, 12.91) * mm, "end": v(-3.56, 12.91) * mm});
            skLineSegment(sketch, "E6.9.6.3", {"start": v(-3.56, 12.91) * mm, "end": v(-3.56, 17.53) * mm});
            skLineSegment(sketch, "E6.9.7.0", {"start": v(1.07, 4.83) * mm, "end": v(-3.56, 4.83) * mm});
            skLineSegment(sketch, "E6.9.7.1", {"start": v(1.07, 0.21) * mm, "end": v(1.07, 4.83) * mm});
            skLineSegment(sketch, "E6.9.7.2", {"start": v(1.07, 0.21) * mm, "end": v(-3.56, 0.21) * mm});
            skLineSegment(sketch, "E6.9.7.3", {"start": v(-3.56, 0.21) * mm, "end": v(-3.56, 4.83) * mm});
            skLineSegment(sketch, "E6.9.8.0", {"start": v(1.07, -7.87) * mm, "end": v(-3.56, -7.87) * mm});
            skLineSegment(sketch, "E6.9.8.1", {"start": v(1.07, -12.49) * mm, "end": v(1.07, -7.87) * mm});
            skLineSegment(sketch, "E6.9.8.2", {"start": v(1.07, -12.49) * mm, "end": v(-3.56, -12.49) * mm});
            skLineSegment(sketch, "E6.9.8.3", {"start": v(-3.56, -12.49) * mm, "end": v(-3.56, -7.87) * mm});
            skLineSegment(sketch, "E6.9.9.0", {"start": v(1.07, -20.57) * mm, "end": v(-3.56, -20.57) * mm});
            skLineSegment(sketch, "E6.9.9.1", {"start": v(1.07, -25.19) * mm, "end": v(1.07, -20.57) * mm});
            skLineSegment(sketch, "E6.9.9.2", {"start": v(1.07, -25.19) * mm, "end": v(-3.56, -25.19) * mm});
            skLineSegment(sketch, "E6.9.9.3", {"start": v(-3.56, -25.19) * mm, "end": v(-3.56, -20.57) * mm});
            skLineSegment(sketch, "E6.9.10.0", {"start": v(1.07, -33.27) * mm, "end": v(-3.56, -33.27) * mm});
            skLineSegment(sketch, "E6.9.10.1", {"start": v(1.07, -37.89) * mm, "end": v(1.07, -33.27) * mm});
            skLineSegment(sketch, "E6.9.10.2", {"start": v(1.07, -37.89) * mm, "end": v(-3.56, -37.89) * mm});
            skLineSegment(sketch, "E6.9.10.3", {"start": v(-3.56, -37.89) * mm, "end": v(-3.56, -33.27) * mm});
            skLineSegment(sketch, "E6.9.11.0", {"start": v(1.07, -45.97) * mm, "end": v(-3.56, -45.97) * mm});
            skLineSegment(sketch, "E6.9.11.1", {"start": v(1.07, -50.59) * mm, "end": v(1.07, -45.97) * mm});
            skLineSegment(sketch, "E6.9.11.2", {"start": v(1.07, -50.59) * mm, "end": v(-3.56, -50.59) * mm});
            skLineSegment(sketch, "E6.9.11.3", {"start": v(-3.56, -50.59) * mm, "end": v(-3.56, -45.97) * mm});
            skLineSegment(sketch, "E6.9.12.0", {"start": v(1.07, -58.67) * mm, "end": v(-3.56, -58.67) * mm});
            skLineSegment(sketch, "E6.9.12.1", {"start": v(1.07, -63.29) * mm, "end": v(1.07, -58.67) * mm});
            skLineSegment(sketch, "E6.9.12.2", {"start": v(1.07, -63.29) * mm, "end": v(-3.56, -63.29) * mm});
            skLineSegment(sketch, "E6.9.12.3", {"start": v(-3.56, -63.29) * mm, "end": v(-3.56, -58.67) * mm});
            skLineSegment(sketch, "E6.10.0.0", {"start": v(13.77, 93.73) * mm, "end": v(9.14, 93.73) * mm});
            skLineSegment(sketch, "E6.10.0.1", {"start": v(13.77, 89.11) * mm, "end": v(13.77, 93.73) * mm});
            skLineSegment(sketch, "E6.10.0.2", {"start": v(13.77, 89.11) * mm, "end": v(9.14, 89.11) * mm});
            skLineSegment(sketch, "E6.10.0.3", {"start": v(9.14, 89.11) * mm, "end": v(9.14, 93.73) * mm});
            skLineSegment(sketch, "E6.10.1.0", {"start": v(13.77, 81.03) * mm, "end": v(9.14, 81.03) * mm});
            skLineSegment(sketch, "E6.10.1.1", {"start": v(13.77, 76.41) * mm, "end": v(13.77, 81.03) * mm});
            skLineSegment(sketch, "E6.10.1.2", {"start": v(13.77, 76.41) * mm, "end": v(9.14, 76.41) * mm});
            skLineSegment(sketch, "E6.10.1.3", {"start": v(9.14, 76.41) * mm, "end": v(9.14, 81.03) * mm});
            skLineSegment(sketch, "E6.10.2.0", {"start": v(13.77, 68.33) * mm, "end": v(9.14, 68.33) * mm});
            skLineSegment(sketch, "E6.10.2.1", {"start": v(13.77, 63.71) * mm, "end": v(13.77, 68.33) * mm});
            skLineSegment(sketch, "E6.10.2.2", {"start": v(13.77, 63.71) * mm, "end": v(9.14, 63.71) * mm});
            skLineSegment(sketch, "E6.10.2.3", {"start": v(9.14, 63.71) * mm, "end": v(9.14, 68.33) * mm});
            skLineSegment(sketch, "E6.10.3.0", {"start": v(13.77, 55.63) * mm, "end": v(9.14, 55.63) * mm});
            skLineSegment(sketch, "E6.10.3.1", {"start": v(13.77, 51.01) * mm, "end": v(13.77, 55.63) * mm});
            skLineSegment(sketch, "E6.10.3.2", {"start": v(13.77, 51.01) * mm, "end": v(9.14, 51.01) * mm});
            skLineSegment(sketch, "E6.10.3.3", {"start": v(9.14, 51.01) * mm, "end": v(9.14, 55.63) * mm});
            skLineSegment(sketch, "E6.10.4.0", {"start": v(13.77, 42.93) * mm, "end": v(9.14, 42.93) * mm});
            skLineSegment(sketch, "E6.10.4.1", {"start": v(13.77, 38.31) * mm, "end": v(13.77, 42.93) * mm});
            skLineSegment(sketch, "E6.10.4.2", {"start": v(13.77, 38.31) * mm, "end": v(9.14, 38.31) * mm});
            skLineSegment(sketch, "E6.10.4.3", {"start": v(9.14, 38.31) * mm, "end": v(9.14, 42.93) * mm});
            skLineSegment(sketch, "E6.10.5.0", {"start": v(13.77, 30.23) * mm, "end": v(9.14, 30.23) * mm});
            skLineSegment(sketch, "E6.10.5.1", {"start": v(13.77, 25.61) * mm, "end": v(13.77, 30.23) * mm});
            skLineSegment(sketch, "E6.10.5.2", {"start": v(13.77, 25.61) * mm, "end": v(9.14, 25.61) * mm});
            skLineSegment(sketch, "E6.10.5.3", {"start": v(9.14, 25.61) * mm, "end": v(9.14, 30.23) * mm});
            skLineSegment(sketch, "E6.10.6.0", {"start": v(13.77, 17.53) * mm, "end": v(9.14, 17.53) * mm});
            skLineSegment(sketch, "E6.10.6.1", {"start": v(13.77, 12.91) * mm, "end": v(13.77, 17.53) * mm});
            skLineSegment(sketch, "E6.10.6.2", {"start": v(13.77, 12.91) * mm, "end": v(9.14, 12.91) * mm});
            skLineSegment(sketch, "E6.10.6.3", {"start": v(9.14, 12.91) * mm, "end": v(9.14, 17.53) * mm});
            skLineSegment(sketch, "E6.10.7.0", {"start": v(13.77, 4.83) * mm, "end": v(9.14, 4.83) * mm});
            skLineSegment(sketch, "E6.10.7.1", {"start": v(13.77, 0.21) * mm, "end": v(13.77, 4.83) * mm});
            skLineSegment(sketch, "E6.10.7.2", {"start": v(13.77, 0.21) * mm, "end": v(9.14, 0.21) * mm});
            skLineSegment(sketch, "E6.10.7.3", {"start": v(9.14, 0.21) * mm, "end": v(9.14, 4.83) * mm});
            skLineSegment(sketch, "E6.10.8.0", {"start": v(13.77, -7.87) * mm, "end": v(9.14, -7.87) * mm});
            skLineSegment(sketch, "E6.10.8.1", {"start": v(13.77, -12.49) * mm, "end": v(13.77, -7.87) * mm});
            skLineSegment(sketch, "E6.10.8.2", {"start": v(13.77, -12.49) * mm, "end": v(9.14, -12.49) * mm});
            skLineSegment(sketch, "E6.10.8.3", {"start": v(9.14, -12.49) * mm, "end": v(9.14, -7.87) * mm});
            skLineSegment(sketch, "E6.10.9.0", {"start": v(13.77, -20.57) * mm, "end": v(9.14, -20.57) * mm});
            skLineSegment(sketch, "E6.10.9.1", {"start": v(13.77, -25.19) * mm, "end": v(13.77, -20.57) * mm});
            skLineSegment(sketch, "E6.10.9.2", {"start": v(13.77, -25.19) * mm, "end": v(9.14, -25.19) * mm});
            skLineSegment(sketch, "E6.10.9.3", {"start": v(9.14, -25.19) * mm, "end": v(9.14, -20.57) * mm});
            skLineSegment(sketch, "E6.10.10.0", {"start": v(13.77, -33.27) * mm, "end": v(9.14, -33.27) * mm});
            skLineSegment(sketch, "E6.10.10.1", {"start": v(13.77, -37.89) * mm, "end": v(13.77, -33.27) * mm});
            skLineSegment(sketch, "E6.10.10.2", {"start": v(13.77, -37.89) * mm, "end": v(9.14, -37.89) * mm});
            skLineSegment(sketch, "E6.10.10.3", {"start": v(9.14, -37.89) * mm, "end": v(9.14, -33.27) * mm});
            skLineSegment(sketch, "E6.10.11.0", {"start": v(13.77, -45.97) * mm, "end": v(9.14, -45.97) * mm});
            skLineSegment(sketch, "E6.10.11.1", {"start": v(13.77, -50.59) * mm, "end": v(13.77, -45.97) * mm});
            skLineSegment(sketch, "E6.10.11.2", {"start": v(13.77, -50.59) * mm, "end": v(9.14, -50.59) * mm});
            skLineSegment(sketch, "E6.10.11.3", {"start": v(9.14, -50.59) * mm, "end": v(9.14, -45.97) * mm});
            skLineSegment(sketch, "E6.10.12.0", {"start": v(13.77, -58.67) * mm, "end": v(9.14, -58.67) * mm});
            skLineSegment(sketch, "E6.10.12.1", {"start": v(13.77, -63.29) * mm, "end": v(13.77, -58.67) * mm});
            skLineSegment(sketch, "E6.10.12.2", {"start": v(13.77, -63.29) * mm, "end": v(9.14, -63.29) * mm});
            skLineSegment(sketch, "E6.10.12.3", {"start": v(9.14, -63.29) * mm, "end": v(9.14, -58.67) * mm});
            skLineSegment(sketch, "E6.11.0.0", {"start": v(26.47, 93.73) * mm, "end": v(21.84, 93.73) * mm});
            skLineSegment(sketch, "E6.11.0.1", {"start": v(26.47, 89.11) * mm, "end": v(26.47, 93.73) * mm});
            skLineSegment(sketch, "E6.11.0.2", {"start": v(26.47, 89.11) * mm, "end": v(21.84, 89.11) * mm});
            skLineSegment(sketch, "E6.11.0.3", {"start": v(21.84, 89.11) * mm, "end": v(21.84, 93.73) * mm});
            skLineSegment(sketch, "E6.11.1.0", {"start": v(26.47, 81.03) * mm, "end": v(21.84, 81.03) * mm});
            skLineSegment(sketch, "E6.11.1.1", {"start": v(26.47, 76.41) * mm, "end": v(26.47, 81.03) * mm});
            skLineSegment(sketch, "E6.11.1.2", {"start": v(26.47, 76.41) * mm, "end": v(21.84, 76.41) * mm});
            skLineSegment(sketch, "E6.11.1.3", {"start": v(21.84, 76.41) * mm, "end": v(21.84, 81.03) * mm});
            skLineSegment(sketch, "E6.11.2.0", {"start": v(26.47, 68.33) * mm, "end": v(21.84, 68.33) * mm});
            skLineSegment(sketch, "E6.11.2.1", {"start": v(26.47, 63.71) * mm, "end": v(26.47, 68.33) * mm});
            skLineSegment(sketch, "E6.11.2.2", {"start": v(26.47, 63.71) * mm, "end": v(21.84, 63.71) * mm});
            skLineSegment(sketch, "E6.11.2.3", {"start": v(21.84, 63.71) * mm, "end": v(21.84, 68.33) * mm});
            skLineSegment(sketch, "E6.11.3.0", {"start": v(26.47, 55.63) * mm, "end": v(21.84, 55.63) * mm});
            skLineSegment(sketch, "E6.11.3.1", {"start": v(26.47, 51.01) * mm, "end": v(26.47, 55.63) * mm});
            skLineSegment(sketch, "E6.11.3.2", {"start": v(26.47, 51.01) * mm, "end": v(21.84, 51.01) * mm});
            skLineSegment(sketch, "E6.11.3.3", {"start": v(21.84, 51.01) * mm, "end": v(21.84, 55.63) * mm});
            skLineSegment(sketch, "E6.11.4.0", {"start": v(26.47, 42.93) * mm, "end": v(21.84, 42.93) * mm});
            skLineSegment(sketch, "E6.11.4.1", {"start": v(26.47, 38.31) * mm, "end": v(26.47, 42.93) * mm});
            skLineSegment(sketch, "E6.11.4.2", {"start": v(26.47, 38.31) * mm, "end": v(21.84, 38.31) * mm});
            skLineSegment(sketch, "E6.11.4.3", {"start": v(21.84, 38.31) * mm, "end": v(21.84, 42.93) * mm});
            skLineSegment(sketch, "E6.11.5.0", {"start": v(26.47, 30.23) * mm, "end": v(21.84, 30.23) * mm});
            skLineSegment(sketch, "E6.11.5.1", {"start": v(26.47, 25.61) * mm, "end": v(26.47, 30.23) * mm});
            skLineSegment(sketch, "E6.11.5.2", {"start": v(26.47, 25.61) * mm, "end": v(21.84, 25.61) * mm});
            skLineSegment(sketch, "E6.11.5.3", {"start": v(21.84, 25.61) * mm, "end": v(21.84, 30.23) * mm});
            skLineSegment(sketch, "E6.11.6.0", {"start": v(26.47, 17.53) * mm, "end": v(21.84, 17.53) * mm});
            skLineSegment(sketch, "E6.11.6.1", {"start": v(26.47, 12.91) * mm, "end": v(26.47, 17.53) * mm});
            skLineSegment(sketch, "E6.11.6.2", {"start": v(26.47, 12.91) * mm, "end": v(21.84, 12.91) * mm});
            skLineSegment(sketch, "E6.11.6.3", {"start": v(21.84, 12.91) * mm, "end": v(21.84, 17.53) * mm});
            skLineSegment(sketch, "E6.11.7.0", {"start": v(26.47, 4.83) * mm, "end": v(21.84, 4.83) * mm});
            skLineSegment(sketch, "E6.11.7.1", {"start": v(26.47, 0.21) * mm, "end": v(26.47, 4.83) * mm});
            skLineSegment(sketch, "E6.11.7.2", {"start": v(26.47, 0.21) * mm, "end": v(21.84, 0.21) * mm});
            skLineSegment(sketch, "E6.11.7.3", {"start": v(21.84, 0.21) * mm, "end": v(21.84, 4.83) * mm});
            skLineSegment(sketch, "E6.11.8.0", {"start": v(26.47, -7.87) * mm, "end": v(21.84, -7.87) * mm});
            skLineSegment(sketch, "E6.11.8.1", {"start": v(26.47, -12.49) * mm, "end": v(26.47, -7.87) * mm});
            skLineSegment(sketch, "E6.11.8.2", {"start": v(26.47, -12.49) * mm, "end": v(21.84, -12.49) * mm});
            skLineSegment(sketch, "E6.11.8.3", {"start": v(21.84, -12.49) * mm, "end": v(21.84, -7.87) * mm});
            skLineSegment(sketch, "E6.11.9.0", {"start": v(26.47, -20.57) * mm, "end": v(21.84, -20.57) * mm});
            skLineSegment(sketch, "E6.11.9.1", {"start": v(26.47, -25.19) * mm, "end": v(26.47, -20.57) * mm});
            skLineSegment(sketch, "E6.11.9.2", {"start": v(26.47, -25.19) * mm, "end": v(21.84, -25.19) * mm});
            skLineSegment(sketch, "E6.11.9.3", {"start": v(21.84, -25.19) * mm, "end": v(21.84, -20.57) * mm});
            skLineSegment(sketch, "E6.11.10.0", {"start": v(26.47, -33.27) * mm, "end": v(21.84, -33.27) * mm});
            skLineSegment(sketch, "E6.11.10.1", {"start": v(26.47, -37.89) * mm, "end": v(26.47, -33.27) * mm});
            skLineSegment(sketch, "E6.11.10.2", {"start": v(26.47, -37.89) * mm, "end": v(21.84, -37.89) * mm});
            skLineSegment(sketch, "E6.11.10.3", {"start": v(21.84, -37.89) * mm, "end": v(21.84, -33.27) * mm});
            skLineSegment(sketch, "E6.11.11.0", {"start": v(26.47, -45.97) * mm, "end": v(21.84, -45.97) * mm});
            skLineSegment(sketch, "E6.11.11.1", {"start": v(26.47, -50.59) * mm, "end": v(26.47, -45.97) * mm});
            skLineSegment(sketch, "E6.11.11.2", {"start": v(26.47, -50.59) * mm, "end": v(21.84, -50.59) * mm});
            skLineSegment(sketch, "E6.11.11.3", {"start": v(21.84, -50.59) * mm, "end": v(21.84, -45.97) * mm});
            skLineSegment(sketch, "E6.11.12.0", {"start": v(26.47, -58.67) * mm, "end": v(21.84, -58.67) * mm});
            skLineSegment(sketch, "E6.11.12.1", {"start": v(26.47, -63.29) * mm, "end": v(26.47, -58.67) * mm});
            skLineSegment(sketch, "E6.11.12.2", {"start": v(26.47, -63.29) * mm, "end": v(21.84, -63.29) * mm});
            skLineSegment(sketch, "E6.11.12.3", {"start": v(21.84, -63.29) * mm, "end": v(21.84, -58.67) * mm});
            skLineSegment(sketch, "E6.12.0.0", {"start": v(39.17, 93.73) * mm, "end": v(34.54, 93.73) * mm});
            skLineSegment(sketch, "E6.12.0.1", {"start": v(39.17, 89.11) * mm, "end": v(39.17, 93.73) * mm});
            skLineSegment(sketch, "E6.12.0.2", {"start": v(39.17, 89.11) * mm, "end": v(34.54, 89.11) * mm});
            skLineSegment(sketch, "E6.12.0.3", {"start": v(34.54, 89.11) * mm, "end": v(34.54, 93.73) * mm});
            skLineSegment(sketch, "E6.12.1.0", {"start": v(39.17, 81.03) * mm, "end": v(34.54, 81.03) * mm});
            skLineSegment(sketch, "E6.12.1.1", {"start": v(39.17, 76.41) * mm, "end": v(39.17, 81.03) * mm});
            skLineSegment(sketch, "E6.12.1.2", {"start": v(39.17, 76.41) * mm, "end": v(34.54, 76.41) * mm});
            skLineSegment(sketch, "E6.12.1.3", {"start": v(34.54, 76.41) * mm, "end": v(34.54, 81.03) * mm});
            skLineSegment(sketch, "E6.12.2.0", {"start": v(39.17, 68.33) * mm, "end": v(34.54, 68.33) * mm});
            skLineSegment(sketch, "E6.12.2.1", {"start": v(39.17, 63.71) * mm, "end": v(39.17, 68.33) * mm});
            skLineSegment(sketch, "E6.12.2.2", {"start": v(39.17, 63.71) * mm, "end": v(34.54, 63.71) * mm});
            skLineSegment(sketch, "E6.12.2.3", {"start": v(34.54, 63.71) * mm, "end": v(34.54, 68.33) * mm});
            skLineSegment(sketch, "E6.12.3.0", {"start": v(39.17, 55.63) * mm, "end": v(34.54, 55.63) * mm});
            skLineSegment(sketch, "E6.12.3.1", {"start": v(39.17, 51.01) * mm, "end": v(39.17, 55.63) * mm});
            skLineSegment(sketch, "E6.12.3.2", {"start": v(39.17, 51.01) * mm, "end": v(34.54, 51.01) * mm});
            skLineSegment(sketch, "E6.12.3.3", {"start": v(34.54, 51.01) * mm, "end": v(34.54, 55.63) * mm});
            skLineSegment(sketch, "E6.12.4.0", {"start": v(39.17, 42.93) * mm, "end": v(34.54, 42.93) * mm});
            skLineSegment(sketch, "E6.12.4.1", {"start": v(39.17, 38.31) * mm, "end": v(39.17, 42.93) * mm});
            skLineSegment(sketch, "E6.12.4.2", {"start": v(39.17, 38.31) * mm, "end": v(34.54, 38.31) * mm});
            skLineSegment(sketch, "E6.12.4.3", {"start": v(34.54, 38.31) * mm, "end": v(34.54, 42.93) * mm});
            skLineSegment(sketch, "E6.12.5.0", {"start": v(39.17, 30.23) * mm, "end": v(34.54, 30.23) * mm});
            skLineSegment(sketch, "E6.12.5.1", {"start": v(39.17, 25.61) * mm, "end": v(39.17, 30.23) * mm});
            skLineSegment(sketch, "E6.12.5.2", {"start": v(39.17, 25.61) * mm, "end": v(34.54, 25.61) * mm});
            skLineSegment(sketch, "E6.12.5.3", {"start": v(34.54, 25.61) * mm, "end": v(34.54, 30.23) * mm});
            skLineSegment(sketch, "E6.12.6.0", {"start": v(39.17, 17.53) * mm, "end": v(34.54, 17.53) * mm});
            skLineSegment(sketch, "E6.12.6.1", {"start": v(39.17, 12.91) * mm, "end": v(39.17, 17.53) * mm});
            skLineSegment(sketch, "E6.12.6.2", {"start": v(39.17, 12.91) * mm, "end": v(34.54, 12.91) * mm});
            skLineSegment(sketch, "E6.12.6.3", {"start": v(34.54, 12.91) * mm, "end": v(34.54, 17.53) * mm});
            skLineSegment(sketch, "E6.12.7.0", {"start": v(39.17, 4.83) * mm, "end": v(34.54, 4.83) * mm});
            skLineSegment(sketch, "E6.12.7.1", {"start": v(39.17, 0.21) * mm, "end": v(39.17, 4.83) * mm});
            skLineSegment(sketch, "E6.12.7.2", {"start": v(39.17, 0.21) * mm, "end": v(34.54, 0.21) * mm});
            skLineSegment(sketch, "E6.12.7.3", {"start": v(34.54, 0.21) * mm, "end": v(34.54, 4.83) * mm});
            skLineSegment(sketch, "E6.12.8.0", {"start": v(39.17, -7.87) * mm, "end": v(34.54, -7.87) * mm});
            skLineSegment(sketch, "E6.12.8.1", {"start": v(39.17, -12.49) * mm, "end": v(39.17, -7.87) * mm});
            skLineSegment(sketch, "E6.12.8.2", {"start": v(39.17, -12.49) * mm, "end": v(34.54, -12.49) * mm});
            skLineSegment(sketch, "E6.12.8.3", {"start": v(34.54, -12.49) * mm, "end": v(34.54, -7.87) * mm});
            skLineSegment(sketch, "E6.12.9.0", {"start": v(39.17, -20.57) * mm, "end": v(34.54, -20.57) * mm});
            skLineSegment(sketch, "E6.12.9.1", {"start": v(39.17, -25.19) * mm, "end": v(39.17, -20.57) * mm});
            skLineSegment(sketch, "E6.12.9.2", {"start": v(39.17, -25.19) * mm, "end": v(34.54, -25.19) * mm});
            skLineSegment(sketch, "E6.12.9.3", {"start": v(34.54, -25.19) * mm, "end": v(34.54, -20.57) * mm});
            skLineSegment(sketch, "E6.12.10.0", {"start": v(39.17, -33.27) * mm, "end": v(34.54, -33.27) * mm});
            skLineSegment(sketch, "E6.12.10.1", {"start": v(39.17, -37.89) * mm, "end": v(39.17, -33.27) * mm});
            skLineSegment(sketch, "E6.12.10.2", {"start": v(39.17, -37.89) * mm, "end": v(34.54, -37.89) * mm});
            skLineSegment(sketch, "E6.12.10.3", {"start": v(34.54, -37.89) * mm, "end": v(34.54, -33.27) * mm});
            skLineSegment(sketch, "E6.12.11.0", {"start": v(39.17, -45.97) * mm, "end": v(34.54, -45.97) * mm});
            skLineSegment(sketch, "E6.12.11.1", {"start": v(39.17, -50.59) * mm, "end": v(39.17, -45.97) * mm});
            skLineSegment(sketch, "E6.12.11.2", {"start": v(39.17, -50.59) * mm, "end": v(34.54, -50.59) * mm});
            skLineSegment(sketch, "E6.12.11.3", {"start": v(34.54, -50.59) * mm, "end": v(34.54, -45.97) * mm});
            skLineSegment(sketch, "E6.12.12.0", {"start": v(39.17, -58.67) * mm, "end": v(34.54, -58.67) * mm});
            skLineSegment(sketch, "E6.12.12.1", {"start": v(39.17, -63.29) * mm, "end": v(39.17, -58.67) * mm});
            skLineSegment(sketch, "E6.12.12.2", {"start": v(39.17, -63.29) * mm, "end": v(34.54, -63.29) * mm});
            skLineSegment(sketch, "E6.12.12.3", {"start": v(34.54, -63.29) * mm, "end": v(34.54, -58.67) * mm});
            skLineSegment(sketch, "E6.13.0.0", {"start": v(51.87, 93.73) * mm, "end": v(47.24, 93.73) * mm});
            skLineSegment(sketch, "E6.13.0.1", {"start": v(51.87, 89.11) * mm, "end": v(51.87, 93.73) * mm});
            skLineSegment(sketch, "E6.13.0.2", {"start": v(51.87, 89.11) * mm, "end": v(47.24, 89.11) * mm});
            skLineSegment(sketch, "E6.13.0.3", {"start": v(47.24, 89.11) * mm, "end": v(47.24, 93.73) * mm});
            skLineSegment(sketch, "E6.13.1.0", {"start": v(51.87, 81.03) * mm, "end": v(47.24, 81.03) * mm});
            skLineSegment(sketch, "E6.13.1.1", {"start": v(51.87, 76.41) * mm, "end": v(51.87, 81.03) * mm});
            skLineSegment(sketch, "E6.13.1.2", {"start": v(51.87, 76.41) * mm, "end": v(47.24, 76.41) * mm});
            skLineSegment(sketch, "E6.13.1.3", {"start": v(47.24, 76.41) * mm, "end": v(47.24, 81.03) * mm});
            skLineSegment(sketch, "E6.13.2.0", {"start": v(51.87, 68.33) * mm, "end": v(47.24, 68.33) * mm});
            skLineSegment(sketch, "E6.13.2.1", {"start": v(51.87, 63.71) * mm, "end": v(51.87, 68.33) * mm});
            skLineSegment(sketch, "E6.13.2.2", {"start": v(51.87, 63.71) * mm, "end": v(47.24, 63.71) * mm});
            skLineSegment(sketch, "E6.13.2.3", {"start": v(47.24, 63.71) * mm, "end": v(47.24, 68.33) * mm});
            skLineSegment(sketch, "E6.13.3.0", {"start": v(51.87, 55.63) * mm, "end": v(47.24, 55.63) * mm});
            skLineSegment(sketch, "E6.13.3.1", {"start": v(51.87, 51.01) * mm, "end": v(51.87, 55.63) * mm});
            skLineSegment(sketch, "E6.13.3.2", {"start": v(51.87, 51.01) * mm, "end": v(47.24, 51.01) * mm});
            skLineSegment(sketch, "E6.13.3.3", {"start": v(47.24, 51.01) * mm, "end": v(47.24, 55.63) * mm});
            skLineSegment(sketch, "E6.13.4.0", {"start": v(51.87, 42.93) * mm, "end": v(47.24, 42.93) * mm});
            skLineSegment(sketch, "E6.13.4.1", {"start": v(51.87, 38.31) * mm, "end": v(51.87, 42.93) * mm});
            skLineSegment(sketch, "E6.13.4.2", {"start": v(51.87, 38.31) * mm, "end": v(47.24, 38.31) * mm});
            skLineSegment(sketch, "E6.13.4.3", {"start": v(47.24, 38.31) * mm, "end": v(47.24, 42.93) * mm});
            skLineSegment(sketch, "E6.13.5.0", {"start": v(51.87, 30.23) * mm, "end": v(47.24, 30.23) * mm});
            skLineSegment(sketch, "E6.13.5.1", {"start": v(51.87, 25.61) * mm, "end": v(51.87, 30.23) * mm});
            skLineSegment(sketch, "E6.13.5.2", {"start": v(51.87, 25.61) * mm, "end": v(47.24, 25.61) * mm});
            skLineSegment(sketch, "E6.13.5.3", {"start": v(47.24, 25.61) * mm, "end": v(47.24, 30.23) * mm});
            skLineSegment(sketch, "E6.13.6.0", {"start": v(51.87, 17.53) * mm, "end": v(47.24, 17.53) * mm});
            skLineSegment(sketch, "E6.13.6.1", {"start": v(51.87, 12.91) * mm, "end": v(51.87, 17.53) * mm});
            skLineSegment(sketch, "E6.13.6.2", {"start": v(51.87, 12.91) * mm, "end": v(47.24, 12.91) * mm});
            skLineSegment(sketch, "E6.13.6.3", {"start": v(47.24, 12.91) * mm, "end": v(47.24, 17.53) * mm});
            skLineSegment(sketch, "E6.13.7.0", {"start": v(51.87, 4.83) * mm, "end": v(47.24, 4.83) * mm});
            skLineSegment(sketch, "E6.13.7.1", {"start": v(51.87, 0.21) * mm, "end": v(51.87, 4.83) * mm});
            skLineSegment(sketch, "E6.13.7.2", {"start": v(51.87, 0.21) * mm, "end": v(47.24, 0.21) * mm});
            skLineSegment(sketch, "E6.13.7.3", {"start": v(47.24, 0.21) * mm, "end": v(47.24, 4.83) * mm});
            skLineSegment(sketch, "E6.13.8.0", {"start": v(51.87, -7.87) * mm, "end": v(47.24, -7.87) * mm});
            skLineSegment(sketch, "E6.13.8.1", {"start": v(51.87, -12.49) * mm, "end": v(51.87, -7.87) * mm});
            skLineSegment(sketch, "E6.13.8.2", {"start": v(51.87, -12.49) * mm, "end": v(47.24, -12.49) * mm});
            skLineSegment(sketch, "E6.13.8.3", {"start": v(47.24, -12.49) * mm, "end": v(47.24, -7.87) * mm});
            skLineSegment(sketch, "E6.13.9.0", {"start": v(51.87, -20.57) * mm, "end": v(47.24, -20.57) * mm});
            skLineSegment(sketch, "E6.13.9.1", {"start": v(51.87, -25.19) * mm, "end": v(51.87, -20.57) * mm});
            skLineSegment(sketch, "E6.13.9.2", {"start": v(51.87, -25.19) * mm, "end": v(47.24, -25.19) * mm});
            skLineSegment(sketch, "E6.13.9.3", {"start": v(47.24, -25.19) * mm, "end": v(47.24, -20.57) * mm});
            skLineSegment(sketch, "E6.13.10.0", {"start": v(51.87, -33.27) * mm, "end": v(47.24, -33.27) * mm});
            skLineSegment(sketch, "E6.13.10.1", {"start": v(51.87, -37.89) * mm, "end": v(51.87, -33.27) * mm});
            skLineSegment(sketch, "E6.13.10.2", {"start": v(51.87, -37.89) * mm, "end": v(47.24, -37.89) * mm});
            skLineSegment(sketch, "E6.13.10.3", {"start": v(47.24, -37.89) * mm, "end": v(47.24, -33.27) * mm});
            skLineSegment(sketch, "E6.13.11.0", {"start": v(51.87, -45.97) * mm, "end": v(47.24, -45.97) * mm});
            skLineSegment(sketch, "E6.13.11.1", {"start": v(51.87, -50.59) * mm, "end": v(51.87, -45.97) * mm});
            skLineSegment(sketch, "E6.13.11.2", {"start": v(51.87, -50.59) * mm, "end": v(47.24, -50.59) * mm});
            skLineSegment(sketch, "E6.13.11.3", {"start": v(47.24, -50.59) * mm, "end": v(47.24, -45.97) * mm});
            skLineSegment(sketch, "E6.13.12.0", {"start": v(51.87, -58.67) * mm, "end": v(47.24, -58.67) * mm});
            skLineSegment(sketch, "E6.13.12.1", {"start": v(51.87, -63.29) * mm, "end": v(51.87, -58.67) * mm});
            skLineSegment(sketch, "E6.13.12.2", {"start": v(51.87, -63.29) * mm, "end": v(47.24, -63.29) * mm});
            skLineSegment(sketch, "E6.13.12.3", {"start": v(47.24, -63.29) * mm, "end": v(47.24, -58.67) * mm});
            skLineSegment(sketch, "E6.14.0.0", {"start": v(64.57, 93.73) * mm, "end": v(59.94, 93.73) * mm});
            skLineSegment(sketch, "E6.14.0.1", {"start": v(64.57, 89.11) * mm, "end": v(64.57, 93.73) * mm});
            skLineSegment(sketch, "E6.14.0.2", {"start": v(64.57, 89.11) * mm, "end": v(59.94, 89.11) * mm});
            skLineSegment(sketch, "E6.14.0.3", {"start": v(59.94, 89.11) * mm, "end": v(59.94, 93.73) * mm});
            skLineSegment(sketch, "E6.14.1.0", {"start": v(64.57, 81.03) * mm, "end": v(59.94, 81.03) * mm});
            skLineSegment(sketch, "E6.14.1.1", {"start": v(64.57, 76.41) * mm, "end": v(64.57, 81.03) * mm});
            skLineSegment(sketch, "E6.14.1.2", {"start": v(64.57, 76.41) * mm, "end": v(59.94, 76.41) * mm});
            skLineSegment(sketch, "E6.14.1.3", {"start": v(59.94, 76.41) * mm, "end": v(59.94, 81.03) * mm});
            skLineSegment(sketch, "E6.14.2.0", {"start": v(64.57, 68.33) * mm, "end": v(59.94, 68.33) * mm});
            skLineSegment(sketch, "E6.14.2.1", {"start": v(64.57, 63.71) * mm, "end": v(64.57, 68.33) * mm});
            skLineSegment(sketch, "E6.14.2.2", {"start": v(64.57, 63.71) * mm, "end": v(59.94, 63.71) * mm});
            skLineSegment(sketch, "E6.14.2.3", {"start": v(59.94, 63.71) * mm, "end": v(59.94, 68.33) * mm});
            skLineSegment(sketch, "E6.14.3.0", {"start": v(64.57, 55.63) * mm, "end": v(59.94, 55.63) * mm});
            skLineSegment(sketch, "E6.14.3.1", {"start": v(64.57, 51.01) * mm, "end": v(64.57, 55.63) * mm});
            skLineSegment(sketch, "E6.14.3.2", {"start": v(64.57, 51.01) * mm, "end": v(59.94, 51.01) * mm});
            skLineSegment(sketch, "E6.14.3.3", {"start": v(59.94, 51.01) * mm, "end": v(59.94, 55.63) * mm});
            skLineSegment(sketch, "E6.14.4.0", {"start": v(64.57, 42.93) * mm, "end": v(59.94, 42.93) * mm});
            skLineSegment(sketch, "E6.14.4.1", {"start": v(64.57, 38.31) * mm, "end": v(64.57, 42.93) * mm});
            skLineSegment(sketch, "E6.14.4.2", {"start": v(64.57, 38.31) * mm, "end": v(59.94, 38.31) * mm});
            skLineSegment(sketch, "E6.14.4.3", {"start": v(59.94, 38.31) * mm, "end": v(59.94, 42.93) * mm});
            skLineSegment(sketch, "E6.14.5.0", {"start": v(64.57, 30.23) * mm, "end": v(59.94, 30.23) * mm});
            skLineSegment(sketch, "E6.14.5.1", {"start": v(64.57, 25.61) * mm, "end": v(64.57, 30.23) * mm});
            skLineSegment(sketch, "E6.14.5.2", {"start": v(64.57, 25.61) * mm, "end": v(59.94, 25.61) * mm});
            skLineSegment(sketch, "E6.14.5.3", {"start": v(59.94, 25.61) * mm, "end": v(59.94, 30.23) * mm});
            skLineSegment(sketch, "E6.14.6.0", {"start": v(64.57, 17.53) * mm, "end": v(59.94, 17.53) * mm});
            skLineSegment(sketch, "E6.14.6.1", {"start": v(64.57, 12.91) * mm, "end": v(64.57, 17.53) * mm});
            skLineSegment(sketch, "E6.14.6.2", {"start": v(64.57, 12.91) * mm, "end": v(59.94, 12.91) * mm});
            skLineSegment(sketch, "E6.14.6.3", {"start": v(59.94, 12.91) * mm, "end": v(59.94, 17.53) * mm});
            skLineSegment(sketch, "E6.14.7.0", {"start": v(64.57, 4.83) * mm, "end": v(59.94, 4.83) * mm});
            skLineSegment(sketch, "E6.14.7.1", {"start": v(64.57, 0.21) * mm, "end": v(64.57, 4.83) * mm});
            skLineSegment(sketch, "E6.14.7.2", {"start": v(64.57, 0.21) * mm, "end": v(59.94, 0.21) * mm});
            skLineSegment(sketch, "E6.14.7.3", {"start": v(59.94, 0.21) * mm, "end": v(59.94, 4.83) * mm});
            skLineSegment(sketch, "E6.14.8.0", {"start": v(64.57, -7.87) * mm, "end": v(59.94, -7.87) * mm});
            skLineSegment(sketch, "E6.14.8.1", {"start": v(64.57, -12.49) * mm, "end": v(64.57, -7.87) * mm});
            skLineSegment(sketch, "E6.14.8.2", {"start": v(64.57, -12.49) * mm, "end": v(59.94, -12.49) * mm});
            skLineSegment(sketch, "E6.14.8.3", {"start": v(59.94, -12.49) * mm, "end": v(59.94, -7.87) * mm});
            skLineSegment(sketch, "E6.14.9.0", {"start": v(64.57, -20.57) * mm, "end": v(59.94, -20.57) * mm});
            skLineSegment(sketch, "E6.14.9.1", {"start": v(64.57, -25.19) * mm, "end": v(64.57, -20.57) * mm});
            skLineSegment(sketch, "E6.14.9.2", {"start": v(64.57, -25.19) * mm, "end": v(59.94, -25.19) * mm});
            skLineSegment(sketch, "E6.14.9.3", {"start": v(59.94, -25.19) * mm, "end": v(59.94, -20.57) * mm});
            skLineSegment(sketch, "E6.14.10.0", {"start": v(64.57, -33.27) * mm, "end": v(59.94, -33.27) * mm});
            skLineSegment(sketch, "E6.14.10.1", {"start": v(64.57, -37.89) * mm, "end": v(64.57, -33.27) * mm});
            skLineSegment(sketch, "E6.14.10.2", {"start": v(64.57, -37.89) * mm, "end": v(59.94, -37.89) * mm});
            skLineSegment(sketch, "E6.14.10.3", {"start": v(59.94, -37.89) * mm, "end": v(59.94, -33.27) * mm});
            skLineSegment(sketch, "E6.14.11.0", {"start": v(64.57, -45.97) * mm, "end": v(59.94, -45.97) * mm});
            skLineSegment(sketch, "E6.14.11.1", {"start": v(64.57, -50.59) * mm, "end": v(64.57, -45.97) * mm});
            skLineSegment(sketch, "E6.14.11.2", {"start": v(64.57, -50.59) * mm, "end": v(59.94, -50.59) * mm});
            skLineSegment(sketch, "E6.14.11.3", {"start": v(59.94, -50.59) * mm, "end": v(59.94, -45.97) * mm});
            skLineSegment(sketch, "E6.14.12.0", {"start": v(64.57, -58.67) * mm, "end": v(59.94, -58.67) * mm});
            skLineSegment(sketch, "E6.14.12.1", {"start": v(64.57, -63.29) * mm, "end": v(64.57, -58.67) * mm});
            skLineSegment(sketch, "E6.14.12.2", {"start": v(64.57, -63.29) * mm, "end": v(59.94, -63.29) * mm});
            skLineSegment(sketch, "E6.14.12.3", {"start": v(59.94, -63.29) * mm, "end": v(59.94, -58.67) * mm});
            skLineSegment(sketch, "E6.15.0.0", {"start": v(77.27, 93.73) * mm, "end": v(72.64, 93.73) * mm});
            skLineSegment(sketch, "E6.15.0.1", {"start": v(77.27, 89.11) * mm, "end": v(77.27, 93.73) * mm});
            skLineSegment(sketch, "E6.15.0.2", {"start": v(77.27, 89.11) * mm, "end": v(72.64, 89.11) * mm});
            skLineSegment(sketch, "E6.15.0.3", {"start": v(72.64, 89.11) * mm, "end": v(72.64, 93.73) * mm});
            skLineSegment(sketch, "E6.15.1.0", {"start": v(77.27, 81.03) * mm, "end": v(72.64, 81.03) * mm});
            skLineSegment(sketch, "E6.15.1.1", {"start": v(77.27, 76.41) * mm, "end": v(77.27, 81.03) * mm});
            skLineSegment(sketch, "E6.15.1.2", {"start": v(77.27, 76.41) * mm, "end": v(72.64, 76.41) * mm});
            skLineSegment(sketch, "E6.15.1.3", {"start": v(72.64, 76.41) * mm, "end": v(72.64, 81.03) * mm});
            skLineSegment(sketch, "E6.15.2.0", {"start": v(77.27, 68.33) * mm, "end": v(72.64, 68.33) * mm});
            skLineSegment(sketch, "E6.15.2.1", {"start": v(77.27, 63.71) * mm, "end": v(77.27, 68.33) * mm});
            skLineSegment(sketch, "E6.15.2.2", {"start": v(77.27, 63.71) * mm, "end": v(72.64, 63.71) * mm});
            skLineSegment(sketch, "E6.15.2.3", {"start": v(72.64, 63.71) * mm, "end": v(72.64, 68.33) * mm});
            skLineSegment(sketch, "E6.15.3.0", {"start": v(77.27, 55.63) * mm, "end": v(72.64, 55.63) * mm});
            skLineSegment(sketch, "E6.15.3.1", {"start": v(77.27, 51.01) * mm, "end": v(77.27, 55.63) * mm});
            skLineSegment(sketch, "E6.15.3.2", {"start": v(77.27, 51.01) * mm, "end": v(72.64, 51.01) * mm});
            skLineSegment(sketch, "E6.15.3.3", {"start": v(72.64, 51.01) * mm, "end": v(72.64, 55.63) * mm});
            skLineSegment(sketch, "E6.15.4.0", {"start": v(77.27, 42.93) * mm, "end": v(72.64, 42.93) * mm});
            skLineSegment(sketch, "E6.15.4.1", {"start": v(77.27, 38.31) * mm, "end": v(77.27, 42.93) * mm});
            skLineSegment(sketch, "E6.15.4.2", {"start": v(77.27, 38.31) * mm, "end": v(72.64, 38.31) * mm});
            skLineSegment(sketch, "E6.15.4.3", {"start": v(72.64, 38.31) * mm, "end": v(72.64, 42.93) * mm});
            skLineSegment(sketch, "E6.15.5.0", {"start": v(77.27, 30.23) * mm, "end": v(72.64, 30.23) * mm});
            skLineSegment(sketch, "E6.15.5.1", {"start": v(77.27, 25.61) * mm, "end": v(77.27, 30.23) * mm});
            skLineSegment(sketch, "E6.15.5.2", {"start": v(77.27, 25.61) * mm, "end": v(72.64, 25.61) * mm});
            skLineSegment(sketch, "E6.15.5.3", {"start": v(72.64, 25.61) * mm, "end": v(72.64, 30.23) * mm});
            skLineSegment(sketch, "E6.15.6.0", {"start": v(77.27, 17.53) * mm, "end": v(72.64, 17.53) * mm});
            skLineSegment(sketch, "E6.15.6.1", {"start": v(77.27, 12.91) * mm, "end": v(77.27, 17.53) * mm});
            skLineSegment(sketch, "E6.15.6.2", {"start": v(77.27, 12.91) * mm, "end": v(72.64, 12.91) * mm});
            skLineSegment(sketch, "E6.15.6.3", {"start": v(72.64, 12.91) * mm, "end": v(72.64, 17.53) * mm});
            skLineSegment(sketch, "E6.15.7.0", {"start": v(77.27, 4.83) * mm, "end": v(72.64, 4.83) * mm});
            skLineSegment(sketch, "E6.15.7.1", {"start": v(77.27, 0.21) * mm, "end": v(77.27, 4.83) * mm});
            skLineSegment(sketch, "E6.15.7.2", {"start": v(77.27, 0.21) * mm, "end": v(72.64, 0.21) * mm});
            skLineSegment(sketch, "E6.15.7.3", {"start": v(72.64, 0.21) * mm, "end": v(72.64, 4.83) * mm});
            skLineSegment(sketch, "E6.15.8.0", {"start": v(77.27, -7.87) * mm, "end": v(72.64, -7.87) * mm});
            skLineSegment(sketch, "E6.15.8.1", {"start": v(77.27, -12.49) * mm, "end": v(77.27, -7.87) * mm});
            skLineSegment(sketch, "E6.15.8.2", {"start": v(77.27, -12.49) * mm, "end": v(72.64, -12.49) * mm});
            skLineSegment(sketch, "E6.15.8.3", {"start": v(72.64, -12.49) * mm, "end": v(72.64, -7.87) * mm});
            skLineSegment(sketch, "E6.15.9.0", {"start": v(77.27, -20.57) * mm, "end": v(72.64, -20.57) * mm});
            skLineSegment(sketch, "E6.15.9.1", {"start": v(77.27, -25.19) * mm, "end": v(77.27, -20.57) * mm});
            skLineSegment(sketch, "E6.15.9.2", {"start": v(77.27, -25.19) * mm, "end": v(72.64, -25.19) * mm});
            skLineSegment(sketch, "E6.15.9.3", {"start": v(72.64, -25.19) * mm, "end": v(72.64, -20.57) * mm});
            skLineSegment(sketch, "E6.15.10.0", {"start": v(77.27, -33.27) * mm, "end": v(72.64, -33.27) * mm});
            skLineSegment(sketch, "E6.15.10.1", {"start": v(77.27, -37.89) * mm, "end": v(77.27, -33.27) * mm});
            skLineSegment(sketch, "E6.15.10.2", {"start": v(77.27, -37.89) * mm, "end": v(72.64, -37.89) * mm});
            skLineSegment(sketch, "E6.15.10.3", {"start": v(72.64, -37.89) * mm, "end": v(72.64, -33.27) * mm});
            skLineSegment(sketch, "E6.15.11.0", {"start": v(77.27, -45.97) * mm, "end": v(72.64, -45.97) * mm});
            skLineSegment(sketch, "E6.15.11.1", {"start": v(77.27, -50.59) * mm, "end": v(77.27, -45.97) * mm});
            skLineSegment(sketch, "E6.15.11.2", {"start": v(77.27, -50.59) * mm, "end": v(72.64, -50.59) * mm});
            skLineSegment(sketch, "E6.15.11.3", {"start": v(72.64, -50.59) * mm, "end": v(72.64, -45.97) * mm});
            skLineSegment(sketch, "E6.15.12.0", {"start": v(77.27, -58.67) * mm, "end": v(72.64, -58.67) * mm});
            skLineSegment(sketch, "E6.15.12.1", {"start": v(77.27, -63.29) * mm, "end": v(77.27, -58.67) * mm});
            skLineSegment(sketch, "E6.15.12.2", {"start": v(77.27, -63.29) * mm, "end": v(72.64, -63.29) * mm});
            skLineSegment(sketch, "E6.15.12.3", {"start": v(72.64, -63.29) * mm, "end": v(72.64, -58.67) * mm});
            skLineSegment(sketch, "E6.16.0.0", {"start": v(89.97, 93.73) * mm, "end": v(85.34, 93.73) * mm});
            skLineSegment(sketch, "E6.16.0.1", {"start": v(89.97, 89.11) * mm, "end": v(89.97, 93.73) * mm});
            skLineSegment(sketch, "E6.16.0.2", {"start": v(89.97, 89.11) * mm, "end": v(85.34, 89.11) * mm});
            skLineSegment(sketch, "E6.16.0.3", {"start": v(85.34, 89.11) * mm, "end": v(85.34, 93.73) * mm});
            skLineSegment(sketch, "E6.16.1.0", {"start": v(89.97, 81.03) * mm, "end": v(85.34, 81.03) * mm});
            skLineSegment(sketch, "E6.16.1.1", {"start": v(89.97, 76.41) * mm, "end": v(89.97, 81.03) * mm});
            skLineSegment(sketch, "E6.16.1.2", {"start": v(89.97, 76.41) * mm, "end": v(85.34, 76.41) * mm});
            skLineSegment(sketch, "E6.16.1.3", {"start": v(85.34, 76.41) * mm, "end": v(85.34, 81.03) * mm});
            skLineSegment(sketch, "E6.16.2.0", {"start": v(89.97, 68.33) * mm, "end": v(85.34, 68.33) * mm});
            skLineSegment(sketch, "E6.16.2.1", {"start": v(89.97, 63.71) * mm, "end": v(89.97, 68.33) * mm});
            skLineSegment(sketch, "E6.16.2.2", {"start": v(89.97, 63.71) * mm, "end": v(85.34, 63.71) * mm});
            skLineSegment(sketch, "E6.16.2.3", {"start": v(85.34, 63.71) * mm, "end": v(85.34, 68.33) * mm});
            skLineSegment(sketch, "E6.16.3.0", {"start": v(89.97, 55.63) * mm, "end": v(85.34, 55.63) * mm});
            skLineSegment(sketch, "E6.16.3.1", {"start": v(89.97, 51.01) * mm, "end": v(89.97, 55.63) * mm});
            skLineSegment(sketch, "E6.16.3.2", {"start": v(89.97, 51.01) * mm, "end": v(85.34, 51.01) * mm});
            skLineSegment(sketch, "E6.16.3.3", {"start": v(85.34, 51.01) * mm, "end": v(85.34, 55.63) * mm});
            skLineSegment(sketch, "E6.16.4.0", {"start": v(89.97, 42.93) * mm, "end": v(85.34, 42.93) * mm});
            skLineSegment(sketch, "E6.16.4.1", {"start": v(89.97, 38.31) * mm, "end": v(89.97, 42.93) * mm});
            skLineSegment(sketch, "E6.16.4.2", {"start": v(89.97, 38.31) * mm, "end": v(85.34, 38.31) * mm});
            skLineSegment(sketch, "E6.16.4.3", {"start": v(85.34, 38.31) * mm, "end": v(85.34, 42.93) * mm});
            skLineSegment(sketch, "E6.16.5.0", {"start": v(89.97, 30.23) * mm, "end": v(85.34, 30.23) * mm});
            skLineSegment(sketch, "E6.16.5.1", {"start": v(89.97, 25.61) * mm, "end": v(89.97, 30.23) * mm});
            skLineSegment(sketch, "E6.16.5.2", {"start": v(89.97, 25.61) * mm, "end": v(85.34, 25.61) * mm});
            skLineSegment(sketch, "E6.16.5.3", {"start": v(85.34, 25.61) * mm, "end": v(85.34, 30.23) * mm});
            skLineSegment(sketch, "E6.16.6.0", {"start": v(89.97, 17.53) * mm, "end": v(85.34, 17.53) * mm});
            skLineSegment(sketch, "E6.16.6.1", {"start": v(89.97, 12.91) * mm, "end": v(89.97, 17.53) * mm});
            skLineSegment(sketch, "E6.16.6.2", {"start": v(89.97, 12.91) * mm, "end": v(85.34, 12.91) * mm});
            skLineSegment(sketch, "E6.16.6.3", {"start": v(85.34, 12.91) * mm, "end": v(85.34, 17.53) * mm});
            skLineSegment(sketch, "E6.16.7.0", {"start": v(89.97, 4.83) * mm, "end": v(85.34, 4.83) * mm});
            skLineSegment(sketch, "E6.16.7.1", {"start": v(89.97, 0.21) * mm, "end": v(89.97, 4.83) * mm});
            skLineSegment(sketch, "E6.16.7.2", {"start": v(89.97, 0.21) * mm, "end": v(85.34, 0.21) * mm});
            skLineSegment(sketch, "E6.16.7.3", {"start": v(85.34, 0.21) * mm, "end": v(85.34, 4.83) * mm});
            skLineSegment(sketch, "E6.16.8.0", {"start": v(89.97, -7.87) * mm, "end": v(85.34, -7.87) * mm});
            skLineSegment(sketch, "E6.16.8.1", {"start": v(89.97, -12.49) * mm, "end": v(89.97, -7.87) * mm});
            skLineSegment(sketch, "E6.16.8.2", {"start": v(89.97, -12.49) * mm, "end": v(85.34, -12.49) * mm});
            skLineSegment(sketch, "E6.16.8.3", {"start": v(85.34, -12.49) * mm, "end": v(85.34, -7.87) * mm});
            skLineSegment(sketch, "E6.16.9.0", {"start": v(89.97, -20.57) * mm, "end": v(85.34, -20.57) * mm});
            skLineSegment(sketch, "E6.16.9.1", {"start": v(89.97, -25.19) * mm, "end": v(89.97, -20.57) * mm});
            skLineSegment(sketch, "E6.16.9.2", {"start": v(89.97, -25.19) * mm, "end": v(85.34, -25.19) * mm});
            skLineSegment(sketch, "E6.16.9.3", {"start": v(85.34, -25.19) * mm, "end": v(85.34, -20.57) * mm});
            skLineSegment(sketch, "E6.16.10.0", {"start": v(89.97, -33.27) * mm, "end": v(85.34, -33.27) * mm});
            skLineSegment(sketch, "E6.16.10.1", {"start": v(89.97, -37.89) * mm, "end": v(89.97, -33.27) * mm});
            skLineSegment(sketch, "E6.16.10.2", {"start": v(89.97, -37.89) * mm, "end": v(85.34, -37.89) * mm});
            skLineSegment(sketch, "E6.16.10.3", {"start": v(85.34, -37.89) * mm, "end": v(85.34, -33.27) * mm});
            skLineSegment(sketch, "E6.16.11.0", {"start": v(89.97, -45.97) * mm, "end": v(85.34, -45.97) * mm});
            skLineSegment(sketch, "E6.16.11.1", {"start": v(89.97, -50.59) * mm, "end": v(89.97, -45.97) * mm});
            skLineSegment(sketch, "E6.16.11.2", {"start": v(89.97, -50.59) * mm, "end": v(85.34, -50.59) * mm});
            skLineSegment(sketch, "E6.16.11.3", {"start": v(85.34, -50.59) * mm, "end": v(85.34, -45.97) * mm});
            skLineSegment(sketch, "E6.16.12.0", {"start": v(89.97, -58.67) * mm, "end": v(85.34, -58.67) * mm});
            skLineSegment(sketch, "E6.16.12.1", {"start": v(89.97, -63.29) * mm, "end": v(89.97, -58.67) * mm});
            skLineSegment(sketch, "E6.16.12.2", {"start": v(89.97, -63.29) * mm, "end": v(85.34, -63.29) * mm});
            skLineSegment(sketch, "E6.16.12.3", {"start": v(85.34, -63.29) * mm, "end": v(85.34, -58.67) * mm});
            skLineSegment(sketch, "E6.17.0.0", {"start": v(102.67, 93.73) * mm, "end": v(98.04, 93.73) * mm});
            skLineSegment(sketch, "E6.17.0.1", {"start": v(102.67, 89.11) * mm, "end": v(102.67, 93.73) * mm});
            skLineSegment(sketch, "E6.17.0.2", {"start": v(102.67, 89.11) * mm, "end": v(98.04, 89.11) * mm});
            skLineSegment(sketch, "E6.17.0.3", {"start": v(98.04, 89.11) * mm, "end": v(98.04, 93.73) * mm});
            skLineSegment(sketch, "E6.17.1.0", {"start": v(102.67, 81.03) * mm, "end": v(98.04, 81.03) * mm});
            skLineSegment(sketch, "E6.17.1.1", {"start": v(102.67, 76.41) * mm, "end": v(102.67, 81.03) * mm});
            skLineSegment(sketch, "E6.17.1.2", {"start": v(102.67, 76.41) * mm, "end": v(98.04, 76.41) * mm});
            skLineSegment(sketch, "E6.17.1.3", {"start": v(98.04, 76.41) * mm, "end": v(98.04, 81.03) * mm});
            skLineSegment(sketch, "E6.17.2.0", {"start": v(102.67, 68.33) * mm, "end": v(98.04, 68.33) * mm});
            skLineSegment(sketch, "E6.17.2.1", {"start": v(102.67, 63.71) * mm, "end": v(102.67, 68.33) * mm});
            skLineSegment(sketch, "E6.17.2.2", {"start": v(102.67, 63.71) * mm, "end": v(98.04, 63.71) * mm});
            skLineSegment(sketch, "E6.17.2.3", {"start": v(98.04, 63.71) * mm, "end": v(98.04, 68.33) * mm});
            skLineSegment(sketch, "E6.17.3.0", {"start": v(102.67, 55.63) * mm, "end": v(98.04, 55.63) * mm});
            skLineSegment(sketch, "E6.17.3.1", {"start": v(102.67, 51.01) * mm, "end": v(102.67, 55.63) * mm});
            skLineSegment(sketch, "E6.17.3.2", {"start": v(102.67, 51.01) * mm, "end": v(98.04, 51.01) * mm});
            skLineSegment(sketch, "E6.17.3.3", {"start": v(98.04, 51.01) * mm, "end": v(98.04, 55.63) * mm});
            skLineSegment(sketch, "E6.17.4.0", {"start": v(102.67, 42.93) * mm, "end": v(98.04, 42.93) * mm});
            skLineSegment(sketch, "E6.17.4.1", {"start": v(102.67, 38.31) * mm, "end": v(102.67, 42.93) * mm});
            skLineSegment(sketch, "E6.17.4.2", {"start": v(102.67, 38.31) * mm, "end": v(98.04, 38.31) * mm});
            skLineSegment(sketch, "E6.17.4.3", {"start": v(98.04, 38.31) * mm, "end": v(98.04, 42.93) * mm});
            skLineSegment(sketch, "E6.17.5.0", {"start": v(102.67, 30.23) * mm, "end": v(98.04, 30.23) * mm});
            skLineSegment(sketch, "E6.17.5.1", {"start": v(102.67, 25.61) * mm, "end": v(102.67, 30.23) * mm});
            skLineSegment(sketch, "E6.17.5.2", {"start": v(102.67, 25.61) * mm, "end": v(98.04, 25.61) * mm});
            skLineSegment(sketch, "E6.17.5.3", {"start": v(98.04, 25.61) * mm, "end": v(98.04, 30.23) * mm});
            skLineSegment(sketch, "E6.17.6.0", {"start": v(102.67, 17.53) * mm, "end": v(98.04, 17.53) * mm});
            skLineSegment(sketch, "E6.17.6.1", {"start": v(102.67, 12.91) * mm, "end": v(102.67, 17.53) * mm});
            skLineSegment(sketch, "E6.17.6.2", {"start": v(102.67, 12.91) * mm, "end": v(98.04, 12.91) * mm});
            skLineSegment(sketch, "E6.17.6.3", {"start": v(98.04, 12.91) * mm, "end": v(98.04, 17.53) * mm});
            skLineSegment(sketch, "E6.17.7.0", {"start": v(102.67, 4.83) * mm, "end": v(98.04, 4.83) * mm});
            skLineSegment(sketch, "E6.17.7.1", {"start": v(102.67, 0.21) * mm, "end": v(102.67, 4.83) * mm});
            skLineSegment(sketch, "E6.17.7.2", {"start": v(102.67, 0.21) * mm, "end": v(98.04, 0.21) * mm});
            skLineSegment(sketch, "E6.17.7.3", {"start": v(98.04, 0.21) * mm, "end": v(98.04, 4.83) * mm});
            skLineSegment(sketch, "E6.17.8.0", {"start": v(102.67, -7.87) * mm, "end": v(98.04, -7.87) * mm});
            skLineSegment(sketch, "E6.17.8.1", {"start": v(102.67, -12.49) * mm, "end": v(102.67, -7.87) * mm});
            skLineSegment(sketch, "E6.17.8.2", {"start": v(102.67, -12.49) * mm, "end": v(98.04, -12.49) * mm});
            skLineSegment(sketch, "E6.17.8.3", {"start": v(98.04, -12.49) * mm, "end": v(98.04, -7.87) * mm});
            skLineSegment(sketch, "E6.17.9.0", {"start": v(102.67, -20.57) * mm, "end": v(98.04, -20.57) * mm});
            skLineSegment(sketch, "E6.17.9.1", {"start": v(102.67, -25.19) * mm, "end": v(102.67, -20.57) * mm});
            skLineSegment(sketch, "E6.17.9.2", {"start": v(102.67, -25.19) * mm, "end": v(98.04, -25.19) * mm});
            skLineSegment(sketch, "E6.17.9.3", {"start": v(98.04, -25.19) * mm, "end": v(98.04, -20.57) * mm});
            skLineSegment(sketch, "E6.17.10.0", {"start": v(102.67, -33.27) * mm, "end": v(98.04, -33.27) * mm});
            skLineSegment(sketch, "E6.17.10.1", {"start": v(102.67, -37.89) * mm, "end": v(102.67, -33.27) * mm});
            skLineSegment(sketch, "E6.17.10.2", {"start": v(102.67, -37.89) * mm, "end": v(98.04, -37.89) * mm});
            skLineSegment(sketch, "E6.17.10.3", {"start": v(98.04, -37.89) * mm, "end": v(98.04, -33.27) * mm});
            skLineSegment(sketch, "E6.17.11.0", {"start": v(102.67, -45.97) * mm, "end": v(98.04, -45.97) * mm});
            skLineSegment(sketch, "E6.17.11.1", {"start": v(102.67, -50.59) * mm, "end": v(102.67, -45.97) * mm});
            skLineSegment(sketch, "E6.17.11.2", {"start": v(102.67, -50.59) * mm, "end": v(98.04, -50.59) * mm});
            skLineSegment(sketch, "E6.17.11.3", {"start": v(98.04, -50.59) * mm, "end": v(98.04, -45.97) * mm});
            skLineSegment(sketch, "E6.17.12.0", {"start": v(102.67, -58.67) * mm, "end": v(98.04, -58.67) * mm});
            skLineSegment(sketch, "E6.17.12.1", {"start": v(102.67, -63.29) * mm, "end": v(102.67, -58.67) * mm});
            skLineSegment(sketch, "E6.17.12.2", {"start": v(102.67, -63.29) * mm, "end": v(98.04, -63.29) * mm});
            skLineSegment(sketch, "E6.17.12.3", {"start": v(98.04, -63.29) * mm, "end": v(98.04, -58.67) * mm});
            skLineSegment(sketch, "E6.18.0.0", {"start": v(115.37, 93.73) * mm, "end": v(110.74, 93.73) * mm});
            skLineSegment(sketch, "E6.18.0.1", {"start": v(115.37, 89.11) * mm, "end": v(115.37, 93.73) * mm});
            skLineSegment(sketch, "E6.18.0.2", {"start": v(115.37, 89.11) * mm, "end": v(110.74, 89.11) * mm});
            skLineSegment(sketch, "E6.18.0.3", {"start": v(110.74, 89.11) * mm, "end": v(110.74, 93.73) * mm});
            skLineSegment(sketch, "E6.18.1.0", {"start": v(115.37, 81.03) * mm, "end": v(110.74, 81.03) * mm});
            skLineSegment(sketch, "E6.18.1.1", {"start": v(115.37, 76.41) * mm, "end": v(115.37, 81.03) * mm});
            skLineSegment(sketch, "E6.18.1.2", {"start": v(115.37, 76.41) * mm, "end": v(110.74, 76.41) * mm});
            skLineSegment(sketch, "E6.18.1.3", {"start": v(110.74, 76.41) * mm, "end": v(110.74, 81.03) * mm});
            skLineSegment(sketch, "E6.18.2.0", {"start": v(115.37, 68.33) * mm, "end": v(110.74, 68.33) * mm});
            skLineSegment(sketch, "E6.18.2.1", {"start": v(115.37, 63.71) * mm, "end": v(115.37, 68.33) * mm});
            skLineSegment(sketch, "E6.18.2.2", {"start": v(115.37, 63.71) * mm, "end": v(110.74, 63.71) * mm});
            skLineSegment(sketch, "E6.18.2.3", {"start": v(110.74, 63.71) * mm, "end": v(110.74, 68.33) * mm});
            skLineSegment(sketch, "E6.18.3.0", {"start": v(115.37, 55.63) * mm, "end": v(110.74, 55.63) * mm});
            skLineSegment(sketch, "E6.18.3.1", {"start": v(115.37, 51.01) * mm, "end": v(115.37, 55.63) * mm});
            skLineSegment(sketch, "E6.18.3.2", {"start": v(115.37, 51.01) * mm, "end": v(110.74, 51.01) * mm});
            skLineSegment(sketch, "E6.18.3.3", {"start": v(110.74, 51.01) * mm, "end": v(110.74, 55.63) * mm});
            skLineSegment(sketch, "E6.18.4.0", {"start": v(115.37, 42.93) * mm, "end": v(110.74, 42.93) * mm});
            skLineSegment(sketch, "E6.18.4.1", {"start": v(115.37, 38.31) * mm, "end": v(115.37, 42.93) * mm});
            skLineSegment(sketch, "E6.18.4.2", {"start": v(115.37, 38.31) * mm, "end": v(110.74, 38.31) * mm});
            skLineSegment(sketch, "E6.18.4.3", {"start": v(110.74, 38.31) * mm, "end": v(110.74, 42.93) * mm});
            skLineSegment(sketch, "E6.18.5.0", {"start": v(115.37, 30.23) * mm, "end": v(110.74, 30.23) * mm});
            skLineSegment(sketch, "E6.18.5.1", {"start": v(115.37, 25.61) * mm, "end": v(115.37, 30.23) * mm});
            skLineSegment(sketch, "E6.18.5.2", {"start": v(115.37, 25.61) * mm, "end": v(110.74, 25.61) * mm});
            skLineSegment(sketch, "E6.18.5.3", {"start": v(110.74, 25.61) * mm, "end": v(110.74, 30.23) * mm});
            skLineSegment(sketch, "E6.18.6.0", {"start": v(115.37, 17.53) * mm, "end": v(110.74, 17.53) * mm});
            skLineSegment(sketch, "E6.18.6.1", {"start": v(115.37, 12.91) * mm, "end": v(115.37, 17.53) * mm});
            skLineSegment(sketch, "E6.18.6.2", {"start": v(115.37, 12.91) * mm, "end": v(110.74, 12.91) * mm});
            skLineSegment(sketch, "E6.18.6.3", {"start": v(110.74, 12.91) * mm, "end": v(110.74, 17.53) * mm});
            skLineSegment(sketch, "E6.18.7.0", {"start": v(115.37, 4.83) * mm, "end": v(110.74, 4.83) * mm});
            skLineSegment(sketch, "E6.18.7.1", {"start": v(115.37, 0.21) * mm, "end": v(115.37, 4.83) * mm});
            skLineSegment(sketch, "E6.18.7.2", {"start": v(115.37, 0.21) * mm, "end": v(110.74, 0.21) * mm});
            skLineSegment(sketch, "E6.18.7.3", {"start": v(110.74, 0.21) * mm, "end": v(110.74, 4.83) * mm});
            skLineSegment(sketch, "E6.18.8.0", {"start": v(115.37, -7.87) * mm, "end": v(110.74, -7.87) * mm});
            skLineSegment(sketch, "E6.18.8.1", {"start": v(115.37, -12.49) * mm, "end": v(115.37, -7.87) * mm});
            skLineSegment(sketch, "E6.18.8.2", {"start": v(115.37, -12.49) * mm, "end": v(110.74, -12.49) * mm});
            skLineSegment(sketch, "E6.18.8.3", {"start": v(110.74, -12.49) * mm, "end": v(110.74, -7.87) * mm});
            skLineSegment(sketch, "E6.18.9.0", {"start": v(115.37, -20.57) * mm, "end": v(110.74, -20.57) * mm});
            skLineSegment(sketch, "E6.18.9.1", {"start": v(115.37, -25.19) * mm, "end": v(115.37, -20.57) * mm});
            skLineSegment(sketch, "E6.18.9.2", {"start": v(115.37, -25.19) * mm, "end": v(110.74, -25.19) * mm});
            skLineSegment(sketch, "E6.18.9.3", {"start": v(110.74, -25.19) * mm, "end": v(110.74, -20.57) * mm});
            skLineSegment(sketch, "E6.18.10.0", {"start": v(115.37, -33.27) * mm, "end": v(110.74, -33.27) * mm});
            skLineSegment(sketch, "E6.18.10.1", {"start": v(115.37, -37.89) * mm, "end": v(115.37, -33.27) * mm});
            skLineSegment(sketch, "E6.18.10.2", {"start": v(115.37, -37.89) * mm, "end": v(110.74, -37.89) * mm});
            skLineSegment(sketch, "E6.18.10.3", {"start": v(110.74, -37.89) * mm, "end": v(110.74, -33.27) * mm});
            skLineSegment(sketch, "E6.18.11.0", {"start": v(115.37, -45.97) * mm, "end": v(110.74, -45.97) * mm});
            skLineSegment(sketch, "E6.18.11.1", {"start": v(115.37, -50.59) * mm, "end": v(115.37, -45.97) * mm});
            skLineSegment(sketch, "E6.18.11.2", {"start": v(115.37, -50.59) * mm, "end": v(110.74, -50.59) * mm});
            skLineSegment(sketch, "E6.18.11.3", {"start": v(110.74, -50.59) * mm, "end": v(110.74, -45.97) * mm});
            skLineSegment(sketch, "E6.18.12.0", {"start": v(115.37, -58.67) * mm, "end": v(110.74, -58.67) * mm});
            skLineSegment(sketch, "E6.18.12.1", {"start": v(115.37, -63.29) * mm, "end": v(115.37, -58.67) * mm});
            skLineSegment(sketch, "E6.18.12.2", {"start": v(115.37, -63.29) * mm, "end": v(110.74, -63.29) * mm});
            skLineSegment(sketch, "E6.18.12.3", {"start": v(110.74, -63.29) * mm, "end": v(110.74, -58.67) * mm});
            skLineSegment(sketch, "E6.direction1", {"start": v(-117.86, 93.73) * mm, "end": v(-105.16, 93.73) * mm, "construction": true});
            skLineSegment(sketch, "E6.direction2", {"start": v(-117.86, 93.73) * mm, "end": v(-117.86, 81.03) * mm, "construction": true});
            skSolve(sketch);
        }
        {
            var Q0;
            Q0=makeQuery(id+"F0.imprint","IMPRINT",FACE,{"disambiguationData":[TD([[makeQuery(id+"F0.imprint","IMPRINT",EDGE,{"derivedFrom":sQuery(id+"F0.wireOp",EDGE,"E0.bottom")}),1.0]])]});
            extrude(context, id + "F1", {"entities" : qUnion([Q0]), "depth" : 5.08 * mm});
        }
    });
